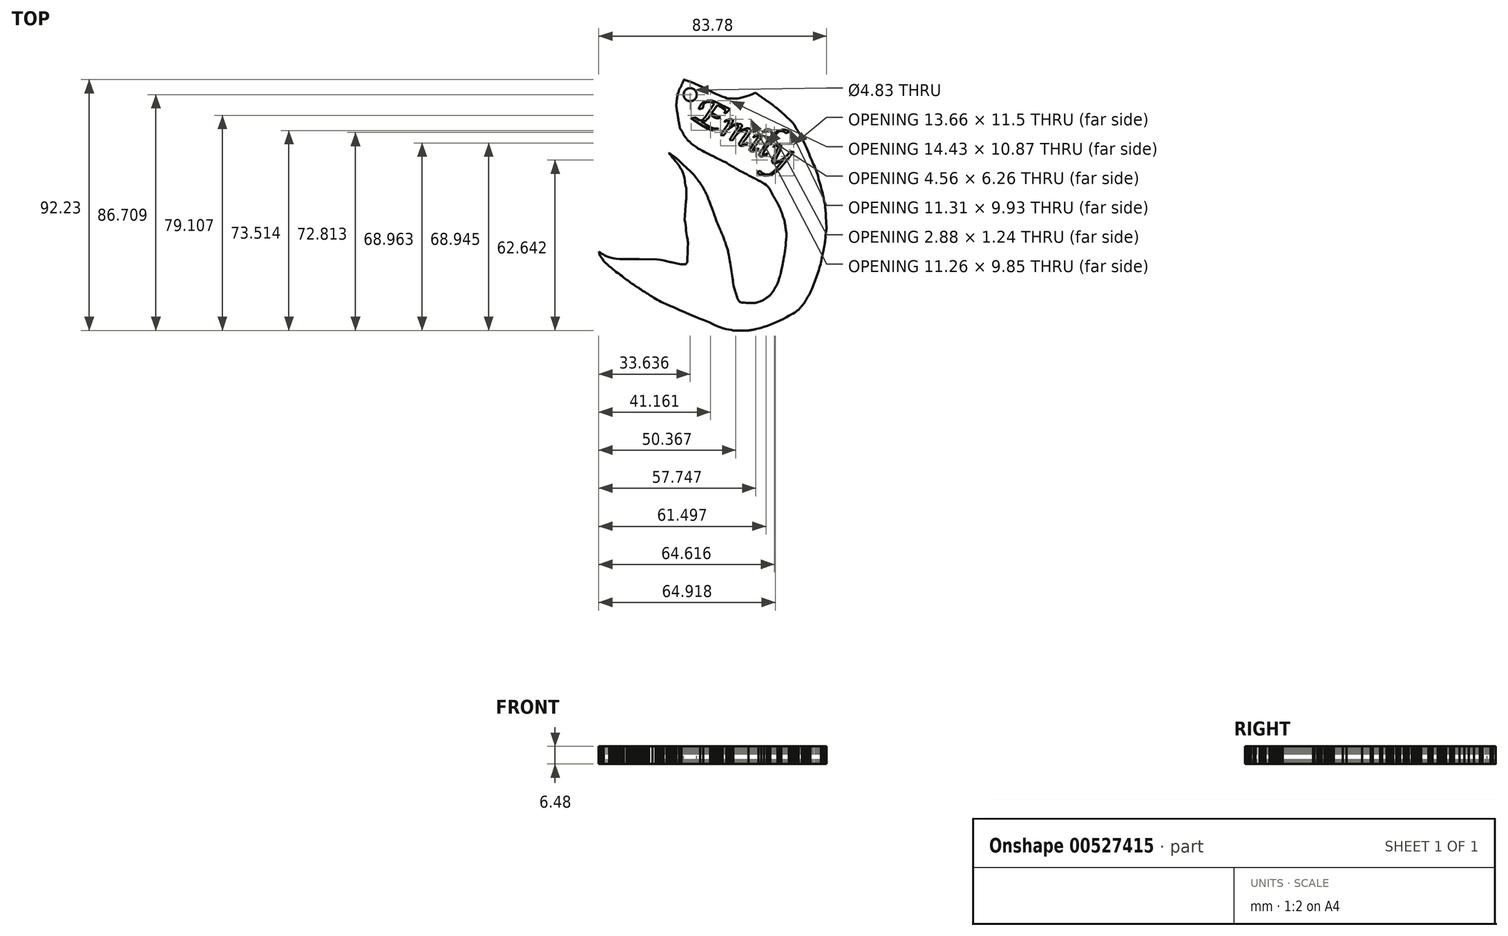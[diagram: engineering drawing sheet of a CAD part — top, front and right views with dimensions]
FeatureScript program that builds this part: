
annotation { "Feature Type Name" : "Feature", "Feature Type Description" : "" }
export const myFeature = defineFeature(function(context is Context, id is Id, definition is map)
    precondition{}
    {
        {
            var Q0;
            Q0=qCreatedBy(makeId("Top.planeOp"),FACE);
            var sketch = newSketch(context, id + "F0", { "sketchPlane" : qUnion([Q0])});
            skLineSegment(sketch, "E0", {"start": v(21.99, 68.15) * mm, "end": v(23.77, 67.5) * mm});
            skLineSegment(sketch, "E1", {"start": v(23.77, 67.5) * mm, "end": v(25.3, 66.86) * mm});
            skLineSegment(sketch, "E2", {"start": v(25.3, 66.86) * mm, "end": v(26.57, 66.23) * mm});
            skLineSegment(sketch, "E3", {"start": v(26.57, 66.23) * mm, "end": v(28.12, 65.46) * mm});
            skLineSegment(sketch, "E4", {"start": v(28.12, 65.46) * mm, "end": v(29.2, 64.92) * mm});
            skLineSegment(sketch, "E5", {"start": v(31.16, 64.07) * mm, "end": v(32, 63.75) * mm});
            skLineSegment(sketch, "E6", {"start": v(32, 63.75) * mm, "end": v(32.46, 63.57) * mm});
            skLineSegment(sketch, "E7", {"start": v(32.46, 63.57) * mm, "end": v(33.1, 63.57) * mm});
            skLineSegment(sketch, "E8", {"start": v(33.1, 63.57) * mm, "end": v(33.64, 63.57) * mm});
            skLineSegment(sketch, "E9", {"start": v(33.64, 63.57) * mm, "end": v(34.22, 63.57) * mm});
            skLineSegment(sketch, "E10", {"start": v(34.22, 63.57) * mm, "end": v(35, 63.57) * mm});
            skLineSegment(sketch, "E11", {"start": v(35, 63.57) * mm, "end": v(36.04, 63.75) * mm});
            skLineSegment(sketch, "E12", {"start": v(36.04, 63.75) * mm, "end": v(36.96, 64.03) * mm});
            skLineSegment(sketch, "E13", {"start": v(36.96, 64.03) * mm, "end": v(38.06, 64.36) * mm});
            skLineSegment(sketch, "E14", {"start": v(38.06, 64.36) * mm, "end": v(38.68, 64.6) * mm});
            skLineSegment(sketch, "E15", {"start": v(38.68, 64.6) * mm, "end": v(39.05, 64.77) * mm});
            skLineSegment(sketch, "E16", {"start": v(39.05, 64.77) * mm, "end": v(39.28, 64.95) * mm});
            skLineSegment(sketch, "E17", {"start": v(39.28, 64.95) * mm, "end": v(39.86, 64.6) * mm});
            skLineSegment(sketch, "E18", {"start": v(39.86, 64.6) * mm, "end": v(40.33, 64.28) * mm});
            skLineSegment(sketch, "E19", {"start": v(40.33, 64.28) * mm, "end": v(40.82, 63.93) * mm});
            skLineSegment(sketch, "E20", {"start": v(40.82, 63.93) * mm, "end": v(41.34, 63.57) * mm});
            skLineSegment(sketch, "E21", {"start": v(41.34, 63.57) * mm, "end": v(41.88, 63.2) * mm});
            skLineSegment(sketch, "E22", {"start": v(41.88, 63.2) * mm, "end": v(42.37, 62.85) * mm});
            skLineSegment(sketch, "E23", {"start": v(42.37, 62.85) * mm, "end": v(42.71, 62.67) * mm});
            skLineSegment(sketch, "E24", {"start": v(42.71, 62.67) * mm, "end": v(43.17, 62.35) * mm});
            skLineSegment(sketch, "E25", {"start": v(43.17, 62.35) * mm, "end": v(43.58, 62) * mm});
            skLineSegment(sketch, "E26", {"start": v(43.58, 62) * mm, "end": v(44.02, 61.6) * mm});
            skLineSegment(sketch, "E27", {"start": v(44.02, 61.6) * mm, "end": v(44.38, 61.36) * mm});
            skLineSegment(sketch, "E28", {"start": v(44.38, 61.36) * mm, "end": v(44.82, 61.04) * mm});
            skLineSegment(sketch, "E29", {"start": v(44.82, 61.04) * mm, "end": v(45.43, 60.46) * mm});
            skLineSegment(sketch, "E30", {"start": v(45.43, 60.46) * mm, "end": v(46.73, 59.3) * mm});
            skLineSegment(sketch, "E31", {"start": v(46.73, 59.3) * mm, "end": v(48.15, 57.92) * mm});
            skLineSegment(sketch, "E32", {"start": v(48.15, 57.92) * mm, "end": v(48.71, 57.46) * mm});
            skLineSegment(sketch, "E33", {"start": v(48.71, 57.46) * mm, "end": v(48.94, 56.98) * mm});
            skLineSegment(sketch, "E34", {"start": v(48.94, 56.98) * mm, "end": v(49.26, 56.45) * mm});
            skLineSegment(sketch, "E35", {"start": v(49.26, 56.45) * mm, "end": v(49.56, 55.94) * mm});
            skLineSegment(sketch, "E36", {"start": v(49.56, 55.94) * mm, "end": v(49.85, 55.48) * mm});
            skLineSegment(sketch, "E37", {"start": v(49.85, 55.48) * mm, "end": v(50.12, 54.97) * mm});
            skLineSegment(sketch, "E38", {"start": v(50.12, 54.97) * mm, "end": v(50.43, 54.48) * mm});
            skLineSegment(sketch, "E39", {"start": v(50.43, 54.48) * mm, "end": v(50.72, 53.9) * mm});
            skLineSegment(sketch, "E40", {"start": v(50.72, 53.9) * mm, "end": v(50.98, 53.42) * mm});
            skLineSegment(sketch, "E41", {"start": v(50.98, 53.42) * mm, "end": v(51.17, 53.06) * mm});
            skLineSegment(sketch, "E42", {"start": v(51.17, 53.06) * mm, "end": v(51.4, 52.65) * mm});
            skLineSegment(sketch, "E43", {"start": v(51.4, 52.65) * mm, "end": v(51.57, 52.15) * mm});
            skLineSegment(sketch, "E44", {"start": v(51.57, 52.15) * mm, "end": v(51.77, 51.67) * mm});
            skLineSegment(sketch, "E45", {"start": v(51.77, 51.67) * mm, "end": v(51.97, 51.22) * mm});
            skLineSegment(sketch, "E46", {"start": v(51.97, 51.22) * mm, "end": v(52.16, 50.81) * mm});
            skLineSegment(sketch, "E47", {"start": v(52.16, 50.81) * mm, "end": v(52.33, 50.44) * mm});
            skLineSegment(sketch, "E48", {"start": v(52.33, 50.44) * mm, "end": v(52.57, 49.9) * mm});
            skLineSegment(sketch, "E49", {"start": v(52.57, 49.9) * mm, "end": v(52.77, 49.35) * mm});
            skLineSegment(sketch, "E50", {"start": v(52.77, 49.35) * mm, "end": v(53, 48.84) * mm});
            skLineSegment(sketch, "E51", {"start": v(53, 48.84) * mm, "end": v(53.14, 48.48) * mm});
            skLineSegment(sketch, "E52", {"start": v(53.14, 48.48) * mm, "end": v(53.32, 48.01) * mm});
            skLineSegment(sketch, "E53", {"start": v(53.32, 48.01) * mm, "end": v(53.52, 47.56) * mm});
            skLineSegment(sketch, "E54", {"start": v(53.52, 47.56) * mm, "end": v(53.73, 47.17) * mm});
            skLineSegment(sketch, "E55", {"start": v(53.73, 47.17) * mm, "end": v(53.89, 46.86) * mm});
            skLineSegment(sketch, "E56", {"start": v(53.89, 46.86) * mm, "end": v(54.02, 46.5) * mm});
            skLineSegment(sketch, "E57", {"start": v(54.02, 46.5) * mm, "end": v(54.18, 46.11) * mm});
            skLineSegment(sketch, "E58", {"start": v(54.18, 46.11) * mm, "end": v(54.35, 45.67) * mm});
            skLineSegment(sketch, "E59", {"start": v(54.35, 45.67) * mm, "end": v(54.5, 45.23) * mm});
            skLineSegment(sketch, "E60", {"start": v(54.5, 45.23) * mm, "end": v(54.65, 44.72) * mm});
            skLineSegment(sketch, "E61", {"start": v(54.65, 44.72) * mm, "end": v(54.75, 44.3) * mm});
            skLineSegment(sketch, "E62", {"start": v(54.75, 44.3) * mm, "end": v(54.88, 43.75) * mm});
            skLineSegment(sketch, "E63", {"start": v(54.88, 43.75) * mm, "end": v(55.12, 43) * mm});
            skLineSegment(sketch, "E64", {"start": v(55.12, 43) * mm, "end": v(55.26, 42.44) * mm});
            skLineSegment(sketch, "E65", {"start": v(55.26, 42.44) * mm, "end": v(55.43, 41.9) * mm});
            skLineSegment(sketch, "E66", {"start": v(55.43, 41.9) * mm, "end": v(55.55, 41.4) * mm});
            skLineSegment(sketch, "E67", {"start": v(55.55, 41.4) * mm, "end": v(55.67, 41.03) * mm});
            skLineSegment(sketch, "E68", {"start": v(55.67, 41.03) * mm, "end": v(55.77, 40.72) * mm});
            skLineSegment(sketch, "E69", {"start": v(55.77, 40.72) * mm, "end": v(55.9, 40.32) * mm});
            skLineSegment(sketch, "E70", {"start": v(55.9, 40.32) * mm, "end": v(56, 39.8) * mm});
            skLineSegment(sketch, "E71", {"start": v(56, 39.8) * mm, "end": v(56.06, 39.41) * mm});
            skLineSegment(sketch, "E72", {"start": v(56.06, 39.41) * mm, "end": v(56.14, 38.95) * mm});
            skLineSegment(sketch, "E73", {"start": v(56.14, 38.95) * mm, "end": v(56.22, 38.5) * mm});
            skLineSegment(sketch, "E74", {"start": v(56.22, 38.5) * mm, "end": v(56.3, 38.06) * mm});
            skLineSegment(sketch, "E75", {"start": v(56.3, 38.06) * mm, "end": v(56.43, 37.51) * mm});
            skLineSegment(sketch, "E76", {"start": v(56.43, 37.51) * mm, "end": v(56.48, 36.9) * mm});
            skLineSegment(sketch, "E77", {"start": v(56.48, 36.9) * mm, "end": v(56.54, 36.23) * mm});
            skLineSegment(sketch, "E78", {"start": v(56.54, 36.23) * mm, "end": v(56.62, 35.38) * mm});
            skLineSegment(sketch, "E79", {"start": v(56.62, 35.38) * mm, "end": v(56.67, 34.42) * mm});
            skLineSegment(sketch, "E80", {"start": v(56.67, 34.42) * mm, "end": v(56.72, 33.51) * mm});
            skLineSegment(sketch, "E81", {"start": v(56.72, 33.51) * mm, "end": v(56.8, 31.59) * mm});
            skLineSegment(sketch, "E82", {"start": v(56.8, 31.59) * mm, "end": v(56.68, 30.65) * mm});
            skLineSegment(sketch, "E83", {"start": v(56.68, 30.65) * mm, "end": v(56.6, 29.89) * mm});
            skLineSegment(sketch, "E84", {"start": v(56.6, 29.89) * mm, "end": v(56.51, 29.2) * mm});
            skLineSegment(sketch, "E85", {"start": v(56.51, 29.2) * mm, "end": v(56.43, 28.47) * mm});
            skLineSegment(sketch, "E86", {"start": v(56.43, 28.47) * mm, "end": v(56.35, 28.06) * mm});
            skLineSegment(sketch, "E87", {"start": v(56.35, 28.06) * mm, "end": v(56.26, 27.48) * mm});
            skLineSegment(sketch, "E88", {"start": v(56.26, 27.48) * mm, "end": v(56.18, 27.12) * mm});
            skLineSegment(sketch, "E89", {"start": v(56.18, 27.12) * mm, "end": v(56.09, 26.65) * mm});
            skLineSegment(sketch, "E90", {"start": v(56.09, 26.65) * mm, "end": v(56.03, 26.18) * mm});
            skLineSegment(sketch, "E91", {"start": v(56.03, 26.18) * mm, "end": v(55.96, 25.86) * mm});
            skLineSegment(sketch, "E92", {"start": v(55.96, 25.86) * mm, "end": v(55.89, 25.52) * mm});
            skLineSegment(sketch, "E93", {"start": v(55.89, 25.52) * mm, "end": v(55.8, 25.11) * mm});
            skLineSegment(sketch, "E94", {"start": v(55.8, 25.11) * mm, "end": v(55.74, 24.73) * mm});
            skLineSegment(sketch, "E95", {"start": v(55.74, 24.73) * mm, "end": v(55.66, 24.4) * mm});
            skLineSegment(sketch, "E96", {"start": v(55.66, 24.4) * mm, "end": v(55.58, 24.05) * mm});
            skLineSegment(sketch, "E97", {"start": v(55.58, 24.05) * mm, "end": v(55.51, 23.72) * mm});
            skLineSegment(sketch, "E98", {"start": v(55.51, 23.72) * mm, "end": v(55.48, 23.38) * mm});
            skLineSegment(sketch, "E99", {"start": v(52.97, 16.32) * mm, "end": v(52.83, 15.96) * mm});
            skLineSegment(sketch, "E100", {"start": v(52.83, 15.96) * mm, "end": v(52.66, 15.64) * mm});
            skLineSegment(sketch, "E101", {"start": v(52.66, 15.64) * mm, "end": v(52.54, 15.43) * mm});
            skLineSegment(sketch, "E102", {"start": v(52.54, 15.43) * mm, "end": v(52.38, 15.17) * mm});
            skLineSegment(sketch, "E103", {"start": v(52.38, 15.17) * mm, "end": v(52.16, 14.84) * mm});
            skLineSegment(sketch, "E104", {"start": v(52.16, 14.84) * mm, "end": v(51.98, 14.49) * mm});
            skLineSegment(sketch, "E105", {"start": v(51.98, 14.49) * mm, "end": v(51.8, 14.17) * mm});
            skLineSegment(sketch, "E106", {"start": v(51.8, 14.17) * mm, "end": v(51.6, 13.88) * mm});
            skLineSegment(sketch, "E107", {"start": v(51.6, 13.88) * mm, "end": v(51.46, 13.62) * mm});
            skLineSegment(sketch, "E108", {"start": v(51.46, 13.62) * mm, "end": v(51.28, 13.34) * mm});
            skLineSegment(sketch, "E109", {"start": v(51.28, 13.34) * mm, "end": v(51.13, 13.14) * mm});
            skLineSegment(sketch, "E110", {"start": v(51.13, 13.14) * mm, "end": v(51.05, 13) * mm});
            skLineSegment(sketch, "E111", {"start": v(51.05, 13) * mm, "end": v(50.83, 12.71) * mm});
            skLineSegment(sketch, "E112", {"start": v(50.83, 12.71) * mm, "end": v(50.52, 12.38) * mm});
            skLineSegment(sketch, "E113", {"start": v(50.52, 12.38) * mm, "end": v(50.25, 12.08) * mm});
            skLineSegment(sketch, "E114", {"start": v(50.25, 12.08) * mm, "end": v(49.92, 11.72) * mm});
            skLineSegment(sketch, "E115", {"start": v(49.92, 11.72) * mm, "end": v(49.63, 11.52) * mm});
            skLineSegment(sketch, "E116", {"start": v(49.63, 11.52) * mm, "end": v(49.33, 11.3) * mm});
            skLineSegment(sketch, "E117", {"start": v(49.33, 11.3) * mm, "end": v(49, 11.08) * mm});
            skLineSegment(sketch, "E118", {"start": v(49, 11.08) * mm, "end": v(48.6, 10.83) * mm});
            skLineSegment(sketch, "E119", {"start": v(48.6, 10.83) * mm, "end": v(48.2, 10.62) * mm});
            skLineSegment(sketch, "E120", {"start": v(48.2, 10.62) * mm, "end": v(47.93, 10.45) * mm});
            skLineSegment(sketch, "E121", {"start": v(47.93, 10.45) * mm, "end": v(47.56, 10.27) * mm});
            skLineSegment(sketch, "E122", {"start": v(47.56, 10.27) * mm, "end": v(47.19, 10.06) * mm});
            skLineSegment(sketch, "E123", {"start": v(47.19, 10.06) * mm, "end": v(46.9, 9.9) * mm});
            skLineSegment(sketch, "E124", {"start": v(45.98, 9.4) * mm, "end": v(45.69, 9.23) * mm});
            skLineSegment(sketch, "E125", {"start": v(45.69, 9.23) * mm, "end": v(45.35, 9.1) * mm});
            skLineSegment(sketch, "E126", {"start": v(45.35, 9.1) * mm, "end": v(44.81, 8.83) * mm});
            skLineSegment(sketch, "E127", {"start": v(44.81, 8.83) * mm, "end": v(44.19, 8.58) * mm});
            skLineSegment(sketch, "E128", {"start": v(44.19, 8.58) * mm, "end": v(43.56, 8.34) * mm});
            skLineSegment(sketch, "E129", {"start": v(43.56, 8.34) * mm, "end": v(43.02, 8.12) * mm});
            skLineSegment(sketch, "E130", {"start": v(43.02, 8.12) * mm, "end": v(42.54, 7.89) * mm});
            skLineSegment(sketch, "E131", {"start": v(42.54, 7.89) * mm, "end": v(42.13, 7.77) * mm});
            skLineSegment(sketch, "E132", {"start": v(42.13, 7.77) * mm, "end": v(41.47, 7.54) * mm});
            skLineSegment(sketch, "E133", {"start": v(41.47, 7.54) * mm, "end": v(40.82, 7.36) * mm});
            skLineSegment(sketch, "E134", {"start": v(40.82, 7.36) * mm, "end": v(40.13, 7.19) * mm});
            skLineSegment(sketch, "E135", {"start": v(40.13, 7.19) * mm, "end": v(39.64, 7.05) * mm});
            skLineSegment(sketch, "E136", {"start": v(37.68, 6.67) * mm, "end": v(33.9, 6.67) * mm});
            skLineSegment(sketch, "E137", {"start": v(33.9, 6.67) * mm, "end": v(33.4, 6.81) * mm});
            skLineSegment(sketch, "E138", {"start": v(33.4, 6.81) * mm, "end": v(32.85, 6.91) * mm});
            skLineSegment(sketch, "E139", {"start": v(32.85, 6.91) * mm, "end": v(32.21, 7.01) * mm});
            skLineSegment(sketch, "E140", {"start": v(32.21, 7.01) * mm, "end": v(31.67, 7.17) * mm});
            skLineSegment(sketch, "E141", {"start": v(31.67, 7.17) * mm, "end": v(31.3, 7.28) * mm});
            skLineSegment(sketch, "E142", {"start": v(31.3, 7.28) * mm, "end": v(30.9, 7.43) * mm});
            skLineSegment(sketch, "E143", {"start": v(30.9, 7.43) * mm, "end": v(30.4, 7.57) * mm});
            skLineSegment(sketch, "E144", {"start": v(30.4, 7.57) * mm, "end": v(30, 7.76) * mm});
            skLineSegment(sketch, "E145", {"start": v(30, 7.76) * mm, "end": v(29.4, 8.04) * mm});
            skLineSegment(sketch, "E146", {"start": v(29.4, 8.04) * mm, "end": v(28.89, 8.28) * mm});
            skLineSegment(sketch, "E147", {"start": v(28.89, 8.28) * mm, "end": v(28.25, 8.57) * mm});
            skLineSegment(sketch, "E148", {"start": v(28.25, 8.57) * mm, "end": v(27.82, 8.75) * mm});
            skLineSegment(sketch, "E149", {"start": v(27.82, 8.75) * mm, "end": v(27.3, 8.97) * mm});
            skLineSegment(sketch, "E150", {"start": v(27.3, 8.97) * mm, "end": v(26.57, 9.27) * mm});
            skLineSegment(sketch, "E151", {"start": v(26.57, 9.27) * mm, "end": v(25.83, 9.55) * mm});
            skLineSegment(sketch, "E152", {"start": v(25.83, 9.55) * mm, "end": v(25.29, 9.77) * mm});
            skLineSegment(sketch, "E153", {"start": v(25.29, 9.77) * mm, "end": v(24.98, 9.9) * mm});
            skLineSegment(sketch, "E154", {"start": v(24.98, 9.9) * mm, "end": v(24.3, 10.19) * mm});
            skLineSegment(sketch, "E155", {"start": v(24.3, 10.19) * mm, "end": v(23.65, 10.46) * mm});
            skLineSegment(sketch, "E156", {"start": v(23.65, 10.46) * mm, "end": v(23.1, 10.69) * mm});
            skLineSegment(sketch, "E157", {"start": v(23.1, 10.69) * mm, "end": v(22.46, 10.96) * mm});
            skLineSegment(sketch, "E158", {"start": v(22.46, 10.96) * mm, "end": v(21.9, 11.19) * mm});
            skLineSegment(sketch, "E159", {"start": v(21.9, 11.19) * mm, "end": v(21.22, 11.47) * mm});
            skLineSegment(sketch, "E160", {"start": v(21.22, 11.47) * mm, "end": v(20.69, 11.75) * mm});
            skLineSegment(sketch, "E161", {"start": v(20.69, 11.75) * mm, "end": v(20, 12.03) * mm});
            skLineSegment(sketch, "E162", {"start": v(20, 12.03) * mm, "end": v(19.48, 12.3) * mm});
            skLineSegment(sketch, "E163", {"start": v(19.48, 12.3) * mm, "end": v(19, 12.5) * mm});
            skLineSegment(sketch, "E164", {"start": v(19, 12.5) * mm, "end": v(18.53, 12.68) * mm});
            skLineSegment(sketch, "E165", {"start": v(18.53, 12.68) * mm, "end": v(18.21, 12.83) * mm});
            skLineSegment(sketch, "E166", {"start": v(18.21, 12.83) * mm, "end": v(17.57, 13.08) * mm});
            skLineSegment(sketch, "E167", {"start": v(17.57, 13.08) * mm, "end": v(16.85, 13.4) * mm});
            skLineSegment(sketch, "E168", {"start": v(16.85, 13.4) * mm, "end": v(16.28, 13.7) * mm});
            skLineSegment(sketch, "E169", {"start": v(16.28, 13.7) * mm, "end": v(15.8, 13.96) * mm});
            skLineSegment(sketch, "E170", {"start": v(15.8, 13.96) * mm, "end": v(15.3, 14.17) * mm});
            skLineSegment(sketch, "E171", {"start": v(15.3, 14.17) * mm, "end": v(14.93, 14.43) * mm});
            skLineSegment(sketch, "E172", {"start": v(14.93, 14.43) * mm, "end": v(14.5, 14.68) * mm});
            skLineSegment(sketch, "E173", {"start": v(14.5, 14.68) * mm, "end": v(14.1, 14.9) * mm});
            skLineSegment(sketch, "E174", {"start": v(14.1, 14.9) * mm, "end": v(13.6, 15.23) * mm});
            skLineSegment(sketch, "E175", {"start": v(13.6, 15.23) * mm, "end": v(13.24, 15.46) * mm});
            skLineSegment(sketch, "E176", {"start": v(13.24, 15.46) * mm, "end": v(12.96, 15.69) * mm});
            skLineSegment(sketch, "E177", {"start": v(12.96, 15.69) * mm, "end": v(12.71, 15.8) * mm});
            skLineSegment(sketch, "E178", {"start": v(12.71, 15.8) * mm, "end": v(12.29, 16.09) * mm});
            skLineSegment(sketch, "E179", {"start": v(12.29, 16.09) * mm, "end": v(11.7, 16.42) * mm});
            skLineSegment(sketch, "E180", {"start": v(11.7, 16.42) * mm, "end": v(11.35, 16.68) * mm});
            skLineSegment(sketch, "E181", {"start": v(11.35, 16.68) * mm, "end": v(11.02, 16.9) * mm});
            skLineSegment(sketch, "E182", {"start": v(11.02, 16.9) * mm, "end": v(10.71, 17.11) * mm});
            skLineSegment(sketch, "E183", {"start": v(10.71, 17.11) * mm, "end": v(10.3, 17.35) * mm});
            skLineSegment(sketch, "E184", {"start": v(10.3, 17.35) * mm, "end": v(9.84, 17.66) * mm});
            skLineSegment(sketch, "E185", {"start": v(9.84, 17.66) * mm, "end": v(9.54, 17.88) * mm});
            skLineSegment(sketch, "E186", {"start": v(9.54, 17.88) * mm, "end": v(9.4, 17.96) * mm});
            skLineSegment(sketch, "E187", {"start": v(9.4, 17.96) * mm, "end": v(9.07, 18.18) * mm});
            skLineSegment(sketch, "E188", {"start": v(9.07, 18.18) * mm, "end": v(8.8, 18.36) * mm});
            skLineSegment(sketch, "E189", {"start": v(8.8, 18.36) * mm, "end": v(8.5, 18.56) * mm});
            skLineSegment(sketch, "E190", {"start": v(8.5, 18.56) * mm, "end": v(8.12, 18.89) * mm});
            skLineSegment(sketch, "E191", {"start": v(8.12, 18.89) * mm, "end": v(7.77, 19.12) * mm});
            skLineSegment(sketch, "E192", {"start": v(7.77, 19.12) * mm, "end": v(7.46, 19.35) * mm});
            skLineSegment(sketch, "E193", {"start": v(7.46, 19.35) * mm, "end": v(7.1, 19.6) * mm});
            skLineSegment(sketch, "E194", {"start": v(7.1, 19.6) * mm, "end": v(6.66, 20.02) * mm});
            skLineSegment(sketch, "E195", {"start": v(6.66, 20.02) * mm, "end": v(6.3, 20.27) * mm});
            skLineSegment(sketch, "E196", {"start": v(6.3, 20.27) * mm, "end": v(5.92, 20.58) * mm});
            skLineSegment(sketch, "E197", {"start": v(5.92, 20.58) * mm, "end": v(5.58, 20.77) * mm});
            skLineSegment(sketch, "E198", {"start": v(5.58, 20.77) * mm, "end": v(5.18, 21.07) * mm});
            skLineSegment(sketch, "E199", {"start": v(5.18, 21.07) * mm, "end": v(4.85, 21.4) * mm});
            skLineSegment(sketch, "E200", {"start": v(4.85, 21.4) * mm, "end": v(4.43, 21.71) * mm});
            skLineSegment(sketch, "E201", {"start": v(4.43, 21.71) * mm, "end": v(4.16, 21.96) * mm});
            skLineSegment(sketch, "E202", {"start": v(4.16, 21.96) * mm, "end": v(3.6, 22.4) * mm});
            skLineSegment(sketch, "E203", {"start": v(3.6, 22.4) * mm, "end": v(2.88, 23.06) * mm});
            skLineSegment(sketch, "E204", {"start": v(2.88, 23.06) * mm, "end": v(2.18, 23.7) * mm});
            skLineSegment(sketch, "E205", {"start": v(2.18, 23.7) * mm, "end": v(1.89, 24.22) * mm});
            skLineSegment(sketch, "E206", {"start": v(1.89, 24.22) * mm, "end": v(1.62, 24.52) * mm});
            skLineSegment(sketch, "E207", {"start": v(1.62, 24.52) * mm, "end": v(1.45, 24.8) * mm});
            skLineSegment(sketch, "E208", {"start": v(1.45, 24.8) * mm, "end": v(1.3, 25.02) * mm});
            skLineSegment(sketch, "E209", {"start": v(1.3, 25.02) * mm, "end": v(1.17, 25.29) * mm});
            skLineSegment(sketch, "E210", {"start": v(1.17, 25.29) * mm, "end": v(1.12, 25.5) * mm});
            skLineSegment(sketch, "E211", {"start": v(1.12, 25.5) * mm, "end": v(1.06, 25.71) * mm});
            skLineSegment(sketch, "E212", {"start": v(1.06, 25.71) * mm, "end": v(0.95, 25.8) * mm});
            skLineSegment(sketch, "E213", {"start": v(0.95, 25.8) * mm, "end": v(1.02, 25.93) * mm});
            skLineSegment(sketch, "E214", {"start": v(1.02, 25.93) * mm, "end": v(1.14, 25.89) * mm});
            skLineSegment(sketch, "E215", {"start": v(1.14, 25.89) * mm, "end": v(1.32, 25.75) * mm});
            skLineSegment(sketch, "E216", {"start": v(1.32, 25.75) * mm, "end": v(1.77, 25.48) * mm});
            skLineSegment(sketch, "E217", {"start": v(1.77, 25.48) * mm, "end": v(1.99, 25.36) * mm});
            skLineSegment(sketch, "E218", {"start": v(1.99, 25.36) * mm, "end": v(2.39, 25.14) * mm});
            skLineSegment(sketch, "E219", {"start": v(2.39, 25.14) * mm, "end": v(2.7, 24.96) * mm});
            skLineSegment(sketch, "E220", {"start": v(2.7, 24.96) * mm, "end": v(3.12, 24.79) * mm});
            skLineSegment(sketch, "E221", {"start": v(3.12, 24.79) * mm, "end": v(3.67, 24.6) * mm});
            skLineSegment(sketch, "E222", {"start": v(3.67, 24.6) * mm, "end": v(4.3, 24.42) * mm});
            skLineSegment(sketch, "E223", {"start": v(4.3, 24.42) * mm, "end": v(4.73, 24.33) * mm});
            skLineSegment(sketch, "E224", {"start": v(4.73, 24.33) * mm, "end": v(5.22, 24.26) * mm});
            skLineSegment(sketch, "E225", {"start": v(5.22, 24.26) * mm, "end": v(6.1, 24.2) * mm});
            skLineSegment(sketch, "E226", {"start": v(6.1, 24.2) * mm, "end": v(10.94, 24.15) * mm});
            skLineSegment(sketch, "E227", {"start": v(10.94, 24.15) * mm, "end": v(15.26, 24.08) * mm});
            skLineSegment(sketch, "E228", {"start": v(15.26, 24.08) * mm, "end": v(16.03, 24) * mm});
            skLineSegment(sketch, "E229", {"start": v(16.03, 24) * mm, "end": v(16.52, 23.88) * mm});
            skLineSegment(sketch, "E230", {"start": v(16.52, 23.88) * mm, "end": v(16.93, 23.8) * mm});
            skLineSegment(sketch, "E231", {"start": v(16.93, 23.8) * mm, "end": v(17.27, 23.74) * mm});
            skLineSegment(sketch, "E232", {"start": v(17.27, 23.74) * mm, "end": v(17.56, 23.68) * mm});
            skLineSegment(sketch, "E233", {"start": v(17.56, 23.68) * mm, "end": v(17.87, 23.6) * mm});
            skLineSegment(sketch, "E234", {"start": v(17.87, 23.6) * mm, "end": v(18.26, 23.53) * mm});
            skLineSegment(sketch, "E235", {"start": v(18.26, 23.53) * mm, "end": v(18.55, 23.44) * mm});
            skLineSegment(sketch, "E236", {"start": v(18.55, 23.44) * mm, "end": v(18.89, 23.37) * mm});
            skLineSegment(sketch, "E237", {"start": v(18.89, 23.37) * mm, "end": v(19.16, 23.3) * mm});
            skLineSegment(sketch, "E238", {"start": v(19.16, 23.3) * mm, "end": v(19.55, 23.23) * mm});
            skLineSegment(sketch, "E239", {"start": v(19.55, 23.23) * mm, "end": v(19.87, 23.13) * mm});
            skLineSegment(sketch, "E240", {"start": v(19.87, 23.13) * mm, "end": v(20.26, 23.06) * mm});
            skLineSegment(sketch, "E241", {"start": v(20.26, 23.06) * mm, "end": v(20.62, 22.98) * mm});
            skLineSegment(sketch, "E242", {"start": v(20.62, 22.98) * mm, "end": v(21.1, 22.91) * mm});
            skLineSegment(sketch, "E243", {"start": v(21.1, 22.91) * mm, "end": v(22.17, 22.88) * mm});
            skLineSegment(sketch, "E244", {"start": v(22.17, 22.88) * mm, "end": v(22.33, 23.01) * mm});
            skLineSegment(sketch, "E245", {"start": v(22.33, 23.01) * mm, "end": v(22.45, 23.1) * mm});
            skLineSegment(sketch, "E246", {"start": v(22.45, 23.1) * mm, "end": v(22.5, 23.2) * mm});
            skLineSegment(sketch, "E247", {"start": v(22.5, 23.2) * mm, "end": v(22.6, 23.3) * mm});
            skLineSegment(sketch, "E248", {"start": v(22.6, 23.3) * mm, "end": v(22.65, 23.45) * mm});
            skLineSegment(sketch, "E249", {"start": v(22.65, 23.45) * mm, "end": v(22.68, 23.57) * mm});
            skLineSegment(sketch, "E250", {"start": v(22.68, 23.57) * mm, "end": v(22.75, 26.62) * mm});
            skLineSegment(sketch, "E251", {"start": v(22.75, 26.62) * mm, "end": v(22.82, 28.3) * mm});
            skLineSegment(sketch, "E252", {"start": v(22.82, 28.3) * mm, "end": v(22.77, 28.55) * mm});
            skLineSegment(sketch, "E253", {"start": v(22.77, 28.55) * mm, "end": v(22.73, 28.94) * mm});
            skLineSegment(sketch, "E254", {"start": v(22.73, 28.94) * mm, "end": v(22.66, 29.3) * mm});
            skLineSegment(sketch, "E255", {"start": v(22.66, 29.3) * mm, "end": v(22.62, 29.55) * mm});
            skLineSegment(sketch, "E256", {"start": v(22.62, 29.55) * mm, "end": v(22.56, 30.07) * mm});
            skLineSegment(sketch, "E257", {"start": v(22.56, 30.07) * mm, "end": v(22.45, 30.57) * mm});
            skLineSegment(sketch, "E258", {"start": v(22.45, 30.57) * mm, "end": v(22.38, 31.2) * mm});
            skLineSegment(sketch, "E259", {"start": v(22.38, 31.2) * mm, "end": v(22.3, 31.8) * mm});
            skLineSegment(sketch, "E260", {"start": v(22.3, 31.8) * mm, "end": v(22.23, 32.66) * mm});
            skLineSegment(sketch, "E261", {"start": v(22.23, 32.66) * mm, "end": v(22.14, 33.14) * mm});
            skLineSegment(sketch, "E262", {"start": v(22.14, 33.14) * mm, "end": v(22.09, 33.47) * mm});
            skLineSegment(sketch, "E263", {"start": v(22.09, 33.47) * mm, "end": v(22, 33.76) * mm});
            skLineSegment(sketch, "E264", {"start": v(22, 33.76) * mm, "end": v(22.08, 34.95) * mm});
            skLineSegment(sketch, "E265", {"start": v(22.08, 34.95) * mm, "end": v(22.15, 36.07) * mm});
            skLineSegment(sketch, "E266", {"start": v(22.15, 36.07) * mm, "end": v(22.23, 37.58) * mm});
            skLineSegment(sketch, "E267", {"start": v(22.23, 37.58) * mm, "end": v(22.3, 38.16) * mm});
            skLineSegment(sketch, "E268", {"start": v(22.3, 38.16) * mm, "end": v(22.37, 38.6) * mm});
            skLineSegment(sketch, "E269", {"start": v(22.37, 38.6) * mm, "end": v(22.4, 38.81) * mm});
            skLineSegment(sketch, "E270", {"start": v(22.4, 38.81) * mm, "end": v(22.41, 38.96) * mm});
            skLineSegment(sketch, "E271", {"start": v(22.41, 38.96) * mm, "end": v(22.42, 39.06) * mm});
            skLineSegment(sketch, "E272", {"start": v(22.42, 39.06) * mm, "end": v(22.41, 39.12) * mm});
            skLineSegment(sketch, "E273", {"start": v(22.41, 39.12) * mm, "end": v(22.41, 39.22) * mm});
            skLineSegment(sketch, "E274", {"start": v(22.41, 39.22) * mm, "end": v(22.42, 39.36) * mm});
            skLineSegment(sketch, "E275", {"start": v(22.42, 39.36) * mm, "end": v(22.41, 39.5) * mm});
            skLineSegment(sketch, "E276", {"start": v(22.41, 39.5) * mm, "end": v(22.4, 39.6) * mm});
            skLineSegment(sketch, "E277", {"start": v(22.4, 39.6) * mm, "end": v(22.4, 39.7) * mm});
            skLineSegment(sketch, "E278", {"start": v(22.4, 39.7) * mm, "end": v(22.4, 39.8) * mm});
            skLineSegment(sketch, "E279", {"start": v(22.4, 39.8) * mm, "end": v(22.4, 39.89) * mm});
            skLineSegment(sketch, "E280", {"start": v(22.4, 39.89) * mm, "end": v(22.4, 40.02) * mm});
            skLineSegment(sketch, "E281", {"start": v(22.4, 40.02) * mm, "end": v(22.4, 40.12) * mm});
            skLineSegment(sketch, "E282", {"start": v(22.4, 40.12) * mm, "end": v(22.4, 40.3) * mm});
            skLineSegment(sketch, "E283", {"start": v(22.4, 40.3) * mm, "end": v(22.4, 40.4) * mm});
            skLineSegment(sketch, "E284", {"start": v(22.4, 40.4) * mm, "end": v(22.41, 40.53) * mm});
            skLineSegment(sketch, "E285", {"start": v(22.41, 40.53) * mm, "end": v(22.42, 40.62) * mm});
            skLineSegment(sketch, "E286", {"start": v(22.42, 40.62) * mm, "end": v(22.43, 40.76) * mm});
            skLineSegment(sketch, "E287", {"start": v(22.43, 40.76) * mm, "end": v(22.43, 40.85) * mm});
            skLineSegment(sketch, "E288", {"start": v(22.43, 40.85) * mm, "end": v(22.44, 40.95) * mm});
            skLineSegment(sketch, "E289", {"start": v(22.44, 40.95) * mm, "end": v(22.43, 41.08) * mm});
            skLineSegment(sketch, "E290", {"start": v(22.43, 41.08) * mm, "end": v(22.43, 41.18) * mm});
            skLineSegment(sketch, "E291", {"start": v(22.43, 41.18) * mm, "end": v(22.43, 41.27) * mm});
            skLineSegment(sketch, "E292", {"start": v(22.43, 41.27) * mm, "end": v(22.42, 41.39) * mm});
            skLineSegment(sketch, "E293", {"start": v(22.42, 41.39) * mm, "end": v(22.42, 41.5) * mm});
            skLineSegment(sketch, "E294", {"start": v(22.42, 41.5) * mm, "end": v(22.4, 41.64) * mm});
            skLineSegment(sketch, "E295", {"start": v(22.4, 41.64) * mm, "end": v(22.38, 41.75) * mm});
            skLineSegment(sketch, "E296", {"start": v(22.38, 41.75) * mm, "end": v(22.35, 41.88) * mm});
            skLineSegment(sketch, "E297", {"start": v(22.35, 41.88) * mm, "end": v(22.33, 41.98) * mm});
            skLineSegment(sketch, "E298", {"start": v(22.33, 41.98) * mm, "end": v(22.3, 42.07) * mm});
            skLineSegment(sketch, "E299", {"start": v(22.3, 42.07) * mm, "end": v(22.27, 42.12) * mm});
            skLineSegment(sketch, "E300", {"start": v(22.27, 42.12) * mm, "end": v(22.22, 42.24) * mm});
            skLineSegment(sketch, "E301", {"start": v(22.22, 42.24) * mm, "end": v(22.19, 42.4) * mm});
            skLineSegment(sketch, "E302", {"start": v(22.19, 42.4) * mm, "end": v(22.13, 42.87) * mm});
            skLineSegment(sketch, "E303", {"start": v(22.13, 42.87) * mm, "end": v(22.06, 43.42) * mm});
            skLineSegment(sketch, "E304", {"start": v(22.06, 43.42) * mm, "end": v(21.98, 43.9) * mm});
            skLineSegment(sketch, "E305", {"start": v(21.98, 43.9) * mm, "end": v(21.91, 44.29) * mm});
            skLineSegment(sketch, "E306", {"start": v(21.91, 44.29) * mm, "end": v(21.83, 44.59) * mm});
            skLineSegment(sketch, "E307", {"start": v(21.83, 44.59) * mm, "end": v(21.74, 44.9) * mm});
            skLineSegment(sketch, "E308", {"start": v(21.74, 44.9) * mm, "end": v(21.67, 45.16) * mm});
            skLineSegment(sketch, "E309", {"start": v(21.67, 45.16) * mm, "end": v(21.6, 45.36) * mm});
            skLineSegment(sketch, "E310", {"start": v(21.6, 45.36) * mm, "end": v(21.5, 45.6) * mm});
            skLineSegment(sketch, "E311", {"start": v(21.5, 45.6) * mm, "end": v(21.38, 45.81) * mm});
            skLineSegment(sketch, "E312", {"start": v(21.38, 45.81) * mm, "end": v(21.3, 46.02) * mm});
            skLineSegment(sketch, "E313", {"start": v(21.3, 46.02) * mm, "end": v(21.16, 46.27) * mm});
            skLineSegment(sketch, "E314", {"start": v(21.16, 46.27) * mm, "end": v(21, 46.46) * mm});
            skLineSegment(sketch, "E315", {"start": v(21, 46.46) * mm, "end": v(20.93, 46.63) * mm});
            skLineSegment(sketch, "E316", {"start": v(20.93, 46.63) * mm, "end": v(20.85, 46.8) * mm});
            skLineSegment(sketch, "E317", {"start": v(20.85, 46.8) * mm, "end": v(20.74, 46.95) * mm});
            skLineSegment(sketch, "E318", {"start": v(20.74, 46.95) * mm, "end": v(20.63, 47.1) * mm});
            skLineSegment(sketch, "E319", {"start": v(20.63, 47.1) * mm, "end": v(20.56, 47.2) * mm});
            skLineSegment(sketch, "E320", {"start": v(20.56, 47.2) * mm, "end": v(20.46, 47.3) * mm});
            skLineSegment(sketch, "E321", {"start": v(20.46, 47.3) * mm, "end": v(20.39, 47.46) * mm});
            skLineSegment(sketch, "E322", {"start": v(20.39, 47.46) * mm, "end": v(20.23, 47.63) * mm});
            skLineSegment(sketch, "E323", {"start": v(20.23, 47.63) * mm, "end": v(20.13, 47.76) * mm});
            skLineSegment(sketch, "E324", {"start": v(20.13, 47.76) * mm, "end": v(19.95, 47.97) * mm});
            skLineSegment(sketch, "E325", {"start": v(19.95, 47.97) * mm, "end": v(19.86, 48.1) * mm});
            skLineSegment(sketch, "E326", {"start": v(19.86, 48.1) * mm, "end": v(19.74, 48.23) * mm});
            skLineSegment(sketch, "E327", {"start": v(19.74, 48.23) * mm, "end": v(19.58, 48.44) * mm});
            skLineSegment(sketch, "E328", {"start": v(19.58, 48.44) * mm, "end": v(19.47, 48.57) * mm});
            skLineSegment(sketch, "E329", {"start": v(19.47, 48.57) * mm, "end": v(19.26, 48.78) * mm});
            skLineSegment(sketch, "E330", {"start": v(19.26, 48.78) * mm, "end": v(19.08, 49) * mm});
            skLineSegment(sketch, "E331", {"start": v(19.08, 49) * mm, "end": v(18.98, 49.13) * mm});
            skLineSegment(sketch, "E332", {"start": v(18.98, 49.13) * mm, "end": v(18.86, 49.31) * mm});
            skLineSegment(sketch, "E333", {"start": v(18.86, 49.31) * mm, "end": v(18.7, 49.46) * mm});
            skLineSegment(sketch, "E334", {"start": v(18.7, 49.46) * mm, "end": v(18.58, 49.61) * mm});
            skLineSegment(sketch, "E335", {"start": v(18.58, 49.61) * mm, "end": v(18.4, 49.8) * mm});
            skLineSegment(sketch, "E336", {"start": v(18.4, 49.8) * mm, "end": v(18.27, 49.96) * mm});
            skLineSegment(sketch, "E337", {"start": v(18.27, 49.96) * mm, "end": v(18.14, 50.16) * mm});
            skLineSegment(sketch, "E338", {"start": v(18.14, 50.16) * mm, "end": v(18.2, 50.21) * mm});
            skLineSegment(sketch, "E339", {"start": v(18.2, 50.21) * mm, "end": v(18.28, 50.2) * mm});
            skLineSegment(sketch, "E340", {"start": v(18.28, 50.2) * mm, "end": v(18.32, 50.14) * mm});
            skLineSegment(sketch, "E341", {"start": v(18.32, 50.14) * mm, "end": v(18.5, 49.99) * mm});
            skLineSegment(sketch, "E342", {"start": v(18.5, 49.99) * mm, "end": v(18.73, 49.8) * mm});
            skLineSegment(sketch, "E343", {"start": v(18.73, 49.8) * mm, "end": v(18.9, 49.7) * mm});
            skLineSegment(sketch, "E344", {"start": v(18.9, 49.7) * mm, "end": v(18.98, 49.6) * mm});
            skLineSegment(sketch, "E345", {"start": v(18.98, 49.6) * mm, "end": v(19.1, 49.55) * mm});
            skLineSegment(sketch, "E346", {"start": v(19.1, 49.55) * mm, "end": v(19.27, 49.42) * mm});
            skLineSegment(sketch, "E347", {"start": v(19.27, 49.42) * mm, "end": v(19.4, 49.34) * mm});
            skLineSegment(sketch, "E348", {"start": v(19.4, 49.34) * mm, "end": v(19.58, 49.2) * mm});
            skLineSegment(sketch, "E349", {"start": v(19.58, 49.2) * mm, "end": v(19.81, 49.03) * mm});
            skLineSegment(sketch, "E350", {"start": v(19.81, 49.03) * mm, "end": v(20.09, 48.83) * mm});
            skLineSegment(sketch, "E351", {"start": v(20.09, 48.83) * mm, "end": v(20.57, 48.35) * mm});
            skLineSegment(sketch, "E352", {"start": v(20.57, 48.35) * mm, "end": v(21.62, 47.37) * mm});
            skLineSegment(sketch, "E353", {"start": v(21.62, 47.37) * mm, "end": v(23.4, 45.65) * mm});
            skLineSegment(sketch, "E354", {"start": v(23.4, 45.65) * mm, "end": v(24.41, 44.7) * mm});
            skLineSegment(sketch, "E355", {"start": v(24.41, 44.7) * mm, "end": v(24.46, 44.6) * mm});
            skLineSegment(sketch, "E356", {"start": v(24.46, 44.6) * mm, "end": v(24.52, 44.46) * mm});
            skLineSegment(sketch, "E357", {"start": v(24.52, 44.46) * mm, "end": v(24.72, 44.2) * mm});
            skLineSegment(sketch, "E358", {"start": v(24.72, 44.2) * mm, "end": v(24.83, 44.11) * mm});
            skLineSegment(sketch, "E359", {"start": v(24.83, 44.11) * mm, "end": v(25.07, 43.77) * mm});
            skLineSegment(sketch, "E360", {"start": v(25.07, 43.77) * mm, "end": v(25.3, 43.45) * mm});
            skLineSegment(sketch, "E361", {"start": v(25.3, 43.45) * mm, "end": v(25.5, 43.23) * mm});
            skLineSegment(sketch, "E362", {"start": v(25.5, 43.23) * mm, "end": v(25.73, 42.93) * mm});
            skLineSegment(sketch, "E363", {"start": v(25.73, 42.93) * mm, "end": v(25.9, 42.74) * mm});
            skLineSegment(sketch, "E364", {"start": v(25.9, 42.74) * mm, "end": v(26.01, 42.57) * mm});
            skLineSegment(sketch, "E365", {"start": v(26.01, 42.57) * mm, "end": v(26.18, 42.3) * mm});
            skLineSegment(sketch, "E366", {"start": v(26.18, 42.3) * mm, "end": v(26.41, 41.95) * mm});
            skLineSegment(sketch, "E367", {"start": v(26.41, 41.95) * mm, "end": v(26.57, 41.6) * mm});
            skLineSegment(sketch, "E368", {"start": v(26.57, 41.6) * mm, "end": v(26.69, 41.4) * mm});
            skLineSegment(sketch, "E369", {"start": v(26.69, 41.4) * mm, "end": v(26.94, 40.97) * mm});
            skLineSegment(sketch, "E370", {"start": v(26.94, 40.97) * mm, "end": v(27.08, 40.68) * mm});
            skLineSegment(sketch, "E371", {"start": v(27.08, 40.68) * mm, "end": v(27.15, 40.5) * mm});
            skLineSegment(sketch, "E372", {"start": v(27.15, 40.5) * mm, "end": v(27.24, 40.29) * mm});
            skLineSegment(sketch, "E373", {"start": v(27.24, 40.29) * mm, "end": v(27.34, 40.07) * mm});
            skLineSegment(sketch, "E374", {"start": v(27.34, 40.07) * mm, "end": v(27.47, 39.8) * mm});
            skLineSegment(sketch, "E375", {"start": v(27.47, 39.8) * mm, "end": v(27.56, 39.59) * mm});
            skLineSegment(sketch, "E376", {"start": v(27.56, 39.59) * mm, "end": v(27.66, 39.37) * mm});
            skLineSegment(sketch, "E377", {"start": v(27.66, 39.37) * mm, "end": v(27.73, 39.2) * mm});
            skLineSegment(sketch, "E378", {"start": v(27.73, 39.2) * mm, "end": v(27.8, 39) * mm});
            skLineSegment(sketch, "E379", {"start": v(27.8, 39) * mm, "end": v(27.85, 38.85) * mm});
            skLineSegment(sketch, "E380", {"start": v(27.85, 38.85) * mm, "end": v(27.97, 38.62) * mm});
            skLineSegment(sketch, "E381", {"start": v(27.97, 38.62) * mm, "end": v(28.08, 38.31) * mm});
            skLineSegment(sketch, "E382", {"start": v(28.08, 38.31) * mm, "end": v(28.2, 38.06) * mm});
            skLineSegment(sketch, "E383", {"start": v(28.2, 38.06) * mm, "end": v(28.26, 37.84) * mm});
            skLineSegment(sketch, "E384", {"start": v(28.26, 37.84) * mm, "end": v(28.38, 37.52) * mm});
            skLineSegment(sketch, "E385", {"start": v(28.38, 37.52) * mm, "end": v(28.45, 37.28) * mm});
            skLineSegment(sketch, "E386", {"start": v(28.45, 37.28) * mm, "end": v(28.53, 37.13) * mm});
            skLineSegment(sketch, "E387", {"start": v(28.53, 37.13) * mm, "end": v(28.6, 36.92) * mm});
            skLineSegment(sketch, "E388", {"start": v(28.6, 36.92) * mm, "end": v(28.68, 36.68) * mm});
            skLineSegment(sketch, "E389", {"start": v(28.68, 36.68) * mm, "end": v(28.8, 36.46) * mm});
            skLineSegment(sketch, "E390", {"start": v(28.8, 36.46) * mm, "end": v(28.87, 36.27) * mm});
            skLineSegment(sketch, "E391", {"start": v(28.87, 36.27) * mm, "end": v(28.95, 36.02) * mm});
            skLineSegment(sketch, "E392", {"start": v(28.95, 36.02) * mm, "end": v(29.02, 35.81) * mm});
            skLineSegment(sketch, "E393", {"start": v(29.02, 35.81) * mm, "end": v(29.13, 35.54) * mm});
            skLineSegment(sketch, "E394", {"start": v(29.13, 35.54) * mm, "end": v(29.2, 35.37) * mm});
            skLineSegment(sketch, "E395", {"start": v(29.2, 35.37) * mm, "end": v(29.39, 34.78) * mm});
            skLineSegment(sketch, "E396", {"start": v(29.39, 34.78) * mm, "end": v(29.45, 34.59) * mm});
            skLineSegment(sketch, "E397", {"start": v(29.45, 34.59) * mm, "end": v(29.52, 34.39) * mm});
            skLineSegment(sketch, "E398", {"start": v(29.52, 34.39) * mm, "end": v(29.58, 34.16) * mm});
            skLineSegment(sketch, "E399", {"start": v(29.58, 34.16) * mm, "end": v(29.65, 33.97) * mm});
            skLineSegment(sketch, "E400", {"start": v(29.65, 33.97) * mm, "end": v(29.7, 33.8) * mm});
            skLineSegment(sketch, "E401", {"start": v(29.7, 33.8) * mm, "end": v(29.8, 33.55) * mm});
            skLineSegment(sketch, "E402", {"start": v(29.8, 33.55) * mm, "end": v(29.9, 33.35) * mm});
            skLineSegment(sketch, "E403", {"start": v(29.9, 33.35) * mm, "end": v(29.96, 33.14) * mm});
            skLineSegment(sketch, "E404", {"start": v(29.96, 33.14) * mm, "end": v(30.04, 33) * mm});
            skLineSegment(sketch, "E405", {"start": v(30.04, 33) * mm, "end": v(30.11, 32.78) * mm});
            skLineSegment(sketch, "E406", {"start": v(30.11, 32.78) * mm, "end": v(30.23, 32.57) * mm});
            skLineSegment(sketch, "E407", {"start": v(30.23, 32.57) * mm, "end": v(30.3, 32.38) * mm});
            skLineSegment(sketch, "E408", {"start": v(30.3, 32.38) * mm, "end": v(30.36, 32.18) * mm});
            skLineSegment(sketch, "E409", {"start": v(30.36, 32.18) * mm, "end": v(30.44, 31.97) * mm});
            skLineSegment(sketch, "E410", {"start": v(30.44, 31.97) * mm, "end": v(30.56, 31.75) * mm});
            skLineSegment(sketch, "E411", {"start": v(30.56, 31.75) * mm, "end": v(30.64, 31.6) * mm});
            skLineSegment(sketch, "E412", {"start": v(30.64, 31.6) * mm, "end": v(30.7, 31.4) * mm});
            skLineSegment(sketch, "E413", {"start": v(30.7, 31.4) * mm, "end": v(30.75, 31.26) * mm});
            skLineSegment(sketch, "E414", {"start": v(30.75, 31.26) * mm, "end": v(30.88, 31.02) * mm});
            skLineSegment(sketch, "E415", {"start": v(30.88, 31.02) * mm, "end": v(30.97, 30.76) * mm});
            skLineSegment(sketch, "E416", {"start": v(30.97, 30.76) * mm, "end": v(31.1, 30.51) * mm});
            skLineSegment(sketch, "E417", {"start": v(31.1, 30.51) * mm, "end": v(31.2, 30.31) * mm});
            skLineSegment(sketch, "E418", {"start": v(31.2, 30.31) * mm, "end": v(31.26, 30.12) * mm});
            skLineSegment(sketch, "E419", {"start": v(31.26, 30.12) * mm, "end": v(31.37, 29.91) * mm});
            skLineSegment(sketch, "E420", {"start": v(31.37, 29.91) * mm, "end": v(31.5, 29.62) * mm});
            skLineSegment(sketch, "E421", {"start": v(31.5, 29.62) * mm, "end": v(31.59, 29.42) * mm});
            skLineSegment(sketch, "E422", {"start": v(31.59, 29.42) * mm, "end": v(31.65, 29.18) * mm});
            skLineSegment(sketch, "E423", {"start": v(31.65, 29.18) * mm, "end": v(31.78, 28.76) * mm});
            skLineSegment(sketch, "E424", {"start": v(31.78, 28.76) * mm, "end": v(31.85, 28.55) * mm});
            skLineSegment(sketch, "E425", {"start": v(31.85, 28.55) * mm, "end": v(31.96, 28.31) * mm});
            skLineSegment(sketch, "E426", {"start": v(31.96, 28.31) * mm, "end": v(32.05, 28.03) * mm});
            skLineSegment(sketch, "E427", {"start": v(32.05, 28.03) * mm, "end": v(32.1, 27.82) * mm});
            skLineSegment(sketch, "E428", {"start": v(32.1, 27.82) * mm, "end": v(32.2, 27.6) * mm});
            skLineSegment(sketch, "E429", {"start": v(32.2, 27.6) * mm, "end": v(32.29, 27.38) * mm});
            skLineSegment(sketch, "E430", {"start": v(32.29, 27.38) * mm, "end": v(32.35, 27.16) * mm});
            skLineSegment(sketch, "E431", {"start": v(32.35, 27.16) * mm, "end": v(32.44, 26.93) * mm});
            skLineSegment(sketch, "E432", {"start": v(32.44, 26.93) * mm, "end": v(32.64, 26.17) * mm});
            skLineSegment(sketch, "E433", {"start": v(32.64, 26.17) * mm, "end": v(32.68, 25.88) * mm});
            skLineSegment(sketch, "E434", {"start": v(32.68, 25.88) * mm, "end": v(32.78, 25.54) * mm});
            skLineSegment(sketch, "E435", {"start": v(32.78, 25.54) * mm, "end": v(32.83, 25.26) * mm});
            skLineSegment(sketch, "E436", {"start": v(32.83, 25.26) * mm, "end": v(32.95, 24.56) * mm});
            skLineSegment(sketch, "E437", {"start": v(32.95, 24.56) * mm, "end": v(33.05, 24.16) * mm});
            skLineSegment(sketch, "E438", {"start": v(33.05, 24.16) * mm, "end": v(33.11, 23.68) * mm});
            skLineSegment(sketch, "E439", {"start": v(33.11, 23.68) * mm, "end": v(33.2, 23.23) * mm});
            skLineSegment(sketch, "E440", {"start": v(33.2, 23.23) * mm, "end": v(33.26, 22.7) * mm});
            skLineSegment(sketch, "E441", {"start": v(33.26, 22.7) * mm, "end": v(33.46, 21.62) * mm});
            skLineSegment(sketch, "E442", {"start": v(33.46, 21.62) * mm, "end": v(33.53, 21.07) * mm});
            skLineSegment(sketch, "E443", {"start": v(33.53, 21.07) * mm, "end": v(33.58, 20.52) * mm});
            skLineSegment(sketch, "E444", {"start": v(33.58, 20.52) * mm, "end": v(33.67, 19.98) * mm});
            skLineSegment(sketch, "E445", {"start": v(33.67, 19.98) * mm, "end": v(33.74, 19.45) * mm});
            skLineSegment(sketch, "E446", {"start": v(33.74, 19.45) * mm, "end": v(33.83, 19) * mm});
            skLineSegment(sketch, "E447", {"start": v(33.83, 19) * mm, "end": v(33.9, 18.58) * mm});
            skLineSegment(sketch, "E448", {"start": v(33.9, 18.58) * mm, "end": v(33.96, 18.08) * mm});
            skLineSegment(sketch, "E449", {"start": v(33.96, 18.08) * mm, "end": v(34.06, 17.59) * mm});
            skLineSegment(sketch, "E450", {"start": v(34.06, 17.59) * mm, "end": v(34.13, 17.3) * mm});
            skLineSegment(sketch, "E451", {"start": v(34.13, 17.3) * mm, "end": v(34.2, 17) * mm});
            skLineSegment(sketch, "E452", {"start": v(34.2, 17) * mm, "end": v(34.3, 16.7) * mm});
            skLineSegment(sketch, "E453", {"start": v(34.3, 16.7) * mm, "end": v(34.35, 16.47) * mm});
            skLineSegment(sketch, "E454", {"start": v(34.35, 16.47) * mm, "end": v(34.43, 16.14) * mm});
            skLineSegment(sketch, "E455", {"start": v(34.43, 16.14) * mm, "end": v(34.5, 15.92) * mm});
            skLineSegment(sketch, "E456", {"start": v(34.5, 15.92) * mm, "end": v(34.59, 15.71) * mm});
            skLineSegment(sketch, "E457", {"start": v(34.59, 15.71) * mm, "end": v(34.67, 15.37) * mm});
            skLineSegment(sketch, "E458", {"start": v(34.67, 15.37) * mm, "end": v(34.75, 15.16) * mm});
            skLineSegment(sketch, "E459", {"start": v(34.75, 15.16) * mm, "end": v(34.89, 14.8) * mm});
            skLineSegment(sketch, "E460", {"start": v(34.89, 14.8) * mm, "end": v(34.94, 14.63) * mm});
            skLineSegment(sketch, "E461", {"start": v(34.94, 14.63) * mm, "end": v(35, 14.48) * mm});
            skLineSegment(sketch, "E462", {"start": v(35, 14.48) * mm, "end": v(35.08, 14.3) * mm});
            skLineSegment(sketch, "E463", {"start": v(35.08, 14.3) * mm, "end": v(35.24, 14.07) * mm});
            skLineSegment(sketch, "E464", {"start": v(35.24, 14.07) * mm, "end": v(35.38, 13.84) * mm});
            skLineSegment(sketch, "E465", {"start": v(35.38, 13.84) * mm, "end": v(35.58, 13.67) * mm});
            skLineSegment(sketch, "E466", {"start": v(35.58, 13.67) * mm, "end": v(35.8, 13.57) * mm});
            skLineSegment(sketch, "E467", {"start": v(35.8, 13.57) * mm, "end": v(35.97, 13.52) * mm});
            skLineSegment(sketch, "E468", {"start": v(35.97, 13.52) * mm, "end": v(36.1, 13.5) * mm});
            skLineSegment(sketch, "E469", {"start": v(36.1, 13.5) * mm, "end": v(36.35, 13.49) * mm});
            skLineSegment(sketch, "E470", {"start": v(36.35, 13.49) * mm, "end": v(36.63, 13.47) * mm});
            skLineSegment(sketch, "E471", {"start": v(36.63, 13.47) * mm, "end": v(36.86, 13.46) * mm});
            skLineSegment(sketch, "E472", {"start": v(36.86, 13.46) * mm, "end": v(37.2, 13.42) * mm});
            skLineSegment(sketch, "E473", {"start": v(37.2, 13.42) * mm, "end": v(37.6, 13.4) * mm});
            skLineSegment(sketch, "E474", {"start": v(37.6, 13.4) * mm, "end": v(37.94, 13.41) * mm});
            skLineSegment(sketch, "E475", {"start": v(37.94, 13.41) * mm, "end": v(38.33, 13.4) * mm});
            skLineSegment(sketch, "E476", {"start": v(38.33, 13.4) * mm, "end": v(38.7, 13.4) * mm});
            skLineSegment(sketch, "E477", {"start": v(38.7, 13.4) * mm, "end": v(39.09, 13.4) * mm});
            skLineSegment(sketch, "E478", {"start": v(39.09, 13.4) * mm, "end": v(39.36, 13.44) * mm});
            skLineSegment(sketch, "E479", {"start": v(39.36, 13.44) * mm, "end": v(39.6, 13.5) * mm});
            skLineSegment(sketch, "E480", {"start": v(39.6, 13.5) * mm, "end": v(39.99, 13.6) * mm});
            skLineSegment(sketch, "E481", {"start": v(39.99, 13.6) * mm, "end": v(40.15, 13.65) * mm});
            skLineSegment(sketch, "E482", {"start": v(40.15, 13.65) * mm, "end": v(40.44, 13.71) * mm});
            skLineSegment(sketch, "E483", {"start": v(40.44, 13.71) * mm, "end": v(40.66, 13.83) * mm});
            skLineSegment(sketch, "E484", {"start": v(40.66, 13.83) * mm, "end": v(40.92, 13.9) * mm});
            skLineSegment(sketch, "E485", {"start": v(40.92, 13.9) * mm, "end": v(41.06, 14.02) * mm});
            skLineSegment(sketch, "E486", {"start": v(41.06, 14.02) * mm, "end": v(41.29, 14.13) * mm});
            skLineSegment(sketch, "E487", {"start": v(41.29, 14.13) * mm, "end": v(41.44, 14.23) * mm});
            skLineSegment(sketch, "E488", {"start": v(41.44, 14.23) * mm, "end": v(41.6, 14.31) * mm});
            skLineSegment(sketch, "E489", {"start": v(41.6, 14.31) * mm, "end": v(41.71, 14.39) * mm});
            skLineSegment(sketch, "E490", {"start": v(41.71, 14.39) * mm, "end": v(41.86, 14.5) * mm});
            skLineSegment(sketch, "E491", {"start": v(41.86, 14.5) * mm, "end": v(42.05, 14.66) * mm});
            skLineSegment(sketch, "E492", {"start": v(42.05, 14.66) * mm, "end": v(42.25, 14.77) * mm});
            skLineSegment(sketch, "E493", {"start": v(42.25, 14.77) * mm, "end": v(42.4, 14.85) * mm});
            skLineSegment(sketch, "E494", {"start": v(42.4, 14.85) * mm, "end": v(42.55, 14.98) * mm});
            skLineSegment(sketch, "E495", {"start": v(42.55, 14.98) * mm, "end": v(42.73, 15.12) * mm});
            skLineSegment(sketch, "E496", {"start": v(42.73, 15.12) * mm, "end": v(42.92, 15.24) * mm});
            skLineSegment(sketch, "E497", {"start": v(42.92, 15.24) * mm, "end": v(43.07, 15.34) * mm});
            skLineSegment(sketch, "E498", {"start": v(43.07, 15.34) * mm, "end": v(43.18, 15.5) * mm});
            skLineSegment(sketch, "E499", {"start": v(43.18, 15.5) * mm, "end": v(43.28, 15.7) * mm});
            skLineSegment(sketch, "E500", {"start": v(43.28, 15.7) * mm, "end": v(43.4, 15.87) * mm});
            skLineSegment(sketch, "E501", {"start": v(43.4, 15.87) * mm, "end": v(43.5, 16.02) * mm});
            skLineSegment(sketch, "E502", {"start": v(43.5, 16.02) * mm, "end": v(43.6, 16.16) * mm});
            skLineSegment(sketch, "E503", {"start": v(43.6, 16.16) * mm, "end": v(43.73, 16.33) * mm});
            skLineSegment(sketch, "E504", {"start": v(43.73, 16.33) * mm, "end": v(43.86, 16.52) * mm});
            skLineSegment(sketch, "E505", {"start": v(43.86, 16.52) * mm, "end": v(44, 16.7) * mm});
            skLineSegment(sketch, "E506", {"start": v(44, 16.7) * mm, "end": v(44.06, 16.84) * mm});
            skLineSegment(sketch, "E507", {"start": v(44.06, 16.84) * mm, "end": v(44.31, 17.28) * mm});
            skLineSegment(sketch, "E508", {"start": v(44.31, 17.28) * mm, "end": v(44.39, 17.4) * mm});
            skLineSegment(sketch, "E509", {"start": v(44.39, 17.4) * mm, "end": v(44.5, 17.53) * mm});
            skLineSegment(sketch, "E510", {"start": v(44.5, 17.53) * mm, "end": v(44.57, 17.69) * mm});
            skLineSegment(sketch, "E511", {"start": v(44.57, 17.69) * mm, "end": v(44.63, 17.82) * mm});
            skLineSegment(sketch, "E512", {"start": v(44.63, 17.82) * mm, "end": v(44.7, 18) * mm});
            skLineSegment(sketch, "E513", {"start": v(44.7, 18) * mm, "end": v(44.79, 18.19) * mm});
            skLineSegment(sketch, "E514", {"start": v(44.79, 18.19) * mm, "end": v(44.88, 18.4) * mm});
            skLineSegment(sketch, "E515", {"start": v(44.88, 18.4) * mm, "end": v(44.96, 18.6) * mm});
            skLineSegment(sketch, "E516", {"start": v(44.96, 18.6) * mm, "end": v(45.04, 18.82) * mm});
            skLineSegment(sketch, "E517", {"start": v(45.04, 18.82) * mm, "end": v(45.12, 19.02) * mm});
            skLineSegment(sketch, "E518", {"start": v(45.12, 19.02) * mm, "end": v(45.16, 19.27) * mm});
            skLineSegment(sketch, "E519", {"start": v(45.16, 19.27) * mm, "end": v(45.22, 19.52) * mm});
            skLineSegment(sketch, "E520", {"start": v(45.22, 19.52) * mm, "end": v(45.35, 19.85) * mm});
            skLineSegment(sketch, "E521", {"start": v(45.35, 19.85) * mm, "end": v(45.4, 20.07) * mm});
            skLineSegment(sketch, "E522", {"start": v(45.4, 20.07) * mm, "end": v(45.51, 20.34) * mm});
            skLineSegment(sketch, "E523", {"start": v(45.51, 20.34) * mm, "end": v(45.57, 20.6) * mm});
            skLineSegment(sketch, "E524", {"start": v(45.57, 20.6) * mm, "end": v(45.6, 20.8) * mm});
            skLineSegment(sketch, "E525", {"start": v(45.6, 20.8) * mm, "end": v(45.66, 21.03) * mm});
            skLineSegment(sketch, "E526", {"start": v(45.66, 21.03) * mm, "end": v(45.7, 21.26) * mm});
            skLineSegment(sketch, "E527", {"start": v(45.7, 21.26) * mm, "end": v(45.73, 21.47) * mm});
            skLineSegment(sketch, "E528", {"start": v(45.73, 21.47) * mm, "end": v(45.77, 21.73) * mm});
            skLineSegment(sketch, "E529", {"start": v(45.77, 21.73) * mm, "end": v(45.87, 22.14) * mm});
            skLineSegment(sketch, "E530", {"start": v(45.87, 22.14) * mm, "end": v(45.96, 22.45) * mm});
            skLineSegment(sketch, "E531", {"start": v(45.96, 22.45) * mm, "end": v(46.03, 22.91) * mm});
            skLineSegment(sketch, "E532", {"start": v(46.03, 22.91) * mm, "end": v(46.17, 23.37) * mm});
            skLineSegment(sketch, "E533", {"start": v(46.17, 23.37) * mm, "end": v(46.23, 23.85) * mm});
            skLineSegment(sketch, "E534", {"start": v(46.23, 23.85) * mm, "end": v(46.3, 24.4) * mm});
            skLineSegment(sketch, "E535", {"start": v(46.3, 24.4) * mm, "end": v(46.38, 24.83) * mm});
            skLineSegment(sketch, "E536", {"start": v(46.38, 24.83) * mm, "end": v(46.45, 25.22) * mm});
            skLineSegment(sketch, "E537", {"start": v(46.45, 25.22) * mm, "end": v(46.52, 25.73) * mm});
            skLineSegment(sketch, "E538", {"start": v(46.52, 25.73) * mm, "end": v(46.61, 26.26) * mm});
            skLineSegment(sketch, "E539", {"start": v(46.61, 26.26) * mm, "end": v(46.72, 26.93) * mm});
            skLineSegment(sketch, "E540", {"start": v(46.72, 26.93) * mm, "end": v(46.83, 27.54) * mm});
            skLineSegment(sketch, "E541", {"start": v(46.83, 27.54) * mm, "end": v(46.83, 28.15) * mm});
            skLineSegment(sketch, "E542", {"start": v(46.83, 28.15) * mm, "end": v(46.91, 29.1) * mm});
            skLineSegment(sketch, "E543", {"start": v(46.91, 29.1) * mm, "end": v(47, 29.56) * mm});
            skLineSegment(sketch, "E544", {"start": v(47, 29.56) * mm, "end": v(47, 29.88) * mm});
            skLineSegment(sketch, "E545", {"start": v(47, 29.88) * mm, "end": v(47, 30.09) * mm});
            skLineSegment(sketch, "E546", {"start": v(47, 30.09) * mm, "end": v(47, 30.26) * mm});
            skLineSegment(sketch, "E547", {"start": v(47, 30.26) * mm, "end": v(46.98, 30.35) * mm});
            skLineSegment(sketch, "E548", {"start": v(46.98, 30.35) * mm, "end": v(46.95, 30.54) * mm});
            skLineSegment(sketch, "E549", {"start": v(46.95, 30.54) * mm, "end": v(46.9, 30.87) * mm});
            skLineSegment(sketch, "E550", {"start": v(46.9, 30.87) * mm, "end": v(46.9, 31.03) * mm});
            skLineSegment(sketch, "E551", {"start": v(46.9, 31.03) * mm, "end": v(46.85, 31.27) * mm});
            skLineSegment(sketch, "E552", {"start": v(46.85, 31.27) * mm, "end": v(46.8, 31.47) * mm});
            skLineSegment(sketch, "E553", {"start": v(46.8, 31.47) * mm, "end": v(46.8, 31.62) * mm});
            skLineSegment(sketch, "E554", {"start": v(46.8, 31.62) * mm, "end": v(46.77, 31.8) * mm});
            skLineSegment(sketch, "E555", {"start": v(46.77, 31.8) * mm, "end": v(46.75, 32.05) * mm});
            skLineSegment(sketch, "E556", {"start": v(46.75, 32.05) * mm, "end": v(46.7, 32.32) * mm});
            skLineSegment(sketch, "E557", {"start": v(46.7, 32.32) * mm, "end": v(46.68, 32.52) * mm});
            skLineSegment(sketch, "E558", {"start": v(46.68, 32.52) * mm, "end": v(46.64, 32.71) * mm});
            skLineSegment(sketch, "E559", {"start": v(46.64, 32.71) * mm, "end": v(46.6, 33) * mm});
            skLineSegment(sketch, "E560", {"start": v(46.6, 33) * mm, "end": v(46.6, 33.16) * mm});
            skLineSegment(sketch, "E561", {"start": v(46.6, 33.16) * mm, "end": v(46.53, 33.4) * mm});
            skLineSegment(sketch, "E562", {"start": v(46.53, 33.4) * mm, "end": v(46.47, 33.6) * mm});
            skLineSegment(sketch, "E563", {"start": v(46.47, 33.6) * mm, "end": v(46.44, 33.73) * mm});
            skLineSegment(sketch, "E564", {"start": v(46.44, 33.73) * mm, "end": v(46.4, 33.94) * mm});
            skLineSegment(sketch, "E565", {"start": v(46.4, 33.94) * mm, "end": v(46.3, 34.19) * mm});
            skLineSegment(sketch, "E566", {"start": v(46.3, 34.19) * mm, "end": v(46.2, 34.35) * mm});
            skLineSegment(sketch, "E567", {"start": v(46.2, 34.35) * mm, "end": v(46.14, 34.53) * mm});
            skLineSegment(sketch, "E568", {"start": v(46.14, 34.53) * mm, "end": v(46.08, 34.72) * mm});
            skLineSegment(sketch, "E569", {"start": v(46.08, 34.72) * mm, "end": v(46.04, 34.9) * mm});
            skLineSegment(sketch, "E570", {"start": v(46.04, 34.9) * mm, "end": v(45.98, 35.07) * mm});
            skLineSegment(sketch, "E571", {"start": v(45.98, 35.07) * mm, "end": v(45.95, 35.16) * mm});
            skLineSegment(sketch, "E572", {"start": v(45.95, 35.16) * mm, "end": v(45.9, 35.31) * mm});
            skLineSegment(sketch, "E573", {"start": v(45.9, 35.31) * mm, "end": v(45.87, 35.43) * mm});
            skLineSegment(sketch, "E574", {"start": v(45.87, 35.43) * mm, "end": v(45.83, 35.57) * mm});
            skLineSegment(sketch, "E575", {"start": v(45.83, 35.57) * mm, "end": v(45.78, 35.7) * mm});
            skLineSegment(sketch, "E576", {"start": v(45.78, 35.7) * mm, "end": v(45.73, 35.83) * mm});
            skLineSegment(sketch, "E577", {"start": v(45.73, 35.83) * mm, "end": v(45.67, 36) * mm});
            skLineSegment(sketch, "E578", {"start": v(45.67, 36) * mm, "end": v(45.6, 36.17) * mm});
            skLineSegment(sketch, "E579", {"start": v(45.6, 36.17) * mm, "end": v(45.53, 36.3) * mm});
            skLineSegment(sketch, "E580", {"start": v(45.53, 36.3) * mm, "end": v(45.49, 36.43) * mm});
            skLineSegment(sketch, "E581", {"start": v(45.49, 36.43) * mm, "end": v(45.42, 36.56) * mm});
            skLineSegment(sketch, "E582", {"start": v(45.42, 36.56) * mm, "end": v(45.39, 36.66) * mm});
            skLineSegment(sketch, "E583", {"start": v(45.39, 36.66) * mm, "end": v(45.32, 36.76) * mm});
            skLineSegment(sketch, "E584", {"start": v(45.32, 36.76) * mm, "end": v(45.3, 36.84) * mm});
            skLineSegment(sketch, "E585", {"start": v(45.3, 36.84) * mm, "end": v(45.22, 37.03) * mm});
            skLineSegment(sketch, "E586", {"start": v(45.22, 37.03) * mm, "end": v(45.15, 37.2) * mm});
            skLineSegment(sketch, "E587", {"start": v(45.15, 37.2) * mm, "end": v(45.05, 37.43) * mm});
            skLineSegment(sketch, "E588", {"start": v(45.05, 37.43) * mm, "end": v(44.92, 37.59) * mm});
            skLineSegment(sketch, "E589", {"start": v(44.92, 37.59) * mm, "end": v(44.84, 37.72) * mm});
            skLineSegment(sketch, "E590", {"start": v(44.84, 37.72) * mm, "end": v(44.76, 37.89) * mm});
            skLineSegment(sketch, "E591", {"start": v(44.76, 37.89) * mm, "end": v(44.72, 37.98) * mm});
            skLineSegment(sketch, "E592", {"start": v(44.72, 37.98) * mm, "end": v(44.66, 38.1) * mm});
            skLineSegment(sketch, "E593", {"start": v(44.66, 38.1) * mm, "end": v(44.59, 38.22) * mm});
            skLineSegment(sketch, "E594", {"start": v(44.59, 38.22) * mm, "end": v(44.54, 38.33) * mm});
            skLineSegment(sketch, "E595", {"start": v(44.54, 38.33) * mm, "end": v(44.46, 38.45) * mm});
            skLineSegment(sketch, "E596", {"start": v(43.65, 39.8) * mm, "end": v(43.56, 39.93) * mm});
            skLineSegment(sketch, "E597", {"start": v(43.56, 39.93) * mm, "end": v(43.5, 40.1) * mm});
            skLineSegment(sketch, "E598", {"start": v(43.5, 40.1) * mm, "end": v(43.4, 40.27) * mm});
            skLineSegment(sketch, "E599", {"start": v(43.4, 40.27) * mm, "end": v(43.34, 40.38) * mm});
            skLineSegment(sketch, "E600", {"start": v(43.34, 40.38) * mm, "end": v(43.3, 40.48) * mm});
            skLineSegment(sketch, "E601", {"start": v(43.3, 40.48) * mm, "end": v(43.23, 40.56) * mm});
            skLineSegment(sketch, "E602", {"start": v(43.23, 40.56) * mm, "end": v(43.15, 40.73) * mm});
            skLineSegment(sketch, "E603", {"start": v(43.15, 40.73) * mm, "end": v(43.1, 40.84) * mm});
            skLineSegment(sketch, "E604", {"start": v(43.1, 40.84) * mm, "end": v(43.06, 40.93) * mm});
            skLineSegment(sketch, "E605", {"start": v(43.06, 40.93) * mm, "end": v(43, 41.08) * mm});
            skLineSegment(sketch, "E606", {"start": v(43, 41.08) * mm, "end": v(42.9, 41.26) * mm});
            skLineSegment(sketch, "E607", {"start": v(42.9, 41.26) * mm, "end": v(42.82, 41.43) * mm});
            skLineSegment(sketch, "E608", {"start": v(42.82, 41.43) * mm, "end": v(42.66, 41.63) * mm});
            skLineSegment(sketch, "E609", {"start": v(42.66, 41.63) * mm, "end": v(42.55, 41.76) * mm});
            skLineSegment(sketch, "E610", {"start": v(42.55, 41.76) * mm, "end": v(42.48, 41.9) * mm});
            skLineSegment(sketch, "E611", {"start": v(42.48, 41.9) * mm, "end": v(42.35, 42) * mm});
            skLineSegment(sketch, "E612", {"start": v(42.35, 42) * mm, "end": v(42.19, 42.15) * mm});
            skLineSegment(sketch, "E613", {"start": v(42.19, 42.15) * mm, "end": v(42.06, 42.25) * mm});
            skLineSegment(sketch, "E614", {"start": v(42.06, 42.25) * mm, "end": v(41.95, 42.34) * mm});
            skLineSegment(sketch, "E615", {"start": v(41.95, 42.34) * mm, "end": v(41.55, 42.64) * mm});
            skLineSegment(sketch, "E616", {"start": v(41.55, 42.64) * mm, "end": v(41.4, 42.72) * mm});
            skLineSegment(sketch, "E617", {"start": v(41.4, 42.72) * mm, "end": v(41.28, 42.8) * mm});
            skLineSegment(sketch, "E618", {"start": v(41.28, 42.8) * mm, "end": v(41.14, 42.9) * mm});
            skLineSegment(sketch, "E619", {"start": v(41.14, 42.9) * mm, "end": v(41.01, 42.98) * mm});
            skLineSegment(sketch, "E620", {"start": v(41.01, 42.98) * mm, "end": v(40.87, 43.06) * mm});
            skLineSegment(sketch, "E621", {"start": v(40.87, 43.06) * mm, "end": v(40.63, 43.18) * mm});
            skLineSegment(sketch, "E622", {"start": v(40.63, 43.18) * mm, "end": v(40.47, 43.28) * mm});
            skLineSegment(sketch, "E623", {"start": v(40.47, 43.28) * mm, "end": v(40.34, 43.34) * mm});
            skLineSegment(sketch, "E624", {"start": v(40.34, 43.34) * mm, "end": v(40.21, 43.41) * mm});
            skLineSegment(sketch, "E625", {"start": v(40.21, 43.41) * mm, "end": v(40.03, 43.5) * mm});
            skLineSegment(sketch, "E626", {"start": v(40.03, 43.5) * mm, "end": v(39.84, 43.6) * mm});
            skLineSegment(sketch, "E627", {"start": v(39.84, 43.6) * mm, "end": v(39.59, 43.71) * mm});
            skLineSegment(sketch, "E628", {"start": v(39.59, 43.71) * mm, "end": v(39.33, 43.86) * mm});
            skLineSegment(sketch, "E629", {"start": v(39.33, 43.86) * mm, "end": v(39.1, 43.97) * mm});
            skLineSegment(sketch, "E630", {"start": v(39.1, 43.97) * mm, "end": v(38.9, 44.05) * mm});
            skLineSegment(sketch, "E631", {"start": v(38.9, 44.05) * mm, "end": v(38.78, 44.14) * mm});
            skLineSegment(sketch, "E632", {"start": v(38.78, 44.14) * mm, "end": v(38.57, 44.23) * mm});
            skLineSegment(sketch, "E633", {"start": v(38.57, 44.23) * mm, "end": v(38.44, 44.32) * mm});
            skLineSegment(sketch, "E634", {"start": v(38.44, 44.32) * mm, "end": v(38.23, 44.42) * mm});
            skLineSegment(sketch, "E635", {"start": v(38.23, 44.42) * mm, "end": v(38.06, 44.51) * mm});
            skLineSegment(sketch, "E636", {"start": v(38.06, 44.51) * mm, "end": v(37.84, 44.6) * mm});
            skLineSegment(sketch, "E637", {"start": v(37.84, 44.6) * mm, "end": v(37.71, 44.68) * mm});
            skLineSegment(sketch, "E638", {"start": v(37.71, 44.68) * mm, "end": v(37.49, 44.8) * mm});
            skLineSegment(sketch, "E639", {"start": v(37.49, 44.8) * mm, "end": v(37.22, 44.96) * mm});
            skLineSegment(sketch, "E640", {"start": v(37.22, 44.96) * mm, "end": v(37.05, 45.05) * mm});
            skLineSegment(sketch, "E641", {"start": v(37.05, 45.05) * mm, "end": v(36.85, 45.14) * mm});
            skLineSegment(sketch, "E642", {"start": v(36.85, 45.14) * mm, "end": v(36.65, 45.23) * mm});
            skLineSegment(sketch, "E643", {"start": v(36.65, 45.23) * mm, "end": v(36.48, 45.31) * mm});
            skLineSegment(sketch, "E644", {"start": v(36.48, 45.31) * mm, "end": v(36.36, 45.4) * mm});
            skLineSegment(sketch, "E645", {"start": v(36.36, 45.4) * mm, "end": v(36.2, 45.47) * mm});
            skLineSegment(sketch, "E646", {"start": v(36.2, 45.47) * mm, "end": v(36, 45.55) * mm});
            skLineSegment(sketch, "E647", {"start": v(36, 45.55) * mm, "end": v(35.9, 45.6) * mm});
            skLineSegment(sketch, "E648", {"start": v(35.9, 45.6) * mm, "end": v(35.77, 45.7) * mm});
            skLineSegment(sketch, "E649", {"start": v(35.77, 45.7) * mm, "end": v(35.56, 45.8) * mm});
            skLineSegment(sketch, "E650", {"start": v(35.56, 45.8) * mm, "end": v(35.35, 45.9) * mm});
            skLineSegment(sketch, "E651", {"start": v(35.35, 45.9) * mm, "end": v(35.21, 46) * mm});
            skLineSegment(sketch, "E652", {"start": v(35.21, 46) * mm, "end": v(34.95, 46.13) * mm});
            skLineSegment(sketch, "E653", {"start": v(34.95, 46.13) * mm, "end": v(34.86, 46.23) * mm});
            skLineSegment(sketch, "E654", {"start": v(34.86, 46.23) * mm, "end": v(34.65, 46.35) * mm});
            skLineSegment(sketch, "E655", {"start": v(34.65, 46.35) * mm, "end": v(34.48, 46.44) * mm});
            skLineSegment(sketch, "E656", {"start": v(34.48, 46.44) * mm, "end": v(34.17, 46.6) * mm});
            skLineSegment(sketch, "E657", {"start": v(34.17, 46.6) * mm, "end": v(34.01, 46.73) * mm});
            skLineSegment(sketch, "E658", {"start": v(34.01, 46.73) * mm, "end": v(33.8, 46.83) * mm});
            skLineSegment(sketch, "E659", {"start": v(33.8, 46.83) * mm, "end": v(33.63, 46.94) * mm});
            skLineSegment(sketch, "E660", {"start": v(33.63, 46.94) * mm, "end": v(33.46, 47.07) * mm});
            skLineSegment(sketch, "E661", {"start": v(33.46, 47.07) * mm, "end": v(33.21, 47.22) * mm});
            skLineSegment(sketch, "E662", {"start": v(33.21, 47.22) * mm, "end": v(32.85, 47.39) * mm});
            skLineSegment(sketch, "E663", {"start": v(32.85, 47.39) * mm, "end": v(32.54, 47.58) * mm});
            skLineSegment(sketch, "E664", {"start": v(32.54, 47.58) * mm, "end": v(32.3, 47.78) * mm});
            skLineSegment(sketch, "E665", {"start": v(32.3, 47.78) * mm, "end": v(32.12, 47.87) * mm});
            skLineSegment(sketch, "E666", {"start": v(32.12, 47.87) * mm, "end": v(32, 47.92) * mm});
            skLineSegment(sketch, "E667", {"start": v(32, 47.92) * mm, "end": v(31.7, 48.03) * mm});
            skLineSegment(sketch, "E668", {"start": v(31.7, 48.03) * mm, "end": v(31.52, 48.16) * mm});
            skLineSegment(sketch, "E669", {"start": v(31.52, 48.16) * mm, "end": v(31.34, 48.23) * mm});
            skLineSegment(sketch, "E670", {"start": v(31.34, 48.23) * mm, "end": v(31.17, 48.33) * mm});
            skLineSegment(sketch, "E671", {"start": v(31.17, 48.33) * mm, "end": v(30.92, 48.44) * mm});
            skLineSegment(sketch, "E672", {"start": v(30.92, 48.44) * mm, "end": v(30.62, 48.58) * mm});
            skLineSegment(sketch, "E673", {"start": v(30.62, 48.58) * mm, "end": v(30.42, 48.68) * mm});
            skLineSegment(sketch, "E674", {"start": v(30.42, 48.68) * mm, "end": v(30.25, 48.75) * mm});
            skLineSegment(sketch, "E675", {"start": v(30.25, 48.75) * mm, "end": v(29.92, 48.91) * mm});
            skLineSegment(sketch, "E676", {"start": v(29.92, 48.91) * mm, "end": v(29.46, 49.15) * mm});
            skLineSegment(sketch, "E677", {"start": v(29.46, 49.15) * mm, "end": v(29.34, 49.22) * mm});
            skLineSegment(sketch, "E678", {"start": v(29.34, 49.22) * mm, "end": v(29.19, 49.29) * mm});
            skLineSegment(sketch, "E679", {"start": v(29.19, 49.29) * mm, "end": v(29, 49.37) * mm});
            skLineSegment(sketch, "E680", {"start": v(29, 49.37) * mm, "end": v(28.85, 49.45) * mm});
            skLineSegment(sketch, "E681", {"start": v(28.85, 49.45) * mm, "end": v(28.61, 49.6) * mm});
            skLineSegment(sketch, "E682", {"start": v(28.61, 49.6) * mm, "end": v(28.45, 49.66) * mm});
            skLineSegment(sketch, "E683", {"start": v(28.45, 49.66) * mm, "end": v(28.3, 49.74) * mm});
            skLineSegment(sketch, "E684", {"start": v(28.3, 49.74) * mm, "end": v(28.12, 49.82) * mm});
            skLineSegment(sketch, "E685", {"start": v(28.12, 49.82) * mm, "end": v(27.85, 49.95) * mm});
            skLineSegment(sketch, "E686", {"start": v(27.85, 49.95) * mm, "end": v(27.61, 50.08) * mm});
            skLineSegment(sketch, "E687", {"start": v(27.61, 50.08) * mm, "end": v(27.4, 50.19) * mm});
            skLineSegment(sketch, "E688", {"start": v(27.4, 50.19) * mm, "end": v(27.16, 50.3) * mm});
            skLineSegment(sketch, "E689", {"start": v(27.16, 50.3) * mm, "end": v(26.9, 50.45) * mm});
            skLineSegment(sketch, "E690", {"start": v(26.9, 50.45) * mm, "end": v(26.51, 50.64) * mm});
            skLineSegment(sketch, "E691", {"start": v(26.51, 50.64) * mm, "end": v(26.31, 50.79) * mm});
            skLineSegment(sketch, "E692", {"start": v(26.31, 50.79) * mm, "end": v(26.15, 50.86) * mm});
            skLineSegment(sketch, "E693", {"start": v(26.15, 50.86) * mm, "end": v(25.86, 51.02) * mm});
            skLineSegment(sketch, "E694", {"start": v(25.86, 51.02) * mm, "end": v(25.55, 51.2) * mm});
            skLineSegment(sketch, "E695", {"start": v(25.55, 51.2) * mm, "end": v(25.34, 51.3) * mm});
            skLineSegment(sketch, "E696", {"start": v(25.34, 51.3) * mm, "end": v(25.06, 51.48) * mm});
            skLineSegment(sketch, "E697", {"start": v(25.06, 51.48) * mm, "end": v(24.88, 51.62) * mm});
            skLineSegment(sketch, "E698", {"start": v(24.88, 51.62) * mm, "end": v(24.7, 51.78) * mm});
            skLineSegment(sketch, "E699", {"start": v(24.7, 51.78) * mm, "end": v(24.44, 51.93) * mm});
            skLineSegment(sketch, "E700", {"start": v(24.44, 51.93) * mm, "end": v(24.23, 52.09) * mm});
            skLineSegment(sketch, "E701", {"start": v(24.23, 52.09) * mm, "end": v(24.02, 52.23) * mm});
            skLineSegment(sketch, "E702", {"start": v(24.02, 52.23) * mm, "end": v(23.8, 52.4) * mm});
            skLineSegment(sketch, "E703", {"start": v(23.8, 52.4) * mm, "end": v(23.61, 52.55) * mm});
            skLineSegment(sketch, "E704", {"start": v(23.61, 52.55) * mm, "end": v(23.45, 52.72) * mm});
            skLineSegment(sketch, "E705", {"start": v(23.45, 52.72) * mm, "end": v(23.34, 52.85) * mm});
            skLineSegment(sketch, "E706", {"start": v(23.34, 52.85) * mm, "end": v(23.16, 53) * mm});
            skLineSegment(sketch, "E707", {"start": v(23.16, 53) * mm, "end": v(22.95, 53.14) * mm});
            skLineSegment(sketch, "E708", {"start": v(22.95, 53.14) * mm, "end": v(22.8, 53.28) * mm});
            skLineSegment(sketch, "E709", {"start": v(22.8, 53.28) * mm, "end": v(22.72, 53.4) * mm});
            skLineSegment(sketch, "E710", {"start": v(22.72, 53.4) * mm, "end": v(22.59, 53.6) * mm});
            skLineSegment(sketch, "E711", {"start": v(22.59, 53.6) * mm, "end": v(22.46, 53.72) * mm});
            skLineSegment(sketch, "E712", {"start": v(22.46, 53.72) * mm, "end": v(22.37, 53.87) * mm});
            skLineSegment(sketch, "E713", {"start": v(22.37, 53.87) * mm, "end": v(22.25, 54) * mm});
            skLineSegment(sketch, "E714", {"start": v(22.25, 54) * mm, "end": v(22.1, 54.2) * mm});
            skLineSegment(sketch, "E715", {"start": v(22.1, 54.2) * mm, "end": v(21.93, 54.44) * mm});
            skLineSegment(sketch, "E716", {"start": v(21.93, 54.44) * mm, "end": v(21.87, 54.55) * mm});
            skLineSegment(sketch, "E717", {"start": v(21.87, 54.55) * mm, "end": v(21.8, 54.68) * mm});
            skLineSegment(sketch, "E718", {"start": v(21.8, 54.68) * mm, "end": v(21.69, 54.84) * mm});
            skLineSegment(sketch, "E719", {"start": v(21.69, 54.84) * mm, "end": v(21.66, 54.93) * mm});
            skLineSegment(sketch, "E720", {"start": v(21.66, 54.93) * mm, "end": v(21.6, 55.06) * mm});
            skLineSegment(sketch, "E721", {"start": v(21.6, 55.06) * mm, "end": v(21.54, 55.2) * mm});
            skLineSegment(sketch, "E722", {"start": v(21.54, 55.2) * mm, "end": v(21.44, 55.4) * mm});
            skLineSegment(sketch, "E723", {"start": v(21.44, 55.4) * mm, "end": v(21.34, 55.54) * mm});
            skLineSegment(sketch, "E724", {"start": v(21.34, 55.54) * mm, "end": v(21.21, 55.7) * mm});
            skLineSegment(sketch, "E725", {"start": v(21.21, 55.7) * mm, "end": v(21.1, 55.89) * mm});
            skLineSegment(sketch, "E726", {"start": v(21.1, 55.89) * mm, "end": v(21, 56.02) * mm});
            skLineSegment(sketch, "E727", {"start": v(21, 56.02) * mm, "end": v(20.94, 56.17) * mm});
            skLineSegment(sketch, "E728", {"start": v(20.94, 56.17) * mm, "end": v(20.9, 56.26) * mm});
            skLineSegment(sketch, "E729", {"start": v(20.9, 56.26) * mm, "end": v(20.86, 56.34) * mm});
            skLineSegment(sketch, "E730", {"start": v(20.86, 56.34) * mm, "end": v(20.83, 56.51) * mm});
            skLineSegment(sketch, "E731", {"start": v(20.83, 56.51) * mm, "end": v(20.8, 56.62) * mm});
            skLineSegment(sketch, "E732", {"start": v(20.8, 56.62) * mm, "end": v(20.8, 56.73) * mm});
            skLineSegment(sketch, "E733", {"start": v(20.8, 56.73) * mm, "end": v(20.76, 56.85) * mm});
            skLineSegment(sketch, "E734", {"start": v(20.76, 56.85) * mm, "end": v(20.72, 56.97) * mm});
            skLineSegment(sketch, "E735", {"start": v(20.72, 56.97) * mm, "end": v(20.74, 57.03) * mm});
            skLineSegment(sketch, "E736", {"start": v(20.74, 57.03) * mm, "end": v(20.68, 57.32) * mm});
            skLineSegment(sketch, "E737", {"start": v(20.68, 57.32) * mm, "end": v(20.61, 57.66) * mm});
            skLineSegment(sketch, "E738", {"start": v(20.61, 57.66) * mm, "end": v(20.55, 57.9) * mm});
            skLineSegment(sketch, "E739", {"start": v(20.55, 57.9) * mm, "end": v(20.52, 58.18) * mm});
            skLineSegment(sketch, "E740", {"start": v(20.52, 58.18) * mm, "end": v(20.46, 58.48) * mm});
            skLineSegment(sketch, "E741", {"start": v(20.46, 58.48) * mm, "end": v(20.4, 58.86) * mm});
            skLineSegment(sketch, "E742", {"start": v(20.4, 58.86) * mm, "end": v(20.38, 59.13) * mm});
            skLineSegment(sketch, "E743", {"start": v(20.38, 59.13) * mm, "end": v(20.33, 59.32) * mm});
            skLineSegment(sketch, "E744", {"start": v(20.33, 59.32) * mm, "end": v(20.3, 59.77) * mm});
            skLineSegment(sketch, "E745", {"start": v(20.3, 59.77) * mm, "end": v(20.27, 59.95) * mm});
            skLineSegment(sketch, "E746", {"start": v(20.27, 59.95) * mm, "end": v(20.23, 60.1) * mm});
            skLineSegment(sketch, "E747", {"start": v(20.23, 60.1) * mm, "end": v(20.17, 60.32) * mm});
            skLineSegment(sketch, "E748", {"start": v(20.17, 60.32) * mm, "end": v(20.12, 60.61) * mm});
            skLineSegment(sketch, "E749", {"start": v(20.12, 60.61) * mm, "end": v(20.08, 60.93) * mm});
            skLineSegment(sketch, "E750", {"start": v(20.08, 60.93) * mm, "end": v(20.04, 61.23) * mm});
            skLineSegment(sketch, "E751", {"start": v(20.04, 61.23) * mm, "end": v(20, 61.6) * mm});
            skLineSegment(sketch, "E752", {"start": v(20, 61.6) * mm, "end": v(19.99, 61.8) * mm});
            skLineSegment(sketch, "E753", {"start": v(19.99, 61.8) * mm, "end": v(19.99, 62.01) * mm});
            skLineSegment(sketch, "E754", {"start": v(19.99, 62.01) * mm, "end": v(19.99, 62.25) * mm});
            skLineSegment(sketch, "E755", {"start": v(19.99, 62.25) * mm, "end": v(20.02, 62.45) * mm});
            skLineSegment(sketch, "E756", {"start": v(20.02, 62.45) * mm, "end": v(20.02, 62.79) * mm});
            skLineSegment(sketch, "E757", {"start": v(20.02, 62.79) * mm, "end": v(20.07, 63.08) * mm});
            skLineSegment(sketch, "E758", {"start": v(20.07, 63.08) * mm, "end": v(20.1, 63.3) * mm});
            skLineSegment(sketch, "E759", {"start": v(20.1, 63.3) * mm, "end": v(20.14, 63.52) * mm});
            skLineSegment(sketch, "E760", {"start": v(20.14, 63.52) * mm, "end": v(20.17, 63.74) * mm});
            skLineSegment(sketch, "E761", {"start": v(20.17, 63.74) * mm, "end": v(20.22, 63.95) * mm});
            skLineSegment(sketch, "E762", {"start": v(20.22, 63.95) * mm, "end": v(20.24, 64.1) * mm});
            skLineSegment(sketch, "E763", {"start": v(20.24, 64.1) * mm, "end": v(20.28, 64.34) * mm});
            skLineSegment(sketch, "E764", {"start": v(20.28, 64.34) * mm, "end": v(20.35, 64.62) * mm});
            skLineSegment(sketch, "E765", {"start": v(20.35, 64.62) * mm, "end": v(20.54, 65.26) * mm});
            skLineSegment(sketch, "E766", {"start": v(20.54, 65.26) * mm, "end": v(20.6, 65.43) * mm});
            skLineSegment(sketch, "E767", {"start": v(20.6, 65.43) * mm, "end": v(20.63, 65.54) * mm});
            skLineSegment(sketch, "E768", {"start": v(20.63, 65.54) * mm, "end": v(20.7, 65.68) * mm});
            skLineSegment(sketch, "E769", {"start": v(20.7, 65.68) * mm, "end": v(20.77, 65.86) * mm});
            skLineSegment(sketch, "E770", {"start": v(20.77, 65.86) * mm, "end": v(20.81, 65.94) * mm});
            skLineSegment(sketch, "E771", {"start": v(20.81, 65.94) * mm, "end": v(20.86, 66.01) * mm});
            skLineSegment(sketch, "E772", {"start": v(20.86, 66.01) * mm, "end": v(20.92, 66.12) * mm});
            skLineSegment(sketch, "E773", {"start": v(20.92, 66.12) * mm, "end": v(20.99, 66.23) * mm});
            skLineSegment(sketch, "E774", {"start": v(20.99, 66.23) * mm, "end": v(21.06, 66.35) * mm});
            skLineSegment(sketch, "E775", {"start": v(21.06, 66.35) * mm, "end": v(21.12, 66.48) * mm});
            skLineSegment(sketch, "E776", {"start": v(21.12, 66.48) * mm, "end": v(21.18, 66.6) * mm});
            skLineSegment(sketch, "E777", {"start": v(21.18, 66.6) * mm, "end": v(21.22, 66.7) * mm});
            skLineSegment(sketch, "E778", {"start": v(21.22, 66.7) * mm, "end": v(21.28, 66.86) * mm});
            skLineSegment(sketch, "E779", {"start": v(21.28, 66.86) * mm, "end": v(21.35, 67) * mm});
            skLineSegment(sketch, "E780", {"start": v(21.35, 67) * mm, "end": v(21.39, 67.1) * mm});
            skLineSegment(sketch, "E781", {"start": v(21.39, 67.1) * mm, "end": v(21.43, 67.22) * mm});
            skLineSegment(sketch, "E782", {"start": v(21.43, 67.22) * mm, "end": v(21.52, 67.37) * mm});
            skLineSegment(sketch, "E783", {"start": v(21.52, 67.37) * mm, "end": v(21.6, 67.58) * mm});
            skLineSegment(sketch, "E784", {"start": v(21.6, 67.58) * mm, "end": v(21.64, 67.66) * mm});
            skLineSegment(sketch, "E785", {"start": v(21.64, 67.66) * mm, "end": v(21.67, 67.74) * mm});
            skLineSegment(sketch, "E786", {"start": v(21.67, 67.74) * mm, "end": v(21.69, 67.79) * mm});
            skLineSegment(sketch, "E787", {"start": v(21.69, 67.79) * mm, "end": v(21.72, 67.88) * mm});
            skLineSegment(sketch, "E788", {"start": v(21.72, 67.88) * mm, "end": v(21.75, 67.95) * mm});
            skLineSegment(sketch, "E789", {"start": v(21.75, 67.95) * mm, "end": v(21.77, 68.03) * mm});
            skArc(sketch, "E790.filletArc", {"start": v(21.99, 68.15) * mm, "mid": v(21.85, 68.14) * mm, "end": v(21.77, 68.03) * mm});
            skFitSpline(sketch, "E791", {"points": [v(29.2, 64.92) * mm, v(29.78, 64.62) * mm, v(31.16, 64.07) * mm], "startDerivative": vector(1.28, -0.73) * mm, "endDerivative": vector(2.55, -0.97) * mm});
            skFitSpline(sketch, "E792", {"points": [v(43.56, 39.93) * mm, v(43.95, 39.33) * mm, v(44.46, 38.45) * mm], "startDerivative": vector(0.82, -1.25) * mm, "endDerivative": vector(0.97, -1.7) * mm});
            skArc(sketch, "E793", {"start": v(52.83, 15.96) * mm, "mid": v(54.28, 19.62) * mm, "end": v(55.48, 23.38) * mm});
            skLineSegment(sketch, "E794", {"start": v(46.9, 9.9) * mm, "end": v(45.98, 9.4) * mm});
            skArc(sketch, "E795", {"start": v(37.68, 6.67) * mm, "mid": v(38.66, 6.82) * mm, "end": v(39.64, 7.05) * mm});
            skSolve(sketch);
        }
        {
            var Q0;
            Q0 = qSketchRegion(id + "F0", true);
            extrude(context, id + "F1", {"entities" : qUnion([Q0]), "depth" : 4.32 * mm, "offsetDistance" : 25.4 * mm});
        }
        {
            var Q0;
            Q0=makeQuery(id+"F1.opExtrude","SWEPT_EDGE",EDGE,{"disambiguationData":[OSD([sQuery(id+"F0.wireOp",EDGE,"E32"),sQuery(id+"F0.wireOp",EDGE,"E33")])]});
            chamfer(context, id + "F2", {"entities" : qUnion([Q0]), "width" : 1.3 * mm, "tangentPropagation" : true});
        }
        {
            var Q0;
            Q0=makeQuery(id+"F1.opExtrude","SWEPT_EDGE",EDGE,{"disambiguationData":[OSD([sQuery(id+"F0.wireOp",EDGE,"E23"),sQuery(id+"F0.wireOp",EDGE,"E24")])]});
            fillet(context, id + "F3", {"entities" : qUnion([Q0]), "radius" : 57.2 * mm, "tangentPropagation" : true, "allowEdgeOverflow" : false});
        }
        {
            var Q0;
            Q0=makeQuery(id+"F3.opFillet","BLEND_EDGE",EDGE,{"blendedFrom":[makeQuery(id+"F1.opExtrude","SWEPT_EDGE",EDGE,{"disambiguationData":[OSD([sQuery(id+"F0.wireOp",EDGE,"E23"),sQuery(id+"F0.wireOp",EDGE,"E24")])]}),makeQuery(id+"F1.opExtrude","SWEPT_FACE",FACE,{"disambiguationData":[OSD([sQuery(id+"F0.wireOp",EDGE,"E25")])]})],"blendedInto":[makeQuery(id+"F1.opExtrude","SWEPT_FACE",FACE,{"disambiguationData":[OSD([sQuery(id+"F0.wireOp",EDGE,"E25")])]})]});
            fillet(context, id + "F4", {"entities" : qUnion([Q0]), "radius" : 17.43 * mm, "tangentPropagation" : true, "allowEdgeOverflow" : false});
        }
        {
            var Q0;
            Q0=makeQuery(id+"F4.opFillet","BLEND_EDGE",EDGE,{"blendedFrom":[makeQuery(id+"F3.opFillet","BLEND_EDGE",EDGE,{"blendedFrom":[makeQuery(id+"F1.opExtrude","SWEPT_EDGE",EDGE,{"disambiguationData":[OSD([sQuery(id+"F0.wireOp",EDGE,"E23"),sQuery(id+"F0.wireOp",EDGE,"E24")])]}),makeQuery(id+"F1.opExtrude","SWEPT_FACE",FACE,{"disambiguationData":[OSD([sQuery(id+"F0.wireOp",EDGE,"E25")])]})],"blendedInto":[makeQuery(id+"F1.opExtrude","SWEPT_FACE",FACE,{"disambiguationData":[OSD([sQuery(id+"F0.wireOp",EDGE,"E25")])]})]}),makeQuery(id+"F1.opExtrude","SWEPT_FACE",FACE,{"disambiguationData":[OSD([sQuery(id+"F0.wireOp",EDGE,"E26")])]})],"blendedInto":[makeQuery(id+"F1.opExtrude","SWEPT_FACE",FACE,{"disambiguationData":[OSD([sQuery(id+"F0.wireOp",EDGE,"E26")])]})]});
            fillet(context, id + "F5", {"entities" : qUnion([Q0]), "radius" : 10.05 * mm, "tangentPropagation" : true, "allowEdgeOverflow" : false});
        }
        {
            var Q0;
            Q0=makeQuery(id+"F1.opExtrude","SWEPT_EDGE",EDGE,{"disambiguationData":[OSD([sQuery(id+"F0.wireOp",EDGE,"E28"),sQuery(id+"F0.wireOp",EDGE,"E29")])]});
            fillet(context, id + "F6", {"entities" : qUnion([Q0]), "radius" : 8.32 * mm, "tangentPropagation" : true, "allowEdgeOverflow" : false});
        }
        {
            var Q0;
            Q0=qCreatedBy(makeId("Top.planeOp"),FACE);
            var sketch = newSketch(context, id + "F7", { "sketchPlane" : qUnion([Q0])});
            skLineSegment(sketch, "E796", {"start": v(28.38, 59.52) * mm, "end": v(28.14, 59.18) * mm});
            skLineSegment(sketch, "E797", {"start": v(28.3, 56.52) * mm, "end": v(28.31, 56.51) * mm});
            skLineSegment(sketch, "E798", {"start": v(27.25, 58.18) * mm, "end": v(27.24, 58.17) * mm});
            skLineSegment(sketch, "E799", {"start": v(29.24, 56.21) * mm, "end": v(29.25, 56.2) * mm});
            skLineSegment(sketch, "E800", {"start": v(26.68, 57.95) * mm, "end": v(26.67, 57.94) * mm});
            skLineSegment(sketch, "E801", {"start": v(29.75, 56.21) * mm, "end": v(30.2, 56.29) * mm});
            skLineSegment(sketch, "E802", {"start": v(29.54, 58.83) * mm, "end": v(29.49, 58.86) * mm});
            skLineSegment(sketch, "E803", {"start": v(26.96, 57.32) * mm, "end": v(27, 57.3) * mm});
            skLineSegment(sketch, "E804", {"start": v(39.9, 53.84) * mm, "end": v(40.04, 54.07) * mm});
            skLineSegment(sketch, "E805", {"start": v(29.05, 55.8) * mm, "end": v(28.84, 55.79) * mm});
            skLineSegment(sketch, "E806", {"start": v(30.24, 56.17) * mm, "end": v(30.23, 56.14) * mm});
            skLineSegment(sketch, "E807", {"start": v(37.94, 50.87) * mm, "end": v(37.93, 50.9) * mm});
            skLineSegment(sketch, "E808", {"start": v(26.1, 62.15) * mm, "end": v(26.29, 62.37) * mm});
            skLineSegment(sketch, "E809", {"start": v(38.27, 55.83) * mm, "end": v(38.26, 55.87) * mm});
            skLineSegment(sketch, "E810", {"start": v(26.61, 61.84) * mm, "end": v(26.6, 61.82) * mm});
            skLineSegment(sketch, "E811", {"start": v(28.45, 62.67) * mm, "end": v(28.44, 62.67) * mm});
            skLineSegment(sketch, "E812", {"start": v(26.07, 58.18) * mm, "end": v(26.17, 58.2) * mm});
            skLineSegment(sketch, "E813", {"start": v(27.76, 56.07) * mm, "end": v(27.73, 56.08) * mm});
            skLineSegment(sketch, "E814", {"start": v(38.72, 52.23) * mm, "end": v(38.73, 52.25) * mm});
            skLineSegment(sketch, "E815", {"start": v(29.97, 55.95) * mm, "end": v(29.88, 55.92) * mm});
            skLineSegment(sketch, "E816", {"start": v(25.45, 60.9) * mm, "end": v(25.46, 60.93) * mm});
            skLineSegment(sketch, "E817", {"start": v(27.37, 62.64) * mm, "end": v(27.36, 62.64) * mm});
            skLineSegment(sketch, "E818", {"start": v(27.34, 59.4) * mm, "end": v(27.35, 59.42) * mm});
            skLineSegment(sketch, "E819", {"start": v(33.87, 58.22) * mm, "end": v(33.84, 58.26) * mm});
            skLineSegment(sketch, "E820", {"start": v(33.2, 56.86) * mm, "end": v(33.37, 57.12) * mm});
            skLineSegment(sketch, "E821", {"start": v(35.16, 57.37) * mm, "end": v(35.14, 57.37) * mm});
            skLineSegment(sketch, "E822", {"start": v(35.09, 55.24) * mm, "end": v(35.42, 55.73) * mm});
            skLineSegment(sketch, "E823", {"start": v(33.87, 57.96) * mm, "end": v(33.89, 58.05) * mm});
            skLineSegment(sketch, "E824", {"start": v(34.11, 57.18) * mm, "end": v(33.82, 57.04) * mm});
            skLineSegment(sketch, "E825", {"start": v(36.07, 56.93) * mm, "end": v(36.06, 56.98) * mm});
            skLineSegment(sketch, "E826", {"start": v(32.38, 58.06) * mm, "end": v(32.5, 58.1) * mm});
            skLineSegment(sketch, "E827", {"start": v(31.83, 57.84) * mm, "end": v(31.83, 57.81) * mm});
            skLineSegment(sketch, "E828", {"start": v(32.7, 57.37) * mm, "end": v(32.68, 57.34) * mm});
            skLineSegment(sketch, "E829", {"start": v(33.18, 58.5) * mm, "end": v(32.94, 58.46) * mm});
            skLineSegment(sketch, "E830", {"start": v(33.02, 57.98) * mm, "end": v(33.02, 57.96) * mm});
            skLineSegment(sketch, "E831", {"start": v(33.45, 54.07) * mm, "end": v(33.44, 54.06) * mm});
            skLineSegment(sketch, "E832", {"start": v(37.41, 52.72) * mm, "end": v(37.12, 52.52) * mm});
            skLineSegment(sketch, "E833", {"start": v(36.45, 52.28) * mm, "end": v(36.4, 52.28) * mm});
            skLineSegment(sketch, "E834", {"start": v(36.33, 51.98) * mm, "end": v(36.34, 51.98) * mm});
            skLineSegment(sketch, "E835", {"start": v(36.2, 52.46) * mm, "end": v(36.2, 52.48) * mm});
            skLineSegment(sketch, "E836", {"start": v(37.26, 52.34) * mm, "end": v(37.27, 52.35) * mm});
            skLineSegment(sketch, "E837", {"start": v(38.14, 55.31) * mm, "end": v(38.16, 55.35) * mm});
            skLineSegment(sketch, "E838", {"start": v(26.95, 58.04) * mm, "end": v(26.94, 58.03) * mm});
            skLineSegment(sketch, "E839", {"start": v(26.54, 62.58) * mm, "end": v(26.79, 62.72) * mm});
            skLineSegment(sketch, "E840", {"start": v(30.82, 58.9) * mm, "end": v(30.52, 58.79) * mm});
            skLineSegment(sketch, "E841", {"start": v(28.39, 55.84) * mm, "end": v(28.37, 55.85) * mm});
            skLineSegment(sketch, "E842", {"start": v(28.8, 62.54) * mm, "end": v(28.79, 62.55) * mm});
            skLineSegment(sketch, "E843", {"start": v(25.7, 61.6) * mm, "end": v(25.72, 61.65) * mm});
            skLineSegment(sketch, "E844", {"start": v(29.86, 58.75) * mm, "end": v(29.55, 58.83) * mm});
            skLineSegment(sketch, "E845", {"start": v(24.15, 58.33) * mm, "end": v(24.11, 58.35) * mm});
            skLineSegment(sketch, "E846", {"start": v(27.69, 62.73) * mm, "end": v(27.67, 62.73) * mm});
            skLineSegment(sketch, "E847", {"start": v(28.75, 59.3) * mm, "end": v(28.48, 59.47) * mm});
            skLineSegment(sketch, "E848", {"start": v(39.72, 53.6) * mm, "end": v(39.88, 53.82) * mm});
            skLineSegment(sketch, "E849", {"start": v(25.66, 58.17) * mm, "end": v(25.86, 58.16) * mm});
            skLineSegment(sketch, "E850", {"start": v(26.87, 62.29) * mm, "end": v(26.7, 62.05) * mm});
            skLineSegment(sketch, "E851", {"start": v(27.73, 58.63) * mm, "end": v(27.71, 58.61) * mm});
            skLineSegment(sketch, "E852", {"start": v(26.5, 58.37) * mm, "end": v(26.94, 58.84) * mm});
            skLineSegment(sketch, "E853", {"start": v(26.5, 61.22) * mm, "end": v(26.5, 61.2) * mm});
            skLineSegment(sketch, "E854", {"start": v(36.2, 52.4) * mm, "end": v(36.2, 52.42) * mm});
            skLineSegment(sketch, "E855", {"start": v(30.08, 62.49) * mm, "end": v(30.11, 62.47) * mm});
            skLineSegment(sketch, "E856", {"start": v(30.52, 58.79) * mm, "end": v(30.37, 58.75) * mm});
            skLineSegment(sketch, "E857", {"start": v(28.37, 55.85) * mm, "end": v(28.18, 55.9) * mm});
            skLineSegment(sketch, "E858", {"start": v(26.7, 62.05) * mm, "end": v(26.7, 62.03) * mm});
            skLineSegment(sketch, "E859", {"start": v(35.37, 52.26) * mm, "end": v(35.38, 52.22) * mm});
            skLineSegment(sketch, "E860", {"start": v(38, 50.77) * mm, "end": v(37.97, 50.8) * mm});
            skLineSegment(sketch, "E861", {"start": v(36.74, 53.33) * mm, "end": v(36.78, 53.39) * mm});
            skLineSegment(sketch, "E862", {"start": v(33.2, 60.9) * mm, "end": v(32.42, 60.23) * mm});
            skLineSegment(sketch, "E863", {"start": v(24.11, 58.35) * mm, "end": v(23.6, 58.66) * mm});
            skLineSegment(sketch, "E864", {"start": v(26.5, 61.2) * mm, "end": v(25.5, 60.91) * mm});
            skLineSegment(sketch, "E865", {"start": v(35.95, 51.93) * mm, "end": v(36.08, 51.93) * mm});
            skLineSegment(sketch, "E866", {"start": v(38.02, 51.22) * mm, "end": v(38.03, 51.23) * mm});
            skLineSegment(sketch, "E867", {"start": v(38.29, 55.73) * mm, "end": v(38.28, 55.78) * mm});
            skLineSegment(sketch, "E868", {"start": v(32.02, 59.96) * mm, "end": v(31.99, 59.95) * mm});
            skLineSegment(sketch, "E869", {"start": v(25.86, 58.16) * mm, "end": v(25.96, 58.16) * mm});
            skLineSegment(sketch, "E870", {"start": v(25.72, 61.65) * mm, "end": v(26.08, 62.14) * mm});
            skLineSegment(sketch, "E871", {"start": v(37.06, 52.2) * mm, "end": v(37.07, 52.21) * mm});
            skLineSegment(sketch, "E872", {"start": v(38.03, 56.13) * mm, "end": v(38.02, 56.13) * mm});
            skLineSegment(sketch, "E873", {"start": v(31.24, 55.23) * mm, "end": v(31.06, 54.95) * mm});
            skLineSegment(sketch, "E874", {"start": v(26.94, 58.84) * mm, "end": v(26.96, 58.87) * mm});
            skLineSegment(sketch, "E875", {"start": v(26.79, 62.72) * mm, "end": v(26.8, 62.73) * mm});
            skLineSegment(sketch, "E876", {"start": v(37.46, 52.63) * mm, "end": v(37.45, 52.65) * mm});
            skLineSegment(sketch, "E877", {"start": v(37.24, 56.22) * mm, "end": v(37.22, 56.21) * mm});
            skLineSegment(sketch, "E878", {"start": v(31.98, 60.73) * mm, "end": v(31.89, 60.84) * mm});
            skLineSegment(sketch, "E879", {"start": v(31.58, 54.5) * mm, "end": v(32.22, 55.44) * mm});
            skLineSegment(sketch, "E880", {"start": v(37.29, 55.31) * mm, "end": v(37.28, 55.3) * mm});
            skLineSegment(sketch, "E881", {"start": v(39.08, 50.65) * mm, "end": v(38.93, 50.6) * mm});
            skLineSegment(sketch, "E882", {"start": v(36.57, 52.3) * mm, "end": v(36.52, 52.28) * mm});
            skLineSegment(sketch, "E883", {"start": v(28.72, 60.04) * mm, "end": v(28.67, 59.96) * mm});
            skLineSegment(sketch, "E884", {"start": v(33.6, 56.63) * mm, "end": v(33.65, 56.66) * mm});
            skLineSegment(sketch, "E885", {"start": v(27.67, 62.73) * mm, "end": v(27.65, 62.72) * mm});
            skLineSegment(sketch, "E886", {"start": v(38.6, 50.56) * mm, "end": v(38.45, 50.58) * mm});
            skLineSegment(sketch, "E887", {"start": v(36.08, 53.6) * mm, "end": v(36.07, 53.58) * mm});
            skLineSegment(sketch, "E888", {"start": v(37.1, 55.03) * mm, "end": v(36.95, 54.8) * mm});
            skLineSegment(sketch, "E889", {"start": v(35.11, 56.58) * mm, "end": v(35.04, 56.44) * mm});
            skLineSegment(sketch, "E890", {"start": v(35.47, 52.68) * mm, "end": v(35.47, 52.67) * mm});
            skLineSegment(sketch, "E891", {"start": v(35.1, 56.86) * mm, "end": v(35.12, 56.82) * mm});
            skLineSegment(sketch, "E892", {"start": v(35.43, 52.14) * mm, "end": v(35.57, 52) * mm});
            skLineSegment(sketch, "E893", {"start": v(39.36, 50.76) * mm, "end": v(39.08, 50.65) * mm});
            skLineSegment(sketch, "E894", {"start": v(32.04, 60.6) * mm, "end": v(32.03, 60.64) * mm});
            skLineSegment(sketch, "E895", {"start": v(27.1, 62.51) * mm, "end": v(26.99, 62.41) * mm});
            skLineSegment(sketch, "E896", {"start": v(30.43, 61.7) * mm, "end": v(30.02, 61.92) * mm});
            skLineSegment(sketch, "E897", {"start": v(30.23, 56.29) * mm, "end": v(30.24, 56.24) * mm});
            skLineSegment(sketch, "E898", {"start": v(26.55, 61.62) * mm, "end": v(26.5, 61.23) * mm});
            skLineSegment(sketch, "E899", {"start": v(30.83, 58.9) * mm, "end": v(30.84, 58.9) * mm});
            skLineSegment(sketch, "E900", {"start": v(30.22, 56.1) * mm, "end": v(30.2, 56.09) * mm});
            skLineSegment(sketch, "E901", {"start": v(33.66, 58.44) * mm, "end": v(33.43, 58.49) * mm});
            skLineSegment(sketch, "E902", {"start": v(30.04, 58.72) * mm, "end": v(30.03, 58.72) * mm});
            skLineSegment(sketch, "E903", {"start": v(29.86, 55.92) * mm, "end": v(29.5, 55.85) * mm});
            skLineSegment(sketch, "E904", {"start": v(32.66, 58.38) * mm, "end": v(32.44, 58.32) * mm});
            skLineSegment(sketch, "E905", {"start": v(28.6, 55.8) * mm, "end": v(28.59, 55.8) * mm});
            skLineSegment(sketch, "E906", {"start": v(35.37, 52.4) * mm, "end": v(35.36, 52.35) * mm});
            skLineSegment(sketch, "E907", {"start": v(31.85, 57.95) * mm, "end": v(31.84, 57.94) * mm});
            skLineSegment(sketch, "E908", {"start": v(25.7, 57.3) * mm, "end": v(25.68, 57.33) * mm});
            skLineSegment(sketch, "E909", {"start": v(35.87, 55.72) * mm, "end": v(35.12, 55.25) * mm});
            skLineSegment(sketch, "E910", {"start": v(28.99, 62.94) * mm, "end": v(29.52, 62.75) * mm});
            skLineSegment(sketch, "E911", {"start": v(32.1, 57.92) * mm, "end": v(32.12, 57.93) * mm});
            skLineSegment(sketch, "E912", {"start": v(24.75, 58.8) * mm, "end": v(25.63, 58.18) * mm});
            skLineSegment(sketch, "E913", {"start": v(35.93, 56.51) * mm, "end": v(36.03, 56.72) * mm});
            skLineSegment(sketch, "E914", {"start": v(31.65, 61.66) * mm, "end": v(33.18, 60.91) * mm});
            skLineSegment(sketch, "E915", {"start": v(26.28, 58.24) * mm, "end": v(26.45, 58.33) * mm});
            skLineSegment(sketch, "E916", {"start": v(32.14, 60.01) * mm, "end": v(32.1, 59.98) * mm});
            skLineSegment(sketch, "E917", {"start": v(29.31, 62.3) * mm, "end": v(29.17, 62.37) * mm});
            skLineSegment(sketch, "E918", {"start": v(31.78, 60.03) * mm, "end": v(32, 60.32) * mm});
            skLineSegment(sketch, "E919", {"start": v(28.25, 62.7) * mm, "end": v(28.07, 62.72) * mm});
            skLineSegment(sketch, "E920", {"start": v(30.85, 54.65) * mm, "end": v(30.78, 54.54) * mm});
            skLineSegment(sketch, "E921", {"start": v(32.52, 55.8) * mm, "end": v(32.54, 55.81) * mm});
            skLineSegment(sketch, "E922", {"start": v(33.99, 56.85) * mm, "end": v(34.14, 56.91) * mm});
            skLineSegment(sketch, "E923", {"start": v(36.73, 56.09) * mm, "end": v(35.92, 55.75) * mm});
            skLineSegment(sketch, "E924", {"start": v(32.93, 58.1) * mm, "end": v(32.95, 58.1) * mm});
            skLineSegment(sketch, "E925", {"start": v(33.01, 57.91) * mm, "end": v(33, 57.9) * mm});
            skLineSegment(sketch, "E926", {"start": v(32.67, 57.33) * mm, "end": v(32.53, 57.12) * mm});
            skLineSegment(sketch, "E927", {"start": v(32.01, 58.1) * mm, "end": v(31.85, 57.95) * mm});
            skLineSegment(sketch, "E928", {"start": v(36.7, 55.83) * mm, "end": v(36.7, 55.83) * mm});
            skLineSegment(sketch, "E929", {"start": v(35.92, 55.75) * mm, "end": v(35.87, 55.72) * mm});
            skLineSegment(sketch, "E930", {"start": v(37.24, 55.8) * mm, "end": v(37.33, 55.7) * mm});
            skLineSegment(sketch, "E931", {"start": v(30.11, 62.47) * mm, "end": v(31.48, 61.74) * mm});
            skLineSegment(sketch, "E932", {"start": v(35.93, 56.5) * mm, "end": v(35.93, 56.51) * mm});
            skLineSegment(sketch, "E933", {"start": v(37.37, 55.57) * mm, "end": v(37.37, 55.54) * mm});
            skLineSegment(sketch, "E934", {"start": v(32.42, 60.23) * mm, "end": v(32.39, 60.2) * mm});
            skLineSegment(sketch, "E935", {"start": v(35.84, 57.28) * mm, "end": v(35.83, 57.3) * mm});
            skLineSegment(sketch, "E936", {"start": v(33, 57.9) * mm, "end": v(32.99, 57.84) * mm});
            skLineSegment(sketch, "E937", {"start": v(34.48, 57) * mm, "end": v(34.64, 57.01) * mm});
            skLineSegment(sketch, "E938", {"start": v(36.95, 54.8) * mm, "end": v(36.94, 54.78) * mm});
            skLineSegment(sketch, "E939", {"start": v(31.99, 59.95) * mm, "end": v(31.94, 59.95) * mm});
            skLineSegment(sketch, "E940", {"start": v(34.48, 57.3) * mm, "end": v(34.45, 57.3) * mm});
            skLineSegment(sketch, "E941", {"start": v(32.53, 57.12) * mm, "end": v(32.48, 57.05) * mm});
            skLineSegment(sketch, "E942", {"start": v(35.12, 56.82) * mm, "end": v(35.14, 56.79) * mm});
            skLineSegment(sketch, "E943", {"start": v(35.47, 52.67) * mm, "end": v(35.39, 52.49) * mm});
            skLineSegment(sketch, "E944", {"start": v(32.04, 60.47) * mm, "end": v(32.04, 60.53) * mm});
            skLineSegment(sketch, "E945", {"start": v(32.99, 56.56) * mm, "end": v(33, 56.57) * mm});
            skLineSegment(sketch, "E946", {"start": v(35.04, 56.44) * mm, "end": v(35.04, 56.43) * mm});
            skLineSegment(sketch, "E947", {"start": v(35.57, 52) * mm, "end": v(35.58, 52) * mm});
            skLineSegment(sketch, "E948", {"start": v(33.78, 57.75) * mm, "end": v(33.79, 57.77) * mm});
            skLineSegment(sketch, "E949", {"start": v(33.44, 54.06) * mm, "end": v(33.26, 53.79) * mm});
            skLineSegment(sketch, "E950", {"start": v(36.34, 51.98) * mm, "end": v(36.58, 52.05) * mm});
            skLineSegment(sketch, "E951", {"start": v(33.89, 58.16) * mm, "end": v(33.88, 58.18) * mm});
            skLineSegment(sketch, "E952", {"start": v(33.79, 53.33) * mm, "end": v(34.42, 54.27) * mm});
            skLineSegment(sketch, "E953", {"start": v(37.27, 52.35) * mm, "end": v(37.44, 52.5) * mm});
            skLineSegment(sketch, "E954", {"start": v(33.67, 58.44) * mm, "end": v(33.66, 58.44) * mm});
            skLineSegment(sketch, "E955", {"start": v(35.08, 54.97) * mm, "end": v(35.8, 55.45) * mm});
            skLineSegment(sketch, "E956", {"start": v(37.12, 52.52) * mm, "end": v(37.1, 52.5) * mm});
            skLineSegment(sketch, "E957", {"start": v(32.68, 58.39) * mm, "end": v(32.66, 58.38) * mm});
            skLineSegment(sketch, "E958", {"start": v(36.2, 55.67) * mm, "end": v(36.36, 55.74) * mm});
            skLineSegment(sketch, "E959", {"start": v(36.4, 52.28) * mm, "end": v(36.27, 52.3) * mm});
            skLineSegment(sketch, "E960", {"start": v(28.48, 59.47) * mm, "end": v(28.38, 59.52) * mm});
            skLineSegment(sketch, "E961", {"start": v(35.14, 56.69) * mm, "end": v(35.14, 56.65) * mm});
            skLineSegment(sketch, "E962", {"start": v(29.02, 56.25) * mm, "end": v(29.24, 56.21) * mm});
            skLineSegment(sketch, "E963", {"start": v(35.38, 52.22) * mm, "end": v(35.4, 52.18) * mm});
            skLineSegment(sketch, "E964", {"start": v(28.4, 63.02) * mm, "end": v(28.67, 63) * mm});
            skLineSegment(sketch, "E965", {"start": v(31.2, 61.29) * mm, "end": v(31.14, 61.32) * mm});
            skLineSegment(sketch, "E966", {"start": v(27.71, 58.61) * mm, "end": v(27.25, 58.18) * mm});
            skLineSegment(sketch, "E967", {"start": v(34.7, 55.9) * mm, "end": v(34.65, 55.82) * mm});
            skLineSegment(sketch, "E968", {"start": v(29.72, 56.21) * mm, "end": v(29.75, 56.21) * mm});
            skLineSegment(sketch, "E969", {"start": v(36.08, 51.93) * mm, "end": v(36.32, 51.97) * mm});
            skLineSegment(sketch, "E970", {"start": v(29.48, 59.53) * mm, "end": v(29.51, 59.52) * mm});
            skLineSegment(sketch, "E971", {"start": v(26.94, 58.03) * mm, "end": v(26.68, 57.95) * mm});
            skLineSegment(sketch, "E972", {"start": v(33.01, 53.37) * mm, "end": v(33.76, 53.3) * mm});
            skLineSegment(sketch, "E973", {"start": v(30.24, 56.2) * mm, "end": v(30.24, 56.17) * mm});
            skLineSegment(sketch, "E974", {"start": v(37.07, 52.21) * mm, "end": v(37.17, 52.27) * mm});
            skLineSegment(sketch, "E975", {"start": v(30.35, 58.74) * mm, "end": v(30.2, 58.72) * mm});
            skLineSegment(sketch, "E976", {"start": v(26.09, 57.87) * mm, "end": v(26.96, 57.32) * mm});
            skLineSegment(sketch, "E977", {"start": v(34.74, 54.64) * mm, "end": v(35.06, 54.95) * mm});
            skLineSegment(sketch, "E978", {"start": v(30.05, 56) * mm, "end": v(29.97, 55.95) * mm});
            skLineSegment(sketch, "E979", {"start": v(37.45, 52.65) * mm, "end": v(37.44, 52.67) * mm});
            skLineSegment(sketch, "E980", {"start": v(27.42, 57.02) * mm, "end": v(28.3, 56.52) * mm});
            skLineSegment(sketch, "E981", {"start": v(35.88, 55.5) * mm, "end": v(36.18, 55.66) * mm});
            skLineSegment(sketch, "E982", {"start": v(29.47, 55.84) * mm, "end": v(29.05, 55.8) * mm});
            skLineSegment(sketch, "E983", {"start": v(36.52, 52.28) * mm, "end": v(36.45, 52.28) * mm});
            skLineSegment(sketch, "E984", {"start": v(27.08, 62.84) * mm, "end": v(27.12, 62.86) * mm});
            skLineSegment(sketch, "E985", {"start": v(36.52, 55.8) * mm, "end": v(36.53, 55.8) * mm});
            skLineSegment(sketch, "E986", {"start": v(28.15, 55.91) * mm, "end": v(27.76, 56.07) * mm});
            skLineSegment(sketch, "E987", {"start": v(36.2, 52.42) * mm, "end": v(36.2, 52.45) * mm});
            skLineSegment(sketch, "E988", {"start": v(38.91, 50.6) * mm, "end": v(38.77, 50.57) * mm});
            skLineSegment(sketch, "E989", {"start": v(31.89, 60.84) * mm, "end": v(31.2, 61.29) * mm});
            skLineSegment(sketch, "E990", {"start": v(36.88, 55.83) * mm, "end": v(37.21, 55.8) * mm});
            skLineSegment(sketch, "E991", {"start": v(23.58, 58.67) * mm, "end": v(24.64, 58.84) * mm});
            skLineSegment(sketch, "E992", {"start": v(36.78, 53.39) * mm, "end": v(37.82, 54.8) * mm});
            skLineSegment(sketch, "E993", {"start": v(38.43, 50.58) * mm, "end": v(38.13, 50.64) * mm});
            skLineSegment(sketch, "E994", {"start": v(28.67, 59.96) * mm, "end": v(29.48, 59.53) * mm});
            skLineSegment(sketch, "E995", {"start": v(37.36, 55.63) * mm, "end": v(37.37, 55.6) * mm});
            skLineSegment(sketch, "E996", {"start": v(25.97, 58.16) * mm, "end": v(26.07, 58.18) * mm});
            skLineSegment(sketch, "E997", {"start": v(38.28, 55.78) * mm, "end": v(38.28, 55.8) * mm});
            skLineSegment(sketch, "E998", {"start": v(37.95, 50.83) * mm, "end": v(37.94, 50.87) * mm});
            skLineSegment(sketch, "E999", {"start": v(30.37, 58.75) * mm, "end": v(30.35, 58.74) * mm});
            skLineSegment(sketch, "E1000", {"start": v(37.28, 55.3) * mm, "end": v(37.12, 55.05) * mm});
            skLineSegment(sketch, "E1001", {"start": v(38.02, 56.13) * mm, "end": v(37.72, 56.2) * mm});
            skLineSegment(sketch, "E1002", {"start": v(38.07, 51.3) * mm, "end": v(38.72, 52.23) * mm});
            skLineSegment(sketch, "E1003", {"start": v(31.94, 59.95) * mm, "end": v(31.83, 59.97) * mm});
            skLineSegment(sketch, "E1004", {"start": v(29.55, 58.83) * mm, "end": v(29.54, 58.83) * mm});
            skLineSegment(sketch, "E1005", {"start": v(34.98, 56.98) * mm, "end": v(35, 56.98) * mm});
            skLineSegment(sketch, "E1006", {"start": v(36.07, 53.58) * mm, "end": v(35.5, 52.74) * mm});
            skLineSegment(sketch, "E1007", {"start": v(37.22, 56.21) * mm, "end": v(37.07, 56.18) * mm});
            skLineSegment(sketch, "E1008", {"start": v(36.06, 56.82) * mm, "end": v(36.07, 56.88) * mm});
            skLineSegment(sketch, "E1009", {"start": v(31.83, 57.89) * mm, "end": v(31.83, 57.86) * mm});
            skLineSegment(sketch, "E1010", {"start": v(34.65, 57.01) * mm, "end": v(34.98, 56.98) * mm});
            skLineSegment(sketch, "E1011", {"start": v(32.24, 58) * mm, "end": v(32.36, 58.05) * mm});
            skLineSegment(sketch, "E1012", {"start": v(35.15, 56.72) * mm, "end": v(35.14, 56.69) * mm});
            skLineSegment(sketch, "E1013", {"start": v(33.41, 58.49) * mm, "end": v(33.3, 58.5) * mm});
            skLineSegment(sketch, "E1014", {"start": v(33, 58.02) * mm, "end": v(33, 58) * mm});
            skLineSegment(sketch, "E1015", {"start": v(34.84, 56.1) * mm, "end": v(34.7, 55.9) * mm});
            skLineSegment(sketch, "E1016", {"start": v(32.43, 58.32) * mm, "end": v(32.22, 58.24) * mm});
            skLineSegment(sketch, "E1017", {"start": v(32.94, 57.75) * mm, "end": v(32.7, 57.37) * mm});
            skLineSegment(sketch, "E1018", {"start": v(32.98, 53.37) * mm, "end": v(33.01, 53.37) * mm});
            skLineSegment(sketch, "E1019", {"start": v(28.07, 62.72) * mm, "end": v(28.05, 62.72) * mm});
            skLineSegment(sketch, "E1020", {"start": v(39.38, 50.77) * mm, "end": v(39.36, 50.76) * mm});
            skLineSegment(sketch, "E1021", {"start": v(28.36, 63.03) * mm, "end": v(28.4, 63.02) * mm});
            skLineSegment(sketch, "E1022", {"start": v(40.1, 54.2) * mm, "end": v(40.1, 54.22) * mm});
            skLineSegment(sketch, "E1023", {"start": v(28.1, 59.13) * mm, "end": v(27.73, 58.63) * mm});
            skLineSegment(sketch, "E1024", {"start": v(24.2, 58.29) * mm, "end": v(24.15, 58.33) * mm});
            skLineSegment(sketch, "E1025", {"start": v(26.99, 62.41) * mm, "end": v(26.88, 62.3) * mm});
            skLineSegment(sketch, "E1026", {"start": v(35.82, 51.95) * mm, "end": v(35.84, 51.94) * mm});
            skLineSegment(sketch, "E1027", {"start": v(38.6, 50.56) * mm, "end": v(38.6, 50.56) * mm});
            skLineSegment(sketch, "E1028", {"start": v(29.56, 62.73) * mm, "end": v(30.08, 62.49) * mm});
            skLineSegment(sketch, "E1029", {"start": v(26.96, 58.04) * mm, "end": v(26.95, 58.04) * mm});
            skLineSegment(sketch, "E1030", {"start": v(25.65, 58.17) * mm, "end": v(25.66, 58.17) * mm});
            skLineSegment(sketch, "E1031", {"start": v(36.83, 52.11) * mm, "end": v(36.84, 52.12) * mm});
            skLineSegment(sketch, "E1032", {"start": v(26.5, 61.23) * mm, "end": v(26.5, 61.22) * mm});
            skLineSegment(sketch, "E1033", {"start": v(38.11, 50.65) * mm, "end": v(38, 50.77) * mm});
            skLineSegment(sketch, "E1034", {"start": v(26.1, 57.87) * mm, "end": v(26.09, 57.87) * mm});
            skLineSegment(sketch, "E1035", {"start": v(34.72, 54.62) * mm, "end": v(34.74, 54.64) * mm});
            skLineSegment(sketch, "E1036", {"start": v(26.46, 58.34) * mm, "end": v(26.5, 58.37) * mm});
            skLineSegment(sketch, "E1037", {"start": v(37.46, 52.57) * mm, "end": v(37.46, 52.6) * mm});
            skLineSegment(sketch, "E1038", {"start": v(25.55, 61.28) * mm, "end": v(25.7, 61.6) * mm});
            skLineSegment(sketch, "E1039", {"start": v(37.95, 51.06) * mm, "end": v(38.02, 51.22) * mm});
            skLineSegment(sketch, "E1040", {"start": v(27.36, 57.06) * mm, "end": v(27.42, 57.02) * mm});
            skLineSegment(sketch, "E1041", {"start": v(28.82, 62.54) * mm, "end": v(28.8, 62.54) * mm});
            skLineSegment(sketch, "E1042", {"start": v(36.76, 52.36) * mm, "end": v(36.64, 52.31) * mm});
            skLineSegment(sketch, "E1043", {"start": v(26.52, 62.57) * mm, "end": v(26.54, 62.58) * mm});
            skLineSegment(sketch, "E1044", {"start": v(28.77, 56.33) * mm, "end": v(28.99, 56.26) * mm});
            skLineSegment(sketch, "E1045", {"start": v(28.05, 62.72) * mm, "end": v(27.69, 62.73) * mm});
            skLineSegment(sketch, "E1046", {"start": v(36.22, 52.37) * mm, "end": v(36.2, 52.4) * mm});
            skLineSegment(sketch, "E1047", {"start": v(39.4, 50.78) * mm, "end": v(39.38, 50.77) * mm});
            skLineSegment(sketch, "E1048", {"start": v(38.76, 50.57) * mm, "end": v(38.6, 50.56) * mm});
            skLineSegment(sketch, "E1049", {"start": v(36.26, 52.6) * mm, "end": v(36.7, 53.28) * mm});
            skLineSegment(sketch, "E1050", {"start": v(25.63, 58.18) * mm, "end": v(25.65, 58.17) * mm});
            skLineSegment(sketch, "E1051", {"start": v(38.25, 55.57) * mm, "end": v(38.28, 55.67) * mm});
            skLineSegment(sketch, "E1052", {"start": v(38.12, 50.65) * mm, "end": v(38.11, 50.65) * mm});
            skLineSegment(sketch, "E1053", {"start": v(26.45, 58.33) * mm, "end": v(26.46, 58.34) * mm});
            skLineSegment(sketch, "E1054", {"start": v(38.2, 55.96) * mm, "end": v(38.04, 56.12) * mm});
            skLineSegment(sketch, "E1055", {"start": v(37.93, 50.98) * mm, "end": v(37.95, 51.06) * mm});
            skLineSegment(sketch, "E1056", {"start": v(29.88, 58.74) * mm, "end": v(29.86, 58.75) * mm});
            skLineSegment(sketch, "E1057", {"start": v(29.17, 62.37) * mm, "end": v(28.82, 62.54) * mm});
            skLineSegment(sketch, "E1058", {"start": v(37.4, 56.23) * mm, "end": v(37.39, 56.23) * mm});
            skLineSegment(sketch, "E1059", {"start": v(39.52, 53.33) * mm, "end": v(39.71, 53.6) * mm});
            skLineSegment(sketch, "E1060", {"start": v(28.77, 59.3) * mm, "end": v(28.75, 59.3) * mm});
            skLineSegment(sketch, "E1061", {"start": v(36.78, 54.55) * mm, "end": v(36.75, 54.51) * mm});
            skLineSegment(sketch, "E1062", {"start": v(37.37, 55.5) * mm, "end": v(37.35, 55.44) * mm});
            skLineSegment(sketch, "E1063", {"start": v(30, 61.93) * mm, "end": v(28.72, 60.04) * mm});
            skLineSegment(sketch, "E1064", {"start": v(32.02, 60.67) * mm, "end": v(31.98, 60.73) * mm});
            skLineSegment(sketch, "E1065", {"start": v(37.39, 56.23) * mm, "end": v(37.24, 56.22) * mm});
            skLineSegment(sketch, "E1066", {"start": v(27.74, 63.03) * mm, "end": v(28.34, 63.03) * mm});
            skLineSegment(sketch, "E1067", {"start": v(34.42, 54.27) * mm, "end": v(34.44, 54.29) * mm});
            skLineSegment(sketch, "E1068", {"start": v(36.79, 54.57) * mm, "end": v(36.78, 54.55) * mm});
            skLineSegment(sketch, "E1069", {"start": v(35.8, 55.45) * mm, "end": v(35.86, 55.49) * mm});
            skLineSegment(sketch, "E1070", {"start": v(32.95, 58.1) * mm, "end": v(32.98, 58.06) * mm});
            skLineSegment(sketch, "E1071", {"start": v(36.36, 55.74) * mm, "end": v(36.51, 55.8) * mm});
            skLineSegment(sketch, "E1072", {"start": v(32.99, 57.84) * mm, "end": v(32.94, 57.76) * mm});
            skLineSegment(sketch, "E1073", {"start": v(36.7, 55.83) * mm, "end": v(36.87, 55.83) * mm});
            skLineSegment(sketch, "E1074", {"start": v(37.33, 55.7) * mm, "end": v(37.35, 55.66) * mm});
            skLineSegment(sketch, "E1075", {"start": v(37.55, 56.23) * mm, "end": v(37.54, 56.23) * mm});
            skLineSegment(sketch, "E1076", {"start": v(33.25, 53.77) * mm, "end": v(33.06, 53.48) * mm});
            skLineSegment(sketch, "E1077", {"start": v(37.37, 55.54) * mm, "end": v(37.37, 55.5) * mm});
            skLineSegment(sketch, "E1078", {"start": v(35.91, 56.48) * mm, "end": v(35.93, 56.5) * mm});
            skLineSegment(sketch, "E1079", {"start": v(33.6, 57.46) * mm, "end": v(33.78, 57.75) * mm});
            skLineSegment(sketch, "E1080", {"start": v(32.02, 58.1) * mm, "end": v(32.01, 58.1) * mm});
            skLineSegment(sketch, "E1081", {"start": v(36, 57.12) * mm, "end": v(35.84, 57.28) * mm});
            skLineSegment(sketch, "E1082", {"start": v(33.9, 58.14) * mm, "end": v(33.89, 58.16) * mm});
            skLineSegment(sketch, "E1083", {"start": v(31.86, 57.74) * mm, "end": v(31.88, 57.75) * mm});
            skLineSegment(sketch, "E1084", {"start": v(34.78, 57.36) * mm, "end": v(34.48, 57.3) * mm});
            skLineSegment(sketch, "E1085", {"start": v(33.68, 58.43) * mm, "end": v(33.67, 58.44) * mm});
            skLineSegment(sketch, "E1086", {"start": v(33.2, 56.68) * mm, "end": v(32.99, 56.56) * mm});
            skLineSegment(sketch, "E1087", {"start": v(32.92, 58.45) * mm, "end": v(32.68, 58.39) * mm});
            skLineSegment(sketch, "E1088", {"start": v(30.24, 56.21) * mm, "end": v(30.24, 56.2) * mm});
            skLineSegment(sketch, "E1089", {"start": v(23.6, 58.66) * mm, "end": v(23.58, 58.67) * mm});
            skLineSegment(sketch, "E1090", {"start": v(37.7, 56.2) * mm, "end": v(37.55, 56.23) * mm});
            skLineSegment(sketch, "E1091", {"start": v(31.88, 57.75) * mm, "end": v(32.1, 57.92) * mm});
            skLineSegment(sketch, "E1092", {"start": v(30.78, 54.54) * mm, "end": v(30.8, 54.54) * mm});
            skLineSegment(sketch, "E1093", {"start": v(30.06, 56) * mm, "end": v(30.05, 56) * mm});
            skLineSegment(sketch, "E1094", {"start": v(39.88, 53.83) * mm, "end": v(39.9, 53.84) * mm});
            skLineSegment(sketch, "E1095", {"start": v(36.2, 52.48) * mm, "end": v(36.22, 52.52) * mm});
            skLineSegment(sketch, "E1096", {"start": v(27.7, 63.02) * mm, "end": v(27.74, 63.03) * mm});
            skLineSegment(sketch, "E1097", {"start": v(32.54, 55.81) * mm, "end": v(32.85, 56.12) * mm});
            skLineSegment(sketch, "E1098", {"start": v(28.99, 56.26) * mm, "end": v(29.02, 56.25) * mm});
            skLineSegment(sketch, "E1099", {"start": v(29.5, 55.84) * mm, "end": v(29.47, 55.84) * mm});
            skLineSegment(sketch, "E1100", {"start": v(38.16, 55.35) * mm, "end": v(38.17, 55.36) * mm});
            skLineSegment(sketch, "E1101", {"start": v(29.5, 56.2) * mm, "end": v(29.72, 56.21) * mm});
            skLineSegment(sketch, "E1102", {"start": v(28.18, 55.9) * mm, "end": v(28.15, 55.91) * mm});
            skLineSegment(sketch, "E1103", {"start": v(38.26, 55.87) * mm, "end": v(38.23, 55.92) * mm});
            skLineSegment(sketch, "E1104", {"start": v(32.22, 55.44) * mm, "end": v(32.23, 55.46) * mm});
            skLineSegment(sketch, "E1105", {"start": v(28.67, 63) * mm, "end": v(28.95, 62.94) * mm});
            skLineSegment(sketch, "E1106", {"start": v(33.65, 56.66) * mm, "end": v(33.67, 56.67) * mm});
            skLineSegment(sketch, "E1107", {"start": v(38.28, 55.8) * mm, "end": v(38.27, 55.83) * mm});
            skLineSegment(sketch, "E1108", {"start": v(31.48, 61.74) * mm, "end": v(31.54, 61.71) * mm});
            skLineSegment(sketch, "E1109", {"start": v(32.68, 57.34) * mm, "end": v(32.67, 57.33) * mm});
            skLineSegment(sketch, "E1110", {"start": v(34.3, 56.97) * mm, "end": v(34.31, 56.97) * mm});
            skLineSegment(sketch, "E1111", {"start": v(37.72, 56.2) * mm, "end": v(37.7, 56.2) * mm});
            skLineSegment(sketch, "E1112", {"start": v(32.39, 60.2) * mm, "end": v(32.24, 60.08) * mm});
            skLineSegment(sketch, "E1113", {"start": v(31.06, 54.95) * mm, "end": v(31.05, 54.94) * mm});
            skLineSegment(sketch, "E1114", {"start": v(37.07, 56.18) * mm, "end": v(36.77, 56.1) * mm});
            skLineSegment(sketch, "E1115", {"start": v(35.07, 55.22) * mm, "end": v(35.09, 55.24) * mm});
            skLineSegment(sketch, "E1116", {"start": v(25.68, 57.33) * mm, "end": v(24.2, 58.29) * mm});
            skLineSegment(sketch, "E1117", {"start": v(29.5, 55.85) * mm, "end": v(29.5, 55.84) * mm});
            skLineSegment(sketch, "E1118", {"start": v(26.88, 62.3) * mm, "end": v(26.87, 62.29) * mm});
            skLineSegment(sketch, "E1119", {"start": v(40.1, 54.23) * mm, "end": v(40.1, 54.25) * mm});
            skLineSegment(sketch, "E1120", {"start": v(28.59, 55.8) * mm, "end": v(28.39, 55.84) * mm});
            skLineSegment(sketch, "E1121", {"start": v(30.2, 56.09) * mm, "end": v(30.06, 56) * mm});
            skLineSegment(sketch, "E1122", {"start": v(39.71, 53.6) * mm, "end": v(39.72, 53.6) * mm});
            skLineSegment(sketch, "E1123", {"start": v(35.36, 52.35) * mm, "end": v(35.36, 52.3) * mm});
            skLineSegment(sketch, "E1124", {"start": v(36.87, 55.83) * mm, "end": v(36.88, 55.83) * mm});
            skLineSegment(sketch, "E1125", {"start": v(37.35, 55.66) * mm, "end": v(37.36, 55.63) * mm});
            skLineSegment(sketch, "E1126", {"start": v(36.51, 55.8) * mm, "end": v(36.52, 55.8) * mm});
            skLineSegment(sketch, "E1127", {"start": v(36.2, 52.4) * mm, "end": v(36.2, 52.4) * mm});
            skLineSegment(sketch, "E1128", {"start": v(32.04, 59.96) * mm, "end": v(32.02, 59.96) * mm});
            skLineSegment(sketch, "E1129", {"start": v(36.7, 53.28) * mm, "end": v(36.74, 53.33) * mm});
            skLineSegment(sketch, "E1130", {"start": v(32, 60.34) * mm, "end": v(32.04, 60.47) * mm});
            skLineSegment(sketch, "E1131", {"start": v(32.87, 56.14) * mm, "end": v(33.6, 56.63) * mm});
            skLineSegment(sketch, "E1132", {"start": v(38.28, 55.67) * mm, "end": v(38.29, 55.73) * mm});
            skLineSegment(sketch, "E1133", {"start": v(36.64, 52.31) * mm, "end": v(36.57, 52.3) * mm});
            skLineSegment(sketch, "E1134", {"start": v(38.04, 56.12) * mm, "end": v(38.03, 56.13) * mm});
            skLineSegment(sketch, "E1135", {"start": v(40.1, 54.18) * mm, "end": v(40.1, 54.2) * mm});
            skLineSegment(sketch, "E1136", {"start": v(31.54, 61.71) * mm, "end": v(31.65, 61.66) * mm});
            skLineSegment(sketch, "E1137", {"start": v(40.08, 54.14) * mm, "end": v(40.1, 54.18) * mm});
            skLineSegment(sketch, "E1138", {"start": v(35.14, 56.79) * mm, "end": v(35.14, 56.75) * mm});
            skLineSegment(sketch, "E1139", {"start": v(26.3, 62.39) * mm, "end": v(26.52, 62.57) * mm});
            skLineSegment(sketch, "E1140", {"start": v(35.04, 56.43) * mm, "end": v(34.85, 56.12) * mm});
            skLineSegment(sketch, "E1141", {"start": v(37.93, 50.94) * mm, "end": v(37.93, 50.98) * mm});
            skLineSegment(sketch, "E1142", {"start": v(28.95, 62.94) * mm, "end": v(28.99, 62.94) * mm});
            skLineSegment(sketch, "E1143", {"start": v(39.5, 53.3) * mm, "end": v(39.52, 53.33) * mm});
            skLineSegment(sketch, "E1144", {"start": v(37.82, 54.8) * mm, "end": v(38.14, 55.31) * mm});
            skLineSegment(sketch, "E1145", {"start": v(33.02, 57.96) * mm, "end": v(33.02, 57.93) * mm});
            skLineSegment(sketch, "E1146", {"start": v(37.44, 52.67) * mm, "end": v(37.41, 52.72) * mm});
            skLineSegment(sketch, "E1147", {"start": v(31.83, 57.81) * mm, "end": v(31.84, 57.8) * mm});
            skLineSegment(sketch, "E1148", {"start": v(40.1, 54.22) * mm, "end": v(40.1, 54.23) * mm});
            skLineSegment(sketch, "E1149", {"start": v(36.2, 52.45) * mm, "end": v(36.2, 52.46) * mm});
            skLineSegment(sketch, "E1150", {"start": v(32.5, 58.1) * mm, "end": v(32.65, 58.11) * mm});
            skLineSegment(sketch, "E1151", {"start": v(33.02, 57.93) * mm, "end": v(33.01, 57.91) * mm});
            skLineSegment(sketch, "E1152", {"start": v(36.77, 56.1) * mm, "end": v(36.75, 56.1) * mm});
            skLineSegment(sketch, "E1153", {"start": v(33.96, 56.84) * mm, "end": v(33.99, 56.85) * mm});
            skLineSegment(sketch, "E1154", {"start": v(33.25, 56.71) * mm, "end": v(33.2, 56.69) * mm});
            skLineSegment(sketch, "E1155", {"start": v(35.43, 55.74) * mm, "end": v(35.67, 56.1) * mm});
            skLineSegment(sketch, "E1156", {"start": v(34.47, 57) * mm, "end": v(34.48, 57) * mm});
            skLineSegment(sketch, "E1157", {"start": v(31.05, 54.94) * mm, "end": v(30.85, 54.65) * mm});
            skLineSegment(sketch, "E1158", {"start": v(36.04, 57.03) * mm, "end": v(36.02, 57.07) * mm});
            skLineSegment(sketch, "E1159", {"start": v(32.23, 55.46) * mm, "end": v(32.52, 55.8) * mm});
            skLineSegment(sketch, "E1160", {"start": v(35.12, 57.37) * mm, "end": v(34.8, 57.37) * mm});
            skLineSegment(sketch, "E1161", {"start": v(36.26, 52.6) * mm, "end": v(36.26, 52.6) * mm});
            skLineSegment(sketch, "E1162", {"start": v(30.03, 58.72) * mm, "end": v(29.88, 58.74) * mm});
            skLineSegment(sketch, "E1163", {"start": v(28.34, 56.5) * mm, "end": v(28.77, 56.33) * mm});
            skLineSegment(sketch, "E1164", {"start": v(38.17, 55.36) * mm, "end": v(38.25, 55.57) * mm});
            skLineSegment(sketch, "E1165", {"start": v(28.78, 59.3) * mm, "end": v(28.77, 59.3) * mm});
            skLineSegment(sketch, "E1166", {"start": v(29.48, 56.2) * mm, "end": v(29.5, 56.2) * mm});
            skLineSegment(sketch, "E1167", {"start": v(36.6, 52.05) * mm, "end": v(36.83, 52.11) * mm});
            skLineSegment(sketch, "E1168", {"start": v(28.13, 59.17) * mm, "end": v(28.1, 59.13) * mm});
            skLineSegment(sketch, "E1169", {"start": v(30.24, 56.24) * mm, "end": v(30.24, 56.21) * mm});
            skLineSegment(sketch, "E1170", {"start": v(37.45, 52.52) * mm, "end": v(37.46, 52.57) * mm});
            skLineSegment(sketch, "E1171", {"start": v(27.22, 58.16) * mm, "end": v(26.96, 58.04) * mm});
            skLineSegment(sketch, "E1172", {"start": v(36.78, 52.37) * mm, "end": v(36.76, 52.36) * mm});
            skLineSegment(sketch, "E1173", {"start": v(30.02, 61.92) * mm, "end": v(30, 61.93) * mm});
            skLineSegment(sketch, "E1174", {"start": v(26.65, 57.94) * mm, "end": v(26.1, 57.87) * mm});
            skLineSegment(sketch, "E1175", {"start": v(36.26, 52.3) * mm, "end": v(36.22, 52.37) * mm});
            skLineSegment(sketch, "E1176", {"start": v(30.84, 58.9) * mm, "end": v(30.82, 58.9) * mm});
            skLineSegment(sketch, "E1177", {"start": v(27.35, 57.07) * mm, "end": v(27.36, 57.06) * mm});
            skLineSegment(sketch, "E1178", {"start": v(35.86, 55.49) * mm, "end": v(35.88, 55.5) * mm});
            skLineSegment(sketch, "E1179", {"start": v(35.59, 52) * mm, "end": v(35.82, 51.95) * mm});
            skLineSegment(sketch, "E1180", {"start": v(32.36, 58.05) * mm, "end": v(32.38, 58.06) * mm});
            skLineSegment(sketch, "E1181", {"start": v(33.8, 57.78) * mm, "end": v(33.87, 57.96) * mm});
            skLineSegment(sketch, "E1182", {"start": v(31.56, 54.46) * mm, "end": v(31.58, 54.5) * mm});
            skLineSegment(sketch, "E1183", {"start": v(31.83, 57.86) * mm, "end": v(31.83, 57.84) * mm});
            skLineSegment(sketch, "E1184", {"start": v(33.18, 56.85) * mm, "end": v(33.2, 56.86) * mm});
            skLineSegment(sketch, "E1185", {"start": v(31.25, 55.24) * mm, "end": v(31.24, 55.23) * mm});
            skLineSegment(sketch, "E1186", {"start": v(32.22, 58.24) * mm, "end": v(32.2, 58.23) * mm});
            skLineSegment(sketch, "E1187", {"start": v(34.16, 57.2) * mm, "end": v(34.11, 57.18) * mm});
            skLineSegment(sketch, "E1188", {"start": v(33.3, 58.5) * mm, "end": v(33.18, 58.5) * mm});
            skLineSegment(sketch, "E1189", {"start": v(33, 58) * mm, "end": v(33.02, 57.98) * mm});
            skLineSegment(sketch, "E1190", {"start": v(35.8, 57.3) * mm, "end": v(35.16, 57.37) * mm});
            skLineSegment(sketch, "E1191", {"start": v(37.35, 55.44) * mm, "end": v(37.29, 55.31) * mm});
            skLineSegment(sketch, "E1192", {"start": v(36.84, 52.12) * mm, "end": v(37.06, 52.2) * mm});
            skLineSegment(sketch, "E1193", {"start": v(36.75, 54.51) * mm, "end": v(36.08, 53.6) * mm});
            skLineSegment(sketch, "E1194", {"start": v(37.46, 52.6) * mm, "end": v(37.46, 52.63) * mm});
            skLineSegment(sketch, "E1195", {"start": v(35.36, 52.3) * mm, "end": v(35.37, 52.26) * mm});
            skLineSegment(sketch, "E1196", {"start": v(36.07, 56.88) * mm, "end": v(36.07, 56.93) * mm});
            skLineSegment(sketch, "E1197", {"start": v(35.84, 51.94) * mm, "end": v(35.95, 51.93) * mm});
            skLineSegment(sketch, "E1198", {"start": v(32.04, 60.53) * mm, "end": v(32.05, 60.57) * mm});
            skLineSegment(sketch, "E1199", {"start": v(29.25, 56.2) * mm, "end": v(29.48, 56.2) * mm});
            skLineSegment(sketch, "E1200", {"start": v(27.6, 56.16) * mm, "end": v(25.7, 57.3) * mm});
            skLineSegment(sketch, "E1201", {"start": v(27.36, 62.64) * mm, "end": v(27.23, 62.58) * mm});
            skLineSegment(sketch, "E1202", {"start": v(35.58, 52) * mm, "end": v(35.59, 52) * mm});
            skLineSegment(sketch, "E1203", {"start": v(31.14, 61.32) * mm, "end": v(30.45, 61.7) * mm});
            skLineSegment(sketch, "E1204", {"start": v(30.2, 56.29) * mm, "end": v(30.23, 56.29) * mm});
            skLineSegment(sketch, "E1205", {"start": v(33.26, 53.79) * mm, "end": v(33.25, 53.77) * mm});
            skLineSegment(sketch, "E1206", {"start": v(24.69, 58.85) * mm, "end": v(24.75, 58.8) * mm});
            skLineSegment(sketch, "E1207", {"start": v(26.6, 61.82) * mm, "end": v(26.55, 61.64) * mm});
            skLineSegment(sketch, "E1208", {"start": v(36.58, 52.05) * mm, "end": v(36.6, 52.05) * mm});
            skLineSegment(sketch, "E1209", {"start": v(29.51, 59.52) * mm, "end": v(29.6, 59.47) * mm});
            skLineSegment(sketch, "E1210", {"start": v(30.23, 56.14) * mm, "end": v(30.22, 56.1) * mm});
            skLineSegment(sketch, "E1211", {"start": v(26.26, 58.24) * mm, "end": v(26.28, 58.24) * mm});
            skLineSegment(sketch, "E1212", {"start": v(25.46, 60.93) * mm, "end": v(25.55, 61.26) * mm});
            skLineSegment(sketch, "E1213", {"start": v(37.44, 52.5) * mm, "end": v(37.45, 52.52) * mm});
            skLineSegment(sketch, "E1214", {"start": v(32.23, 60.07) * mm, "end": v(32.14, 60.01) * mm});
            skLineSegment(sketch, "E1215", {"start": v(30.2, 58.72) * mm, "end": v(30.2, 58.72) * mm});
            skLineSegment(sketch, "E1216", {"start": v(29.88, 55.92) * mm, "end": v(29.87, 55.92) * mm});
            skLineSegment(sketch, "E1217", {"start": v(29.24, 62.18) * mm, "end": v(29.31, 62.3) * mm});
            skLineSegment(sketch, "E1218", {"start": v(26.29, 62.37) * mm, "end": v(26.3, 62.39) * mm});
            skLineSegment(sketch, "E1219", {"start": v(37.1, 52.5) * mm, "end": v(36.78, 52.37) * mm});
            skLineSegment(sketch, "E1220", {"start": v(31.76, 60) * mm, "end": v(31.78, 60.03) * mm});
            skLineSegment(sketch, "E1221", {"start": v(29.49, 58.86) * mm, "end": v(28.78, 59.3) * mm});
            skLineSegment(sketch, "E1222", {"start": v(28.84, 55.79) * mm, "end": v(28.8, 55.79) * mm});
            skLineSegment(sketch, "E1223", {"start": v(28.26, 62.7) * mm, "end": v(28.25, 62.7) * mm});
            skLineSegment(sketch, "E1224", {"start": v(27.12, 62.86) * mm, "end": v(27.7, 63.02) * mm});
            skLineSegment(sketch, "E1225", {"start": v(36.27, 52.3) * mm, "end": v(36.26, 52.3) * mm});
            skLineSegment(sketch, "E1226", {"start": v(32.05, 60.57) * mm, "end": v(32.04, 60.6) * mm});
            skLineSegment(sketch, "E1227", {"start": v(28.14, 59.18) * mm, "end": v(28.13, 59.17) * mm});
            skLineSegment(sketch, "E1228", {"start": v(27.73, 56.08) * mm, "end": v(27.6, 56.16) * mm});
            skLineSegment(sketch, "E1229", {"start": v(27.23, 62.58) * mm, "end": v(27.1, 62.51) * mm});
            skLineSegment(sketch, "E1230", {"start": v(38.77, 50.57) * mm, "end": v(38.76, 50.57) * mm});
            skLineSegment(sketch, "E1231", {"start": v(36.22, 52.52) * mm, "end": v(36.26, 52.6) * mm});
            skLineSegment(sketch, "E1232", {"start": v(30.45, 61.7) * mm, "end": v(30.43, 61.7) * mm});
            skLineSegment(sketch, "E1233", {"start": v(27.24, 58.17) * mm, "end": v(27.22, 58.16) * mm});
            skLineSegment(sketch, "E1234", {"start": v(24.64, 58.84) * mm, "end": v(24.69, 58.85) * mm});
            skLineSegment(sketch, "E1235", {"start": v(26.55, 61.64) * mm, "end": v(26.55, 61.62) * mm});
            skLineSegment(sketch, "E1236", {"start": v(38.13, 50.64) * mm, "end": v(38.12, 50.65) * mm});
            skLineSegment(sketch, "E1237", {"start": v(29.6, 59.47) * mm, "end": v(30.83, 58.9) * mm});
            skLineSegment(sketch, "E1238", {"start": v(26.67, 57.94) * mm, "end": v(26.65, 57.94) * mm});
            skLineSegment(sketch, "E1239", {"start": v(34.14, 56.91) * mm, "end": v(34.29, 56.97) * mm});
            skLineSegment(sketch, "E1240", {"start": v(26.17, 58.2) * mm, "end": v(26.26, 58.24) * mm});
            skLineSegment(sketch, "E1241", {"start": v(25.55, 61.26) * mm, "end": v(25.55, 61.28) * mm});
            skLineSegment(sketch, "E1242", {"start": v(37.93, 50.9) * mm, "end": v(37.93, 50.94) * mm});
            skLineSegment(sketch, "E1243", {"start": v(32.24, 60.08) * mm, "end": v(32.23, 60.07) * mm});
            skLineSegment(sketch, "E1244", {"start": v(30.2, 58.72) * mm, "end": v(30.04, 58.72) * mm});
            skLineSegment(sketch, "E1245", {"start": v(27, 57.3) * mm, "end": v(27.35, 57.07) * mm});
            skLineSegment(sketch, "E1246", {"start": v(29.87, 55.92) * mm, "end": v(29.86, 55.92) * mm});
            skLineSegment(sketch, "E1247", {"start": v(27.35, 59.42) * mm, "end": v(29.24, 62.18) * mm});
            skLineSegment(sketch, "E1248", {"start": v(36.94, 54.78) * mm, "end": v(36.79, 54.57) * mm});
            skLineSegment(sketch, "E1249", {"start": v(38.73, 52.25) * mm, "end": v(39.5, 53.3) * mm});
            skLineSegment(sketch, "E1250", {"start": v(31.83, 59.97) * mm, "end": v(31.76, 60) * mm});
            skLineSegment(sketch, "E1251", {"start": v(28.31, 56.51) * mm, "end": v(28.34, 56.5) * mm});
            skLineSegment(sketch, "E1252", {"start": v(28.8, 55.79) * mm, "end": v(28.6, 55.8) * mm});
            skLineSegment(sketch, "E1253", {"start": v(28.44, 62.67) * mm, "end": v(28.26, 62.7) * mm});
            skLineSegment(sketch, "E1254", {"start": v(35.39, 52.49) * mm, "end": v(35.37, 52.4) * mm});
            skLineSegment(sketch, "E1255", {"start": v(40.04, 54.07) * mm, "end": v(40.08, 54.14) * mm});
            skLineSegment(sketch, "E1256", {"start": v(36.53, 55.8) * mm, "end": v(36.7, 55.83) * mm});
            skLineSegment(sketch, "E1257", {"start": v(38.93, 50.6) * mm, "end": v(38.91, 50.6) * mm});
            skLineSegment(sketch, "E1258", {"start": v(37.21, 55.8) * mm, "end": v(37.24, 55.8) * mm});
            skLineSegment(sketch, "E1259", {"start": v(35.42, 55.73) * mm, "end": v(35.43, 55.74) * mm});
            skLineSegment(sketch, "E1260", {"start": v(38.45, 50.58) * mm, "end": v(38.43, 50.58) * mm});
            skLineSegment(sketch, "E1261", {"start": v(33.67, 56.67) * mm, "end": v(33.96, 56.84) * mm});
            skLineSegment(sketch, "E1262", {"start": v(37.37, 55.6) * mm, "end": v(37.37, 55.57) * mm});
            skLineSegment(sketch, "E1263", {"start": v(25.96, 58.16) * mm, "end": v(25.97, 58.16) * mm});
            skLineSegment(sketch, "E1264", {"start": v(36.06, 56.98) * mm, "end": v(36.04, 57.03) * mm});
            skLineSegment(sketch, "E1265", {"start": v(37.97, 50.8) * mm, "end": v(37.95, 50.83) * mm});
            skLineSegment(sketch, "E1266", {"start": v(34.31, 56.97) * mm, "end": v(34.47, 57) * mm});
            skLineSegment(sketch, "E1267", {"start": v(26.96, 58.87) * mm, "end": v(27.34, 59.4) * mm});
            skLineSegment(sketch, "E1268", {"start": v(37.12, 55.05) * mm, "end": v(37.1, 55.03) * mm});
            skLineSegment(sketch, "E1269", {"start": v(35.14, 57.37) * mm, "end": v(35.12, 57.37) * mm});
            skLineSegment(sketch, "E1270", {"start": v(38.03, 51.23) * mm, "end": v(38.07, 51.3) * mm});
            skLineSegment(sketch, "E1271", {"start": v(35, 56.98) * mm, "end": v(35.1, 56.86) * mm});
            skLineSegment(sketch, "E1272", {"start": v(28.79, 62.55) * mm, "end": v(28.45, 62.67) * mm});
            skLineSegment(sketch, "E1273", {"start": v(35.5, 52.74) * mm, "end": v(35.47, 52.68) * mm});
            skLineSegment(sketch, "E1274", {"start": v(33.82, 57.04) * mm, "end": v(33.25, 56.71) * mm});
            skLineSegment(sketch, "E1275", {"start": v(39.88, 53.82) * mm, "end": v(39.88, 53.83) * mm});
            skLineSegment(sketch, "E1276", {"start": v(35.14, 56.65) * mm, "end": v(35.11, 56.58) * mm});
            skLineSegment(sketch, "E1277", {"start": v(27.65, 62.72) * mm, "end": v(27.37, 62.64) * mm});
            skLineSegment(sketch, "E1278", {"start": v(35.4, 52.18) * mm, "end": v(35.43, 52.14) * mm});
            skLineSegment(sketch, "E1279", {"start": v(33.37, 57.12) * mm, "end": v(33.38, 57.14) * mm});
            skLineSegment(sketch, "E1280", {"start": v(34.65, 55.82) * mm, "end": v(33.45, 54.07) * mm});
            skLineSegment(sketch, "E1281", {"start": v(26.7, 62.03) * mm, "end": v(26.61, 61.84) * mm});
            skLineSegment(sketch, "E1282", {"start": v(36.32, 51.97) * mm, "end": v(36.33, 51.98) * mm});
            skLineSegment(sketch, "E1283", {"start": v(33.89, 58.05) * mm, "end": v(33.9, 58.1) * mm});
            skLineSegment(sketch, "E1284", {"start": v(33.76, 53.3) * mm, "end": v(33.79, 53.33) * mm});
            skLineSegment(sketch, "E1285", {"start": v(25.5, 60.91) * mm, "end": v(25.45, 60.9) * mm});
            skLineSegment(sketch, "E1286", {"start": v(37.17, 52.27) * mm, "end": v(37.26, 52.34) * mm});
            skLineSegment(sketch, "E1287", {"start": v(33.84, 58.26) * mm, "end": v(33.82, 58.3) * mm});
            skLineSegment(sketch, "E1288", {"start": v(35.06, 54.95) * mm, "end": v(35.08, 54.97) * mm});
            skLineSegment(sketch, "E1289", {"start": v(26.08, 62.14) * mm, "end": v(26.1, 62.15) * mm});
            skLineSegment(sketch, "E1290", {"start": v(32.94, 58.46) * mm, "end": v(32.93, 58.46) * mm});
            skLineSegment(sketch, "E1291", {"start": v(36.18, 55.66) * mm, "end": v(36.2, 55.67) * mm});
            skLineSegment(sketch, "E1292", {"start": v(26.8, 62.73) * mm, "end": v(27.08, 62.84) * mm});
            skLineSegment(sketch, "E1293", {"start": v(32.2, 58.23) * mm, "end": v(32.11, 58.18) * mm});
            skLineSegment(sketch, "E1294", {"start": v(33.38, 57.14) * mm, "end": v(33.6, 57.46) * mm});
            skLineSegment(sketch, "E1295", {"start": v(33.9, 58.1) * mm, "end": v(33.9, 58.14) * mm});
            skLineSegment(sketch, "E1296", {"start": v(33.82, 58.3) * mm, "end": v(33.68, 58.43) * mm});
            skLineSegment(sketch, "E1297", {"start": v(32.93, 58.46) * mm, "end": v(32.92, 58.45) * mm});
            skLineSegment(sketch, "E1298", {"start": v(32.11, 58.18) * mm, "end": v(32.02, 58.1) * mm});
            skLineSegment(sketch, "E1299", {"start": v(36.75, 56.1) * mm, "end": v(36.73, 56.09) * mm});
            skLineSegment(sketch, "E1300", {"start": v(31.84, 57.8) * mm, "end": v(31.86, 57.74) * mm});
            skLineSegment(sketch, "E1301", {"start": v(35.67, 56.1) * mm, "end": v(35.91, 56.48) * mm});
            skLineSegment(sketch, "E1302", {"start": v(32.65, 58.11) * mm, "end": v(32.93, 58.1) * mm});
            skLineSegment(sketch, "E1303", {"start": v(36.02, 57.07) * mm, "end": v(36, 57.12) * mm});
            skLineSegment(sketch, "E1304", {"start": v(34.8, 57.37) * mm, "end": v(34.78, 57.36) * mm});
            skLineSegment(sketch, "E1305", {"start": v(33.2, 56.69) * mm, "end": v(33.2, 56.68) * mm});
            skLineSegment(sketch, "E1306", {"start": v(33.18, 60.91) * mm, "end": v(33.2, 60.9) * mm});
            skLineSegment(sketch, "E1307", {"start": v(33.79, 57.77) * mm, "end": v(33.8, 57.78) * mm});
            skLineSegment(sketch, "E1308", {"start": v(32.1, 59.98) * mm, "end": v(32.04, 59.96) * mm});
            skLineSegment(sketch, "E1309", {"start": v(38.23, 55.92) * mm, "end": v(38.2, 55.96) * mm});
            skLineSegment(sketch, "E1310", {"start": v(32, 60.32) * mm, "end": v(32, 60.34) * mm});
            skLineSegment(sketch, "E1311", {"start": v(37.54, 56.23) * mm, "end": v(37.4, 56.23) * mm});
            skLineSegment(sketch, "E1312", {"start": v(32.03, 60.64) * mm, "end": v(32.02, 60.67) * mm});
            skLineSegment(sketch, "E1313", {"start": v(28.34, 63.03) * mm, "end": v(28.36, 63.03) * mm});
            skLineSegment(sketch, "E1314", {"start": v(29.52, 62.75) * mm, "end": v(29.56, 62.73) * mm});
            skLineSegment(sketch, "E1315", {"start": v(33.88, 58.18) * mm, "end": v(33.87, 58.22) * mm});
            skLineSegment(sketch, "E1316", {"start": v(33.43, 58.49) * mm, "end": v(33.41, 58.49) * mm});
            skLineSegment(sketch, "E1317", {"start": v(34.45, 57.3) * mm, "end": v(34.16, 57.2) * mm});
            skLineSegment(sketch, "E1318", {"start": v(33, 56.57) * mm, "end": v(33.18, 56.85) * mm});
            skLineSegment(sketch, "E1319", {"start": v(35.12, 55.25) * mm, "end": v(35.07, 55.22) * mm});
            skLineSegment(sketch, "E1320", {"start": v(31.84, 57.94) * mm, "end": v(31.83, 57.89) * mm});
            skLineSegment(sketch, "E1321", {"start": v(36.03, 56.72) * mm, "end": v(36.06, 56.82) * mm});
            skLineSegment(sketch, "E1322", {"start": v(32.44, 58.32) * mm, "end": v(32.43, 58.32) * mm});
            skLineSegment(sketch, "E1323", {"start": v(35.83, 57.3) * mm, "end": v(35.8, 57.3) * mm});
            skLineSegment(sketch, "E1324", {"start": v(34.44, 54.29) * mm, "end": v(34.72, 54.62) * mm});
            skLineSegment(sketch, "E1325", {"start": v(33.06, 53.48) * mm, "end": v(32.98, 53.37) * mm});
            skLineSegment(sketch, "E1326", {"start": v(34.85, 56.12) * mm, "end": v(34.84, 56.1) * mm});
            skLineSegment(sketch, "E1327", {"start": v(35.14, 56.75) * mm, "end": v(35.15, 56.72) * mm});
            skLineSegment(sketch, "E1328", {"start": v(32.48, 57.05) * mm, "end": v(31.25, 55.24) * mm});
            skLineSegment(sketch, "E1329", {"start": v(34.64, 57.01) * mm, "end": v(34.65, 57.01) * mm});
            skLineSegment(sketch, "E1330", {"start": v(32.12, 57.93) * mm, "end": v(32.24, 58) * mm});
            skLineSegment(sketch, "E1331", {"start": v(30.8, 54.54) * mm, "end": v(31.56, 54.46) * mm});
            skLineSegment(sketch, "E1332", {"start": v(32.98, 58.06) * mm, "end": v(33, 58.02) * mm});
            skLineSegment(sketch, "E1333", {"start": v(32.85, 56.12) * mm, "end": v(32.87, 56.14) * mm});
            skLineSegment(sketch, "E1334", {"start": v(32.94, 57.76) * mm, "end": v(32.94, 57.75) * mm});
            skLineSegment(sketch, "E1335", {"start": v(34.29, 56.97) * mm, "end": v(34.3, 56.97) * mm});
            skLineSegment(sketch, "E1336", {"start": v(46.8, 55.86) * mm, "end": v(46.54, 55.92) * mm});
            skLineSegment(sketch, "E1337", {"start": v(40.39, 50.1) * mm, "end": v(40.38, 50.1) * mm});
            skLineSegment(sketch, "E1338", {"start": v(40.26, 49.72) * mm, "end": v(40.27, 49.68) * mm});
            skLineSegment(sketch, "E1339", {"start": v(40.27, 49.68) * mm, "end": v(40.28, 49.64) * mm});
            skLineSegment(sketch, "E1340", {"start": v(40.41, 50.15) * mm, "end": v(40.39, 50.1) * mm});
            skLineSegment(sketch, "E1341", {"start": v(44.16, 55.19) * mm, "end": v(43.9, 55) * mm});
            skLineSegment(sketch, "E1342", {"start": v(42.94, 53.91) * mm, "end": v(42.87, 53.8) * mm});
            skLineSegment(sketch, "E1343", {"start": v(44.44, 55.36) * mm, "end": v(44.16, 55.19) * mm});
            skLineSegment(sketch, "E1344", {"start": v(47.62, 55.53) * mm, "end": v(47.6, 55.54) * mm});
            skLineSegment(sketch, "E1345", {"start": v(47.8, 55.4) * mm, "end": v(47.62, 55.53) * mm});
            skLineSegment(sketch, "E1346", {"start": v(46.64, 55.28) * mm, "end": v(46.65, 55.27) * mm});
            skLineSegment(sketch, "E1347", {"start": v(46.42, 55.41) * mm, "end": v(46.64, 55.28) * mm});
            skLineSegment(sketch, "E1348", {"start": v(45.96, 55.58) * mm, "end": v(45.97, 55.58) * mm});
            skLineSegment(sketch, "E1349", {"start": v(45.82, 55.6) * mm, "end": v(45.96, 55.58) * mm});
            skLineSegment(sketch, "E1350", {"start": v(45.5, 55.56) * mm, "end": v(45.52, 55.57) * mm});
            skLineSegment(sketch, "E1351", {"start": v(45.22, 55.48) * mm, "end": v(45.5, 55.56) * mm});
            skLineSegment(sketch, "E1352", {"start": v(44.51, 54.9) * mm, "end": v(44.82, 55.18) * mm});
            skLineSegment(sketch, "E1353", {"start": v(44.5, 54.88) * mm, "end": v(44.51, 54.9) * mm});
            skLineSegment(sketch, "E1354", {"start": v(41.63, 50.76) * mm, "end": v(41.72, 50.9) * mm});
            skLineSegment(sketch, "E1355", {"start": v(41.6, 50.72) * mm, "end": v(41.63, 50.76) * mm});
            skLineSegment(sketch, "E1356", {"start": v(41.97, 49.62) * mm, "end": v(41.98, 49.63) * mm});
            skLineSegment(sketch, "E1357", {"start": v(42.36, 49.97) * mm, "end": v(42.37, 50.02) * mm});
            skLineSegment(sketch, "E1358", {"start": v(41.15, 49.96) * mm, "end": v(41.17, 50.02) * mm});
            skLineSegment(sketch, "E1359", {"start": v(41.19, 49.73) * mm, "end": v(41.17, 49.79) * mm});
            skLineSegment(sketch, "E1360", {"start": v(41.45, 44.64) * mm, "end": v(41.42, 44.64) * mm});
            skLineSegment(sketch, "E1361", {"start": v(39.96, 45.21) * mm, "end": v(39.94, 45.23) * mm});
            skLineSegment(sketch, "E1362", {"start": v(42.35, 50.13) * mm, "end": v(42.32, 50.19) * mm});
            skLineSegment(sketch, "E1363", {"start": v(39.69, 45.47) * mm, "end": v(39.68, 45.48) * mm});
            skLineSegment(sketch, "E1364", {"start": v(41.2, 49.73) * mm, "end": v(41.19, 49.73) * mm});
            skLineSegment(sketch, "E1365", {"start": v(42.89, 55.95) * mm, "end": v(42.9, 55.98) * mm});
            skLineSegment(sketch, "E1366", {"start": v(41.58, 49.74) * mm, "end": v(41.51, 49.72) * mm});
            skLineSegment(sketch, "E1367", {"start": v(41.14, 49.93) * mm, "end": v(41.15, 49.96) * mm});
            skLineSegment(sketch, "E1368", {"start": v(41.7, 49.78) * mm, "end": v(41.58, 49.74) * mm});
            skLineSegment(sketch, "E1369", {"start": v(42.32, 50.19) * mm, "end": v(42.3, 50.17) * mm});
            skLineSegment(sketch, "E1370", {"start": v(42.37, 50.02) * mm, "end": v(42.38, 50.05) * mm});
            skLineSegment(sketch, "E1371", {"start": v(40.52, 45.78) * mm, "end": v(40.54, 45.76) * mm});
            skLineSegment(sketch, "E1372", {"start": v(40.72, 49.34) * mm, "end": v(40.73, 49.34) * mm});
            skLineSegment(sketch, "E1373", {"start": v(41.24, 49.38) * mm, "end": v(41.49, 49.44) * mm});
            skLineSegment(sketch, "E1374", {"start": v(41.42, 44.64) * mm, "end": v(41.07, 44.73) * mm});
            skLineSegment(sketch, "E1375", {"start": v(41.98, 49.63) * mm, "end": v(42.08, 49.7) * mm});
            skLineSegment(sketch, "E1376", {"start": v(40.48, 49.4) * mm, "end": v(40.72, 49.34) * mm});
            skLineSegment(sketch, "E1377", {"start": v(41.23, 49.37) * mm, "end": v(41.24, 49.38) * mm});
            skLineSegment(sketch, "E1378", {"start": v(40.54, 45.76) * mm, "end": v(40.85, 45.43) * mm});
            skLineSegment(sketch, "E1379", {"start": v(40.25, 45.01) * mm, "end": v(39.96, 45.21) * mm});
            skLineSegment(sketch, "E1380", {"start": v(42.6, 44.69) * mm, "end": v(42.24, 44.63) * mm});
            skLineSegment(sketch, "E1381", {"start": v(43.33, 44.89) * mm, "end": v(42.6, 44.69) * mm});
            skLineSegment(sketch, "E1382", {"start": v(44.7, 45.73) * mm, "end": v(44.66, 45.7) * mm});
            skLineSegment(sketch, "E1383", {"start": v(45.85, 46.95) * mm, "end": v(45.76, 46.85) * mm});
            skLineSegment(sketch, "E1384", {"start": v(47.85, 50.54) * mm, "end": v(47.88, 50.57) * mm});
            skLineSegment(sketch, "E1385", {"start": v(44.66, 45.7) * mm, "end": v(44.08, 45.3) * mm});
            skLineSegment(sketch, "E1386", {"start": v(47.88, 49.44) * mm, "end": v(45.85, 46.95) * mm});
            skLineSegment(sketch, "E1387", {"start": v(43.8, 51.72) * mm, "end": v(43.8, 51.75) * mm});
            skLineSegment(sketch, "E1388", {"start": v(44.79, 48.2) * mm, "end": v(44.8, 48.2) * mm});
            skLineSegment(sketch, "E1389", {"start": v(44.38, 48.54) * mm, "end": v(44.38, 48.48) * mm});
            skLineSegment(sketch, "E1390", {"start": v(47.88, 50.57) * mm, "end": v(48.75, 50.43) * mm});
            skLineSegment(sketch, "E1391", {"start": v(45.28, 48.3) * mm, "end": v(45.42, 48.37) * mm});
            skLineSegment(sketch, "E1392", {"start": v(45.13, 48.25) * mm, "end": v(45.28, 48.3) * mm});
            skLineSegment(sketch, "E1393", {"start": v(45.8, 48.59) * mm, "end": v(46.54, 49.09) * mm});
            skLineSegment(sketch, "E1394", {"start": v(44.8, 48.2) * mm, "end": v(44.95, 48.2) * mm});
            skLineSegment(sketch, "E1395", {"start": v(46.54, 49.09) * mm, "end": v(46.57, 49.1) * mm});
            skLineSegment(sketch, "E1396", {"start": v(44.55, 52.2) * mm, "end": v(44.77, 52.24) * mm});
            skLineSegment(sketch, "E1397", {"start": v(44.38, 48.6) * mm, "end": v(44.38, 48.54) * mm});
            skLineSegment(sketch, "E1398", {"start": v(43.84, 51.58) * mm, "end": v(43.81, 51.63) * mm});
            skLineSegment(sketch, "E1399", {"start": v(43.8, 51.75) * mm, "end": v(43.81, 51.8) * mm});
            skLineSegment(sketch, "E1400", {"start": v(44.5, 48.98) * mm, "end": v(44.45, 48.87) * mm});
            skLineSegment(sketch, "E1401", {"start": v(44.62, 49.2) * mm, "end": v(44.5, 48.98) * mm});
            skLineSegment(sketch, "E1402", {"start": v(45.55, 51.23) * mm, "end": v(45.36, 50.8) * mm});
            skLineSegment(sketch, "E1403", {"start": v(45.56, 51.26) * mm, "end": v(45.55, 51.23) * mm});
            skLineSegment(sketch, "E1404", {"start": v(45.65, 51.98) * mm, "end": v(45.66, 51.96) * mm});
            skLineSegment(sketch, "E1405", {"start": v(45.63, 52.02) * mm, "end": v(45.65, 51.98) * mm});
            skLineSegment(sketch, "E1406", {"start": v(45.42, 52.2) * mm, "end": v(45.44, 52.2) * mm});
            skLineSegment(sketch, "E1407", {"start": v(45.22, 52.25) * mm, "end": v(45.42, 52.2) * mm});
            skLineSegment(sketch, "E1408", {"start": v(44.77, 52.24) * mm, "end": v(44.79, 52.24) * mm});
            skLineSegment(sketch, "E1409", {"start": v(44.14, 52.06) * mm, "end": v(44.15, 52.07) * mm});
            skLineSegment(sketch, "E1410", {"start": v(43.81, 51.63) * mm, "end": v(43.8, 51.67) * mm});
            skLineSegment(sketch, "E1411", {"start": v(44.06, 52.02) * mm, "end": v(44.14, 52.06) * mm});
            skLineSegment(sketch, "E1412", {"start": v(43.8, 51.67) * mm, "end": v(43.8, 51.7) * mm});
            skLineSegment(sketch, "E1413", {"start": v(44.99, 52.27) * mm, "end": v(45.1, 52.27) * mm});
            skLineSegment(sketch, "E1414", {"start": v(44.15, 52.07) * mm, "end": v(44.33, 52.14) * mm});
            skLineSegment(sketch, "E1415", {"start": v(43.85, 51.6) * mm, "end": v(43.84, 51.58) * mm});
            skLineSegment(sketch, "E1416", {"start": v(44.37, 51.88) * mm, "end": v(44.3, 51.86) * mm});
            skLineSegment(sketch, "E1417", {"start": v(44.44, 51.9) * mm, "end": v(44.37, 51.88) * mm});
            skLineSegment(sketch, "E1418", {"start": v(44.9, 51.66) * mm, "end": v(44.9, 51.67) * mm});
            skLineSegment(sketch, "E1419", {"start": v(44.91, 51.6) * mm, "end": v(44.9, 51.66) * mm});
            skLineSegment(sketch, "E1420", {"start": v(44.83, 51.25) * mm, "end": v(44.87, 51.35) * mm});
            skLineSegment(sketch, "E1421", {"start": v(44.73, 51.06) * mm, "end": v(44.83, 51.25) * mm});
            skLineSegment(sketch, "E1422", {"start": v(43.95, 49.44) * mm, "end": v(44.52, 50.64) * mm});
            skLineSegment(sketch, "E1423", {"start": v(43.94, 49.41) * mm, "end": v(43.95, 49.44) * mm});
            skLineSegment(sketch, "E1424", {"start": v(44.55, 50.69) * mm, "end": v(44.71, 51.03) * mm});
            skLineSegment(sketch, "E1425", {"start": v(43.52, 48.52) * mm, "end": v(43.66, 48.8) * mm});
            skLineSegment(sketch, "E1426", {"start": v(44.9, 51.45) * mm, "end": v(44.9, 51.5) * mm});
            skLineSegment(sketch, "E1427", {"start": v(44.52, 50.64) * mm, "end": v(44.55, 50.69) * mm});
            skLineSegment(sketch, "E1428", {"start": v(44.83, 51.86) * mm, "end": v(44.81, 51.87) * mm});
            skLineSegment(sketch, "E1429", {"start": v(44.87, 51.35) * mm, "end": v(44.9, 51.45) * mm});
            skLineSegment(sketch, "E1430", {"start": v(44.19, 51.8) * mm, "end": v(44.08, 51.75) * mm});
            skLineSegment(sketch, "E1431", {"start": v(44.9, 51.67) * mm, "end": v(44.83, 51.86) * mm});
            skLineSegment(sketch, "E1432", {"start": v(44.3, 51.86) * mm, "end": v(44.19, 51.8) * mm});
            skLineSegment(sketch, "E1433", {"start": v(43.82, 51.82) * mm, "end": v(43.97, 51.95) * mm});
            skLineSegment(sketch, "E1434", {"start": v(41.5, 49.45) * mm, "end": v(41.74, 49.52) * mm});
            skLineSegment(sketch, "E1435", {"start": v(44.33, 52.14) * mm, "end": v(44.35, 52.14) * mm});
            skLineSegment(sketch, "E1436", {"start": v(43.81, 51.8) * mm, "end": v(43.82, 51.82) * mm});
            skLineSegment(sketch, "E1437", {"start": v(45.54, 52.12) * mm, "end": v(45.59, 52.07) * mm});
            skLineSegment(sketch, "E1438", {"start": v(44.79, 52.24) * mm, "end": v(44.99, 52.27) * mm});
            skLineSegment(sketch, "E1439", {"start": v(45.67, 51.9) * mm, "end": v(45.68, 51.76) * mm});
            skLineSegment(sketch, "E1440", {"start": v(45.44, 52.2) * mm, "end": v(45.54, 52.12) * mm});
            skLineSegment(sketch, "E1441", {"start": v(45.36, 50.78) * mm, "end": v(44.66, 49.29) * mm});
            skLineSegment(sketch, "E1442", {"start": v(45.66, 51.96) * mm, "end": v(45.67, 51.9) * mm});
            skLineSegment(sketch, "E1443", {"start": v(44.44, 48.85) * mm, "end": v(44.4, 48.73) * mm});
            skLineSegment(sketch, "E1444", {"start": v(45.36, 50.8) * mm, "end": v(45.36, 50.78) * mm});
            skLineSegment(sketch, "E1445", {"start": v(44.39, 48.46) * mm, "end": v(44.45, 48.22) * mm});
            skLineSegment(sketch, "E1446", {"start": v(44.45, 48.87) * mm, "end": v(44.44, 48.85) * mm});
            skLineSegment(sketch, "E1447", {"start": v(44.96, 48.2) * mm, "end": v(45.11, 48.24) * mm});
            skLineSegment(sketch, "E1448", {"start": v(44.38, 48.48) * mm, "end": v(44.39, 48.46) * mm});
            skLineSegment(sketch, "E1449", {"start": v(45.44, 48.38) * mm, "end": v(45.72, 48.54) * mm});
            skLineSegment(sketch, "E1450", {"start": v(44.95, 48.2) * mm, "end": v(44.96, 48.2) * mm});
            skLineSegment(sketch, "E1451", {"start": v(40.87, 45.42) * mm, "end": v(41.24, 45.17) * mm});
            skLineSegment(sketch, "E1452", {"start": v(40.85, 45.43) * mm, "end": v(40.87, 45.42) * mm});
            skLineSegment(sketch, "E1453", {"start": v(47.2, 49.74) * mm, "end": v(47.22, 49.76) * mm});
            skLineSegment(sketch, "E1454", {"start": v(45.42, 48.37) * mm, "end": v(45.44, 48.38) * mm});
            skLineSegment(sketch, "E1455", {"start": v(42.17, 49.77) * mm, "end": v(42.18, 49.78) * mm});
            skLineSegment(sketch, "E1456", {"start": v(48.79, 50.43) * mm, "end": v(48.73, 50.37) * mm});
            skLineSegment(sketch, "E1457", {"start": v(41.07, 44.73) * mm, "end": v(41.01, 44.74) * mm});
            skLineSegment(sketch, "E1458", {"start": v(40.73, 49.34) * mm, "end": v(40.85, 49.33) * mm});
            skLineSegment(sketch, "E1459", {"start": v(46.57, 49.1) * mm, "end": v(47.2, 49.74) * mm});
            skLineSegment(sketch, "E1460", {"start": v(45.27, 46.28) * mm, "end": v(45.25, 46.26) * mm});
            skLineSegment(sketch, "E1461", {"start": v(48.75, 50.43) * mm, "end": v(48.79, 50.43) * mm});
            skLineSegment(sketch, "E1462", {"start": v(44.04, 45.27) * mm, "end": v(43.4, 44.92) * mm});
            skLineSegment(sketch, "E1463", {"start": v(45.76, 46.85) * mm, "end": v(45.27, 46.28) * mm});
            skLineSegment(sketch, "E1464", {"start": v(42.19, 44.62) * mm, "end": v(41.83, 44.6) * mm});
            skLineSegment(sketch, "E1465", {"start": v(44.08, 45.3) * mm, "end": v(44.04, 45.27) * mm});
            skLineSegment(sketch, "E1466", {"start": v(41.01, 44.74) * mm, "end": v(40.3, 44.99) * mm});
            skLineSegment(sketch, "E1467", {"start": v(42.24, 44.63) * mm, "end": v(42.19, 44.62) * mm});
            skLineSegment(sketch, "E1468", {"start": v(39.94, 45.23) * mm, "end": v(39.69, 45.47) * mm});
            skLineSegment(sketch, "E1469", {"start": v(42.65, 56.02) * mm, "end": v(42.63, 56.02) * mm});
            skLineSegment(sketch, "E1470", {"start": v(40.85, 49.33) * mm, "end": v(40.98, 49.33) * mm});
            skLineSegment(sketch, "E1471", {"start": v(41.49, 49.44) * mm, "end": v(41.5, 49.45) * mm});
            skLineSegment(sketch, "E1472", {"start": v(42.38, 50.07) * mm, "end": v(42.37, 50.08) * mm});
            skLineSegment(sketch, "E1473", {"start": v(42.08, 49.7) * mm, "end": v(42.17, 49.77) * mm});
            skLineSegment(sketch, "E1474", {"start": v(42.04, 49.96) * mm, "end": v(42.03, 49.95) * mm});
            skLineSegment(sketch, "E1475", {"start": v(42.38, 50.05) * mm, "end": v(42.38, 50.07) * mm});
            skLineSegment(sketch, "E1476", {"start": v(41.45, 49.7) * mm, "end": v(41.39, 49.7) * mm});
            skLineSegment(sketch, "E1477", {"start": v(42.3, 50.17) * mm, "end": v(42.04, 49.96) * mm});
            skLineSegment(sketch, "E1478", {"start": v(41.15, 49.84) * mm, "end": v(41.14, 49.88) * mm});
            skLineSegment(sketch, "E1479", {"start": v(41.51, 49.72) * mm, "end": v(41.45, 49.7) * mm});
            skLineSegment(sketch, "E1480", {"start": v(41.2, 50.08) * mm, "end": v(41.26, 50.18) * mm});
            skLineSegment(sketch, "E1481", {"start": v(41.17, 49.79) * mm, "end": v(41.15, 49.84) * mm});
            skLineSegment(sketch, "E1482", {"start": v(43.95, 54.16) * mm, "end": v(43.96, 54.19) * mm});
            skLineSegment(sketch, "E1483", {"start": v(41.17, 50.02) * mm, "end": v(41.2, 50.08) * mm});
            skLineSegment(sketch, "E1484", {"start": v(44.84, 55.2) * mm, "end": v(44.85, 55.2) * mm});
            skLineSegment(sketch, "E1485", {"start": v(41.72, 50.9) * mm, "end": v(43.95, 54.16) * mm});
            skLineSegment(sketch, "E1486", {"start": v(45.66, 55.6) * mm, "end": v(45.67, 55.6) * mm});
            skLineSegment(sketch, "E1487", {"start": v(44.82, 55.18) * mm, "end": v(44.84, 55.2) * mm});
            skLineSegment(sketch, "E1488", {"start": v(46.11, 55.54) * mm, "end": v(46.12, 55.53) * mm});
            skLineSegment(sketch, "E1489", {"start": v(45.52, 55.57) * mm, "end": v(45.66, 55.6) * mm});
            skLineSegment(sketch, "E1490", {"start": v(46.84, 55.1) * mm, "end": v(46.86, 55.1) * mm});
            skLineSegment(sketch, "E1491", {"start": v(45.97, 55.58) * mm, "end": v(46.11, 55.54) * mm});
            skLineSegment(sketch, "E1492", {"start": v(47.4, 55.66) * mm, "end": v(47.37, 55.67) * mm});
            skLineSegment(sketch, "E1493", {"start": v(40.28, 49.64) * mm, "end": v(40.3, 49.6) * mm});
            skLineSegment(sketch, "E1494", {"start": v(42.63, 56.02) * mm, "end": v(42.39, 55.97) * mm});
            skLineSegment(sketch, "E1495", {"start": v(46.65, 55.27) * mm, "end": v(46.84, 55.1) * mm});
            skLineSegment(sketch, "E1496", {"start": v(46.26, 55.95) * mm, "end": v(46.24, 55.95) * mm});
            skLineSegment(sketch, "E1497", {"start": v(41, 55.27) * mm, "end": v(41.03, 55.27) * mm});
            skLineSegment(sketch, "E1498", {"start": v(42.91, 56.02) * mm, "end": v(42.91, 56.06) * mm});
            skLineSegment(sketch, "E1499", {"start": v(42.39, 55.97) * mm, "end": v(42.37, 55.97) * mm});
            skLineSegment(sketch, "E1500", {"start": v(42.9, 56) * mm, "end": v(42.91, 56.02) * mm});
            skLineSegment(sketch, "E1501", {"start": v(40.3, 49.6) * mm, "end": v(40.33, 49.56) * mm});
            skLineSegment(sketch, "E1502", {"start": v(47.6, 55.54) * mm, "end": v(47.4, 55.66) * mm});
            skLineSegment(sketch, "E1503", {"start": v(45.1, 55.7) * mm, "end": v(45.06, 55.69) * mm});
            skLineSegment(sketch, "E1504", {"start": v(46.53, 55.92) * mm, "end": v(46.26, 55.95) * mm});
            skLineSegment(sketch, "E1505", {"start": v(43.87, 54.96) * mm, "end": v(43.41, 54.5) * mm});
            skLineSegment(sketch, "E1506", {"start": v(45.13, 55.72) * mm, "end": v(45.1, 55.7) * mm});
            skLineSegment(sketch, "E1507", {"start": v(41.02, 51.09) * mm, "end": v(41, 51.07) * mm});
            skLineSegment(sketch, "E1508", {"start": v(43.9, 55) * mm, "end": v(43.87, 54.96) * mm});
            skLineSegment(sketch, "E1509", {"start": v(40.3, 49.91) * mm, "end": v(40.27, 49.82) * mm});
            skLineSegment(sketch, "E1510", {"start": v(42.87, 53.8) * mm, "end": v(41.02, 51.09) * mm});
            skLineSegment(sketch, "E1511", {"start": v(41.03, 55.27) * mm, "end": v(41.52, 55.3) * mm});
            skLineSegment(sketch, "E1512", {"start": v(40.38, 50.1) * mm, "end": v(40.3, 49.91) * mm});
            skLineSegment(sketch, "E1513", {"start": v(42.04, 55.4) * mm, "end": v(42.26, 55.49) * mm});
            skLineSegment(sketch, "E1514", {"start": v(42.03, 55.4) * mm, "end": v(42.04, 55.4) * mm});
            skLineSegment(sketch, "E1515", {"start": v(42.86, 55.93) * mm, "end": v(42.89, 55.95) * mm});
            skLineSegment(sketch, "E1516", {"start": v(42.9, 56.1) * mm, "end": v(42.65, 56.02) * mm});
            skLineSegment(sketch, "E1517", {"start": v(42.9, 55.98) * mm, "end": v(42.9, 56) * mm});
            skLineSegment(sketch, "E1518", {"start": v(43.37, 54.45) * mm, "end": v(42.94, 53.91) * mm});
            skLineSegment(sketch, "E1519", {"start": v(41.83, 55.97) * mm, "end": v(41.8, 55.94) * mm});
            skLineSegment(sketch, "E1520", {"start": v(41.8, 55.94) * mm, "end": v(41, 55.27) * mm});
            skLineSegment(sketch, "E1521", {"start": v(46.54, 55.92) * mm, "end": v(46.53, 55.92) * mm});
            skLineSegment(sketch, "E1522", {"start": v(41.79, 55.34) * mm, "end": v(42.01, 55.4) * mm});
            skLineSegment(sketch, "E1523", {"start": v(42.01, 55.4) * mm, "end": v(42.03, 55.4) * mm});
            skLineSegment(sketch, "E1524", {"start": v(45.94, 55.92) * mm, "end": v(45.67, 55.87) * mm});
            skLineSegment(sketch, "E1525", {"start": v(45.67, 55.87) * mm, "end": v(45.13, 55.72) * mm});
            skLineSegment(sketch, "E1526", {"start": v(42.47, 55.62) * mm, "end": v(42.49, 55.63) * mm});
            skLineSegment(sketch, "E1527", {"start": v(42.49, 55.63) * mm, "end": v(42.86, 55.93) * mm});
            skLineSegment(sketch, "E1528", {"start": v(42.26, 55.49) * mm, "end": v(42.27, 55.5) * mm});
            skLineSegment(sketch, "E1529", {"start": v(41.52, 55.3) * mm, "end": v(41.55, 55.3) * mm});
            skLineSegment(sketch, "E1530", {"start": v(42.27, 55.5) * mm, "end": v(42.47, 55.62) * mm});
            skLineSegment(sketch, "E1531", {"start": v(42.37, 55.97) * mm, "end": v(41.86, 55.97) * mm});
            skLineSegment(sketch, "E1532", {"start": v(41.55, 55.3) * mm, "end": v(41.79, 55.34) * mm});
            skLineSegment(sketch, "E1533", {"start": v(42.91, 56.06) * mm, "end": v(42.91, 56.1) * mm});
            skLineSegment(sketch, "E1534", {"start": v(41.86, 55.97) * mm, "end": v(41.83, 55.97) * mm});
            skLineSegment(sketch, "E1535", {"start": v(40.33, 49.56) * mm, "end": v(40.46, 49.4) * mm});
            skLineSegment(sketch, "E1536", {"start": v(42.91, 56.1) * mm, "end": v(42.9, 56.1) * mm});
            skLineSegment(sketch, "E1537", {"start": v(40.27, 49.82) * mm, "end": v(40.26, 49.77) * mm});
            skLineSegment(sketch, "E1538", {"start": v(40.46, 49.4) * mm, "end": v(40.47, 49.4) * mm});
            skLineSegment(sketch, "E1539", {"start": v(41, 51.07) * mm, "end": v(40.77, 50.73) * mm});
            skLineSegment(sketch, "E1540", {"start": v(40.26, 49.77) * mm, "end": v(40.26, 49.72) * mm});
            skLineSegment(sketch, "E1541", {"start": v(43.41, 54.5) * mm, "end": v(43.39, 54.47) * mm});
            skLineSegment(sketch, "E1542", {"start": v(40.77, 50.73) * mm, "end": v(40.41, 50.15) * mm});
            skLineSegment(sketch, "E1543", {"start": v(45.06, 55.69) * mm, "end": v(44.48, 55.38) * mm});
            skLineSegment(sketch, "E1544", {"start": v(43.39, 54.47) * mm, "end": v(43.37, 54.45) * mm});
            skLineSegment(sketch, "E1545", {"start": v(46.24, 55.95) * mm, "end": v(45.98, 55.93) * mm});
            skLineSegment(sketch, "E1546", {"start": v(44.48, 55.38) * mm, "end": v(44.44, 55.36) * mm});
            skLineSegment(sketch, "E1547", {"start": v(47.37, 55.67) * mm, "end": v(46.85, 55.85) * mm});
            skLineSegment(sketch, "E1548", {"start": v(45.98, 55.93) * mm, "end": v(45.94, 55.92) * mm});
            skLineSegment(sketch, "E1549", {"start": v(46.86, 55.1) * mm, "end": v(46.9, 55.1) * mm});
            skLineSegment(sketch, "E1550", {"start": v(46.85, 55.85) * mm, "end": v(46.8, 55.86) * mm});
            skLineSegment(sketch, "E1551", {"start": v(46.12, 55.53) * mm, "end": v(46.4, 55.42) * mm});
            skLineSegment(sketch, "E1552", {"start": v(46.9, 55.1) * mm, "end": v(47.8, 55.4) * mm});
            skLineSegment(sketch, "E1553", {"start": v(45.67, 55.6) * mm, "end": v(45.81, 55.6) * mm});
            skLineSegment(sketch, "E1554", {"start": v(46.4, 55.42) * mm, "end": v(46.42, 55.41) * mm});
            skLineSegment(sketch, "E1555", {"start": v(44.85, 55.2) * mm, "end": v(45.2, 55.47) * mm});
            skLineSegment(sketch, "E1556", {"start": v(45.81, 55.6) * mm, "end": v(45.82, 55.6) * mm});
            skLineSegment(sketch, "E1557", {"start": v(43.96, 54.19) * mm, "end": v(44.47, 54.86) * mm});
            skLineSegment(sketch, "E1558", {"start": v(45.2, 55.47) * mm, "end": v(45.22, 55.48) * mm});
            skLineSegment(sketch, "E1559", {"start": v(41.26, 50.18) * mm, "end": v(41.27, 50.2) * mm});
            skLineSegment(sketch, "E1560", {"start": v(44.47, 54.86) * mm, "end": v(44.5, 54.88) * mm});
            skLineSegment(sketch, "E1561", {"start": v(41.14, 49.88) * mm, "end": v(41.14, 49.9) * mm});
            skLineSegment(sketch, "E1562", {"start": v(41.27, 50.2) * mm, "end": v(41.6, 50.72) * mm});
            skLineSegment(sketch, "E1563", {"start": v(41.39, 49.7) * mm, "end": v(41.33, 49.7) * mm});
            skLineSegment(sketch, "E1564", {"start": v(41.14, 49.9) * mm, "end": v(41.14, 49.93) * mm});
            skLineSegment(sketch, "E1565", {"start": v(42.03, 49.95) * mm, "end": v(41.72, 49.8) * mm});
            skLineSegment(sketch, "E1566", {"start": v(41.33, 49.7) * mm, "end": v(41.2, 49.73) * mm});
            skLineSegment(sketch, "E1567", {"start": v(42.37, 50.08) * mm, "end": v(42.37, 50.1) * mm});
            skLineSegment(sketch, "E1568", {"start": v(41.72, 49.8) * mm, "end": v(41.7, 49.78) * mm});
            skLineSegment(sketch, "E1569", {"start": v(42.18, 49.78) * mm, "end": v(42.35, 49.95) * mm});
            skLineSegment(sketch, "E1570", {"start": v(42.37, 50.1) * mm, "end": v(42.35, 50.13) * mm});
            skLineSegment(sketch, "E1571", {"start": v(41.74, 49.52) * mm, "end": v(41.75, 49.53) * mm});
            skLineSegment(sketch, "E1572", {"start": v(42.35, 49.95) * mm, "end": v(42.36, 49.97) * mm});
            skLineSegment(sketch, "E1573", {"start": v(40.98, 49.33) * mm, "end": v(41.22, 49.37) * mm});
            skLineSegment(sketch, "E1574", {"start": v(41.75, 49.53) * mm, "end": v(41.97, 49.62) * mm});
            skLineSegment(sketch, "E1575", {"start": v(41.24, 45.17) * mm, "end": v(41.26, 45.16) * mm});
            skLineSegment(sketch, "E1576", {"start": v(41.22, 49.37) * mm, "end": v(41.23, 49.37) * mm});
            skLineSegment(sketch, "E1577", {"start": v(39.68, 45.48) * mm, "end": v(40.48, 45.77) * mm});
            skLineSegment(sketch, "E1578", {"start": v(40.47, 49.4) * mm, "end": v(40.48, 49.4) * mm});
            skLineSegment(sketch, "E1579", {"start": v(40.3, 44.99) * mm, "end": v(40.27, 45) * mm});
            skLineSegment(sketch, "E1580", {"start": v(40.48, 45.77) * mm, "end": v(40.52, 45.78) * mm});
            skLineSegment(sketch, "E1581", {"start": v(41.83, 44.6) * mm, "end": v(41.8, 44.6) * mm});
            skLineSegment(sketch, "E1582", {"start": v(40.27, 45) * mm, "end": v(40.25, 45.01) * mm});
            skLineSegment(sketch, "E1583", {"start": v(43.4, 44.92) * mm, "end": v(43.38, 44.9) * mm});
            skLineSegment(sketch, "E1584", {"start": v(41.8, 44.6) * mm, "end": v(41.45, 44.64) * mm});
            skLineSegment(sketch, "E1585", {"start": v(45.25, 46.26) * mm, "end": v(45.22, 46.23) * mm});
            skLineSegment(sketch, "E1586", {"start": v(43.38, 44.9) * mm, "end": v(43.33, 44.89) * mm});
            skLineSegment(sketch, "E1587", {"start": v(48.73, 50.37) * mm, "end": v(47.89, 49.46) * mm});
            skLineSegment(sketch, "E1588", {"start": v(45.22, 46.23) * mm, "end": v(44.7, 45.73) * mm});
            skLineSegment(sketch, "E1589", {"start": v(47.22, 49.76) * mm, "end": v(47.24, 49.78) * mm});
            skLineSegment(sketch, "E1590", {"start": v(47.89, 49.46) * mm, "end": v(47.88, 49.44) * mm});
            skLineSegment(sketch, "E1591", {"start": v(45.72, 48.54) * mm, "end": v(45.74, 48.55) * mm});
            skLineSegment(sketch, "E1592", {"start": v(47.24, 49.78) * mm, "end": v(47.85, 50.54) * mm});
            skLineSegment(sketch, "E1593", {"start": v(45.11, 48.24) * mm, "end": v(45.12, 48.25) * mm});
            skLineSegment(sketch, "E1594", {"start": v(45.74, 48.55) * mm, "end": v(45.8, 48.59) * mm});
            skLineSegment(sketch, "E1595", {"start": v(44.45, 48.22) * mm, "end": v(44.47, 48.21) * mm});
            skLineSegment(sketch, "E1596", {"start": v(45.12, 48.25) * mm, "end": v(45.13, 48.25) * mm});
            skLineSegment(sketch, "E1597", {"start": v(44.4, 48.73) * mm, "end": v(44.39, 48.67) * mm});
            skLineSegment(sketch, "E1598", {"start": v(44.47, 48.21) * mm, "end": v(44.79, 48.2) * mm});
            skLineSegment(sketch, "E1599", {"start": v(44.66, 49.29) * mm, "end": v(44.63, 49.22) * mm});
            skLineSegment(sketch, "E1600", {"start": v(44.39, 48.67) * mm, "end": v(44.38, 48.6) * mm});
            skLineSegment(sketch, "E1601", {"start": v(45.68, 51.76) * mm, "end": v(45.68, 51.72) * mm});
            skLineSegment(sketch, "E1602", {"start": v(44.63, 49.22) * mm, "end": v(44.62, 49.2) * mm});
            skLineSegment(sketch, "E1603", {"start": v(45.59, 52.07) * mm, "end": v(45.61, 52.04) * mm});
            skLineSegment(sketch, "E1604", {"start": v(45.68, 51.72) * mm, "end": v(45.56, 51.26) * mm});
            skLineSegment(sketch, "E1605", {"start": v(45.1, 52.27) * mm, "end": v(45.2, 52.25) * mm});
            skLineSegment(sketch, "E1606", {"start": v(45.61, 52.04) * mm, "end": v(45.63, 52.02) * mm});
            skLineSegment(sketch, "E1607", {"start": v(44.35, 52.14) * mm, "end": v(44.54, 52.19) * mm});
            skLineSegment(sketch, "E1608", {"start": v(45.2, 52.25) * mm, "end": v(45.22, 52.25) * mm});
            skLineSegment(sketch, "E1609", {"start": v(43.97, 51.95) * mm, "end": v(43.98, 51.96) * mm});
            skLineSegment(sketch, "E1610", {"start": v(44.54, 52.19) * mm, "end": v(44.55, 52.2) * mm});
            skLineSegment(sketch, "E1611", {"start": v(43.8, 51.7) * mm, "end": v(43.8, 51.7) * mm});
            skLineSegment(sketch, "E1612", {"start": v(43.98, 51.96) * mm, "end": v(44.06, 52.02) * mm});
            skLineSegment(sketch, "E1613", {"start": v(44.08, 51.75) * mm, "end": v(44.06, 51.74) * mm});
            skLineSegment(sketch, "E1614", {"start": v(43.8, 51.7) * mm, "end": v(43.8, 51.72) * mm});
            skLineSegment(sketch, "E1615", {"start": v(44.81, 51.87) * mm, "end": v(44.56, 51.9) * mm});
            skLineSegment(sketch, "E1616", {"start": v(44.06, 51.74) * mm, "end": v(43.85, 51.6) * mm});
            skLineSegment(sketch, "E1617", {"start": v(44.9, 51.5) * mm, "end": v(44.91, 51.55) * mm});
            skLineSegment(sketch, "E1618", {"start": v(44.56, 51.9) * mm, "end": v(44.44, 51.9) * mm});
            skLineSegment(sketch, "E1619", {"start": v(44.71, 51.03) * mm, "end": v(44.72, 51.04) * mm});
            skLineSegment(sketch, "E1620", {"start": v(44.91, 51.55) * mm, "end": v(44.91, 51.6) * mm});
            skLineSegment(sketch, "E1621", {"start": v(43.66, 48.8) * mm, "end": v(43.67, 48.82) * mm});
            skLineSegment(sketch, "E1622", {"start": v(44.72, 51.04) * mm, "end": v(44.73, 51.06) * mm});
            skLineSegment(sketch, "E1623", {"start": v(43.46, 48.3) * mm, "end": v(43.47, 48.38) * mm});
            skLineSegment(sketch, "E1624", {"start": v(43.67, 48.82) * mm, "end": v(43.94, 49.41) * mm});
            skLineSegment(sketch, "E1625", {"start": v(43.45, 48.17) * mm, "end": v(43.45, 48.24) * mm});
            skLineSegment(sketch, "E1626", {"start": v(43.47, 48.38) * mm, "end": v(43.52, 48.52) * mm});
            skLineSegment(sketch, "E1627", {"start": v(43.47, 48.03) * mm, "end": v(43.46, 48.1) * mm});
            skLineSegment(sketch, "E1628", {"start": v(43.45, 48.24) * mm, "end": v(43.46, 48.3) * mm});
            skLineSegment(sketch, "E1629", {"start": v(43.65, 47.72) * mm, "end": v(43.5, 47.96) * mm});
            skLineSegment(sketch, "E1630", {"start": v(43.46, 48.1) * mm, "end": v(43.45, 48.17) * mm});
            skLineSegment(sketch, "E1631", {"start": v(43.67, 47.7) * mm, "end": v(43.66, 47.7) * mm});
            skLineSegment(sketch, "E1632", {"start": v(43.5, 47.96) * mm, "end": v(43.47, 48.03) * mm});
            skLineSegment(sketch, "E1633", {"start": v(43.94, 47.66) * mm, "end": v(43.92, 47.66) * mm});
            skLineSegment(sketch, "E1634", {"start": v(43.66, 47.7) * mm, "end": v(43.65, 47.72) * mm});
            skLineSegment(sketch, "E1635", {"start": v(44.2, 47.66) * mm, "end": v(44.07, 47.65) * mm});
            skLineSegment(sketch, "E1636", {"start": v(43.92, 47.66) * mm, "end": v(43.67, 47.7) * mm});
            skLineSegment(sketch, "E1637", {"start": v(44.45, 47.72) * mm, "end": v(44.44, 47.72) * mm});
            skLineSegment(sketch, "E1638", {"start": v(44.07, 47.65) * mm, "end": v(43.94, 47.66) * mm});
            skLineSegment(sketch, "E1639", {"start": v(44.71, 47.81) * mm, "end": v(44.46, 47.72) * mm});
            skLineSegment(sketch, "E1640", {"start": v(44.44, 47.72) * mm, "end": v(44.2, 47.66) * mm});
            skLineSegment(sketch, "E1641", {"start": v(45.5, 48.16) * mm, "end": v(44.73, 47.82) * mm});
            skLineSegment(sketch, "E1642", {"start": v(44.46, 47.72) * mm, "end": v(44.45, 47.72) * mm});
            skLineSegment(sketch, "E1643", {"start": v(46.27, 48.6) * mm, "end": v(45.55, 48.18) * mm});
            skLineSegment(sketch, "E1644", {"start": v(44.73, 47.82) * mm, "end": v(44.71, 47.81) * mm});
            skLineSegment(sketch, "E1645", {"start": v(46.26, 48.56) * mm, "end": v(46.32, 48.64) * mm});
            skLineSegment(sketch, "E1646", {"start": v(45.55, 48.18) * mm, "end": v(45.5, 48.16) * mm});
            skLineSegment(sketch, "E1647", {"start": v(44.78, 46.73) * mm, "end": v(44.8, 46.76) * mm});
            skLineSegment(sketch, "E1648", {"start": v(46.32, 48.64) * mm, "end": v(46.27, 48.6) * mm});
            skLineSegment(sketch, "E1649", {"start": v(43.94, 45.78) * mm, "end": v(44, 45.83) * mm});
            skLineSegment(sketch, "E1650", {"start": v(44.8, 46.76) * mm, "end": v(46.26, 48.56) * mm});
            skLineSegment(sketch, "E1651", {"start": v(43.44, 45.37) * mm, "end": v(43.48, 45.4) * mm});
            skLineSegment(sketch, "E1652", {"start": v(44, 45.83) * mm, "end": v(44.78, 46.73) * mm});
            skLineSegment(sketch, "E1653", {"start": v(42.9, 45.01) * mm, "end": v(42.92, 45.02) * mm});
            skLineSegment(sketch, "E1654", {"start": v(43.48, 45.4) * mm, "end": v(43.94, 45.78) * mm});
            skLineSegment(sketch, "E1655", {"start": v(42.48, 44.9) * mm, "end": v(42.51, 44.91) * mm});
            skLineSegment(sketch, "E1656", {"start": v(42.92, 45.02) * mm, "end": v(43.44, 45.37) * mm});
            skLineSegment(sketch, "E1657", {"start": v(42.3, 44.88) * mm, "end": v(42.48, 44.9) * mm});
            skLineSegment(sketch, "E1658", {"start": v(42.51, 44.91) * mm, "end": v(42.9, 45.01) * mm});
            skLineSegment(sketch, "E1659", {"start": v(41.88, 44.92) * mm, "end": v(42.07, 44.89) * mm});
            skLineSegment(sketch, "E1660", {"start": v(42.28, 44.88) * mm, "end": v(42.3, 44.88) * mm});
            skLineSegment(sketch, "E1661", {"start": v(41.3, 45.14) * mm, "end": v(41.67, 44.98) * mm});
            skLineSegment(sketch, "E1662", {"start": v(42.07, 44.89) * mm, "end": v(42.08, 44.88) * mm});
            skLineSegment(sketch, "E1663", {"start": v(39.76, 50.93) * mm, "end": v(39.74, 50.93) * mm});
            skLineSegment(sketch, "E1664", {"start": v(41.67, 44.98) * mm, "end": v(41.68, 44.98) * mm});
            skLineSegment(sketch, "E1665", {"start": v(40.08, 51.19) * mm, "end": v(39.94, 51.05) * mm});
            skLineSegment(sketch, "E1666", {"start": v(39.74, 50.93) * mm, "end": v(39.4, 50.78) * mm});
            skLineSegment(sketch, "E1667", {"start": v(40.08, 51.3) * mm, "end": v(40.09, 51.29) * mm});
            skLineSegment(sketch, "E1668", {"start": v(39.94, 51.05) * mm, "end": v(39.92, 51.04) * mm});
            skLineSegment(sketch, "E1669", {"start": v(39.78, 51.18) * mm, "end": v(40.02, 51.37) * mm});
            skLineSegment(sketch, "E1670", {"start": v(40.09, 51.29) * mm, "end": v(40.09, 51.26) * mm});
            skLineSegment(sketch, "E1671", {"start": v(39.48, 51.02) * mm, "end": v(39.5, 51.02) * mm});
            skLineSegment(sketch, "E1672", {"start": v(40.02, 51.37) * mm, "end": v(40.04, 51.38) * mm});
            skLineSegment(sketch, "E1673", {"start": v(38.86, 50.97) * mm, "end": v(38.88, 50.96) * mm});
            skLineSegment(sketch, "E1674", {"start": v(39.5, 51.02) * mm, "end": v(39.63, 51.09) * mm});
            skLineSegment(sketch, "E1675", {"start": v(38.8, 51.07) * mm, "end": v(38.8, 51.05) * mm});
            skLineSegment(sketch, "E1676", {"start": v(38.88, 50.96) * mm, "end": v(39.18, 50.95) * mm});
            skLineSegment(sketch, "E1677", {"start": v(38.82, 51.14) * mm, "end": v(38.8, 51.11) * mm});
            skLineSegment(sketch, "E1678", {"start": v(38.8, 51.05) * mm, "end": v(38.81, 51.03) * mm});
            skLineSegment(sketch, "E1679", {"start": v(39.2, 51.73) * mm, "end": v(39.18, 51.69) * mm});
            skLineSegment(sketch, "E1680", {"start": v(38.8, 51.11) * mm, "end": v(38.8, 51.1) * mm});
            skLineSegment(sketch, "E1681", {"start": v(40.22, 53.12) * mm, "end": v(39.42, 52.02) * mm});
            skLineSegment(sketch, "E1682", {"start": v(39.18, 51.69) * mm, "end": v(38.86, 51.21) * mm});
            skLineSegment(sketch, "E1683", {"start": v(40.65, 53.72) * mm, "end": v(40.46, 53.45) * mm});
            skLineSegment(sketch, "E1684", {"start": v(39.42, 52.02) * mm, "end": v(39.39, 51.98) * mm});
            skLineSegment(sketch, "E1685", {"start": v(40.94, 54.22) * mm, "end": v(40.87, 54.06) * mm});
            skLineSegment(sketch, "E1686", {"start": v(40.46, 53.45) * mm, "end": v(40.45, 53.44) * mm});
            skLineSegment(sketch, "E1687", {"start": v(40.96, 54.43) * mm, "end": v(40.97, 54.39) * mm});
            skLineSegment(sketch, "E1688", {"start": v(40.87, 54.06) * mm, "end": v(40.87, 54.05) * mm});
            skLineSegment(sketch, "E1689", {"start": v(40.79, 54.66) * mm, "end": v(40.9, 54.53) * mm});
            skLineSegment(sketch, "E1690", {"start": v(40.97, 54.39) * mm, "end": v(40.97, 54.35) * mm});
            skLineSegment(sketch, "E1691", {"start": v(40.52, 54.72) * mm, "end": v(40.54, 54.72) * mm});
            skLineSegment(sketch, "E1692", {"start": v(40.9, 54.53) * mm, "end": v(40.93, 54.5) * mm});
            skLineSegment(sketch, "E1693", {"start": v(40.02, 54.7) * mm, "end": v(40.04, 54.7) * mm});
            skLineSegment(sketch, "E1694", {"start": v(40.54, 54.72) * mm, "end": v(40.77, 54.67) * mm});
            skLineSegment(sketch, "E1695", {"start": v(39.53, 54.57) * mm, "end": v(39.75, 54.63) * mm});
            skLineSegment(sketch, "E1696", {"start": v(40.04, 54.7) * mm, "end": v(40.27, 54.73) * mm});
            skLineSegment(sketch, "E1697", {"start": v(39.2, 54.43) * mm, "end": v(39.29, 54.48) * mm});
            skLineSegment(sketch, "E1698", {"start": v(39.75, 54.63) * mm, "end": v(39.77, 54.63) * mm});
            skLineSegment(sketch, "E1699", {"start": v(38.91, 54.18) * mm, "end": v(38.92, 54.2) * mm});
            skLineSegment(sketch, "E1700", {"start": v(39.29, 54.48) * mm, "end": v(39.3, 54.49) * mm});
            skLineSegment(sketch, "E1701", {"start": v(38.9, 54.06) * mm, "end": v(38.9, 54.09) * mm});
            skLineSegment(sketch, "E1702", {"start": v(38.92, 54.2) * mm, "end": v(39.09, 54.35) * mm});
            skLineSegment(sketch, "E1703", {"start": v(39.17, 54.17) * mm, "end": v(38.93, 54) * mm});
            skLineSegment(sketch, "E1704", {"start": v(38.9, 54.09) * mm, "end": v(38.9, 54.1) * mm});
            skLineSegment(sketch, "E1705", {"start": v(39.45, 54.31) * mm, "end": v(39.43, 54.3) * mm});
            skLineSegment(sketch, "E1706", {"start": v(38.93, 54) * mm, "end": v(38.92, 54) * mm});
            skLineSegment(sketch, "E1707", {"start": v(40.04, 54.35) * mm, "end": v(40.01, 54.35) * mm});
            skLineSegment(sketch, "E1708", {"start": v(39.43, 54.3) * mm, "end": v(39.3, 54.25) * mm});
            skLineSegment(sketch, "E1709", {"start": v(40.1, 54.25) * mm, "end": v(40.09, 54.27) * mm});
            skLineSegment(sketch, "E1710", {"start": v(40.01, 54.35) * mm, "end": v(39.73, 54.36) * mm});
            skLineSegment(sketch, "E1711", {"start": v(40.09, 54.27) * mm, "end": v(40.08, 54.28) * mm});
            skLineSegment(sketch, "E1712", {"start": v(40.08, 54.28) * mm, "end": v(40.04, 54.35) * mm});
            skLineSegment(sketch, "E1713", {"start": v(39.73, 54.36) * mm, "end": v(39.59, 54.35) * mm});
            skLineSegment(sketch, "E1714", {"start": v(39.59, 54.35) * mm, "end": v(39.45, 54.31) * mm});
            skLineSegment(sketch, "E1715", {"start": v(39.3, 54.25) * mm, "end": v(39.19, 54.18) * mm});
            skLineSegment(sketch, "E1716", {"start": v(39.19, 54.18) * mm, "end": v(39.17, 54.17) * mm});
            skLineSegment(sketch, "E1717", {"start": v(38.92, 54) * mm, "end": v(38.9, 54.04) * mm});
            skLineSegment(sketch, "E1718", {"start": v(38.9, 54.04) * mm, "end": v(38.9, 54.06) * mm});
            skLineSegment(sketch, "E1719", {"start": v(38.9, 54.1) * mm, "end": v(38.9, 54.14) * mm});
            skLineSegment(sketch, "E1720", {"start": v(38.9, 54.14) * mm, "end": v(38.91, 54.18) * mm});
            skLineSegment(sketch, "E1721", {"start": v(39.09, 54.35) * mm, "end": v(39.1, 54.36) * mm});
            skLineSegment(sketch, "E1722", {"start": v(39.1, 54.36) * mm, "end": v(39.2, 54.43) * mm});
            skLineSegment(sketch, "E1723", {"start": v(39.3, 54.49) * mm, "end": v(39.51, 54.57) * mm});
            skLineSegment(sketch, "E1724", {"start": v(39.51, 54.57) * mm, "end": v(39.53, 54.57) * mm});
            skLineSegment(sketch, "E1725", {"start": v(39.77, 54.63) * mm, "end": v(40.01, 54.7) * mm});
            skLineSegment(sketch, "E1726", {"start": v(40.01, 54.7) * mm, "end": v(40.02, 54.7) * mm});
            skLineSegment(sketch, "E1727", {"start": v(40.27, 54.73) * mm, "end": v(40.4, 54.73) * mm});
            skLineSegment(sketch, "E1728", {"start": v(40.4, 54.73) * mm, "end": v(40.52, 54.72) * mm});
            skLineSegment(sketch, "E1729", {"start": v(40.77, 54.67) * mm, "end": v(40.78, 54.67) * mm});
            skLineSegment(sketch, "E1730", {"start": v(40.78, 54.67) * mm, "end": v(40.79, 54.66) * mm});
            skLineSegment(sketch, "E1731", {"start": v(40.93, 54.5) * mm, "end": v(40.95, 54.47) * mm});
            skLineSegment(sketch, "E1732", {"start": v(40.95, 54.47) * mm, "end": v(40.96, 54.43) * mm});
            skLineSegment(sketch, "E1733", {"start": v(40.97, 54.35) * mm, "end": v(40.97, 54.3) * mm});
            skLineSegment(sketch, "E1734", {"start": v(40.97, 54.3) * mm, "end": v(40.94, 54.22) * mm});
            skLineSegment(sketch, "E1735", {"start": v(40.87, 54.05) * mm, "end": v(40.85, 54.03) * mm});
            skLineSegment(sketch, "E1736", {"start": v(40.85, 54.03) * mm, "end": v(40.65, 53.72) * mm});
            skLineSegment(sketch, "E1737", {"start": v(40.45, 53.44) * mm, "end": v(40.44, 53.42) * mm});
            skLineSegment(sketch, "E1738", {"start": v(40.44, 53.42) * mm, "end": v(40.22, 53.12) * mm});
            skLineSegment(sketch, "E1739", {"start": v(39.39, 51.98) * mm, "end": v(39.2, 51.74) * mm});
            skLineSegment(sketch, "E1740", {"start": v(39.2, 51.74) * mm, "end": v(39.2, 51.73) * mm});
            skLineSegment(sketch, "E1741", {"start": v(38.86, 51.21) * mm, "end": v(38.85, 51.2) * mm});
            skLineSegment(sketch, "E1742", {"start": v(38.85, 51.2) * mm, "end": v(38.82, 51.14) * mm});
            skLineSegment(sketch, "E1743", {"start": v(38.8, 51.1) * mm, "end": v(38.8, 51.08) * mm});
            skLineSegment(sketch, "E1744", {"start": v(38.8, 51.08) * mm, "end": v(38.8, 51.07) * mm});
            skLineSegment(sketch, "E1745", {"start": v(38.81, 51.03) * mm, "end": v(38.82, 51.02) * mm});
            skLineSegment(sketch, "E1746", {"start": v(38.82, 51.02) * mm, "end": v(38.86, 50.97) * mm});
            skLineSegment(sketch, "E1747", {"start": v(39.18, 50.95) * mm, "end": v(39.34, 50.97) * mm});
            skLineSegment(sketch, "E1748", {"start": v(39.34, 50.97) * mm, "end": v(39.48, 51.02) * mm});
            skLineSegment(sketch, "E1749", {"start": v(39.63, 51.09) * mm, "end": v(39.76, 51.17) * mm});
            skLineSegment(sketch, "E1750", {"start": v(39.76, 51.17) * mm, "end": v(39.78, 51.18) * mm});
            skLineSegment(sketch, "E1751", {"start": v(40.04, 51.38) * mm, "end": v(40.06, 51.34) * mm});
            skLineSegment(sketch, "E1752", {"start": v(40.06, 51.34) * mm, "end": v(40.08, 51.3) * mm});
            skLineSegment(sketch, "E1753", {"start": v(40.09, 51.26) * mm, "end": v(40.1, 51.23) * mm});
            skLineSegment(sketch, "E1754", {"start": v(40.1, 51.23) * mm, "end": v(40.08, 51.19) * mm});
            skLineSegment(sketch, "E1755", {"start": v(39.92, 51.04) * mm, "end": v(39.77, 50.94) * mm});
            skLineSegment(sketch, "E1756", {"start": v(39.77, 50.94) * mm, "end": v(39.76, 50.93) * mm});
            skLineSegment(sketch, "E1757", {"start": v(41.26, 45.16) * mm, "end": v(41.27, 45.15) * mm});
            skLineSegment(sketch, "E1758", {"start": v(41.27, 45.15) * mm, "end": v(41.3, 45.14) * mm});
            skLineSegment(sketch, "E1759", {"start": v(41.68, 44.98) * mm, "end": v(41.87, 44.92) * mm});
            skLineSegment(sketch, "E1760", {"start": v(41.87, 44.92) * mm, "end": v(41.88, 44.92) * mm});
            skLineSegment(sketch, "E1761", {"start": v(42.08, 44.88) * mm, "end": v(42.28, 44.88) * mm});
            skLineSegment(sketch, "E1762", {"start": v(42.89, 55.95) * mm, "end": v(42.89, 55.95) * mm});
            skSolve(sketch);
        }
        {
            var Q0;
            Q0=makeQuery(id+"F7.imprint","IMPRINT",FACE,{"disambiguationData":[TD([[makeQuery(id+"F7.imprint","IMPRINT",EDGE,{"derivedFrom":sQuery(id+"F7.wireOp",EDGE,"E804")}),-1.0]])]});
            var Q1;
            Q1=makeQuery(id+"F7.imprint","IMPRINT",FACE,{"disambiguationData":[TD([[makeQuery(id+"F7.imprint","IMPRINT",EDGE,{"derivedFrom":sQuery(id+"F7.wireOp",EDGE,"E1365")}),1.0]])]});
            var Q2;
            Q2=makeQuery(id+"F7.imprint","IMPRINT",FACE,{"disambiguationData":[TD([[makeQuery(id+"F7.imprint","IMPRINT",EDGE,{"derivedFrom":sQuery(id+"F7.wireOp",EDGE,"E1336")}),1.0]])]});
            var Q3;
            Q3=makeQuery(id+"F7.imprint","IMPRINT",FACE,{"disambiguationData":[TD([[makeQuery(id+"F7.imprint","IMPRINT",EDGE,{"derivedFrom":sQuery(id+"F7.wireOp",EDGE,"E1360")}),-1.0]])]});
            var Q4;
            Q4=makeQuery(id+"F7.imprint","IMPRINT",FACE,{"disambiguationData":[TD([[makeQuery(id+"F7.imprint","IMPRINT",EDGE,{"derivedFrom":sQuery(id+"F7.wireOp",EDGE,"E809")}),1.0]])]});
            var Q5;
            Q5=makeQuery(id+"F7.imprint","IMPRINT",FACE,{"disambiguationData":[TD([[makeQuery(id+"F7.imprint","IMPRINT",EDGE,{"derivedFrom":sQuery(id+"F7.wireOp",EDGE,"E796")}),-1.0]])]});
            extrude(context, id + "F8", {"entities" : qUnion([Q0, Q1, Q2, Q3, Q4, Q5]), "operationType" : NewBodyOperationType.REMOVE, "depth" : 25.4 * mm, "offsetDistance" : 25.4 * mm});
        }
        {
            var Q0;
            Q0=makeQuery(id+"F1.opExtrude","SWEPT_BODY",BODY,{"disambiguationData":[OSD([sQuery(id+"F0.wireOp",EDGE,"E0"),sQuery(id+"F0.wireOp",EDGE,"E1"),sQuery(id+"F0.wireOp",EDGE,"E2"),sQuery(id+"F0.wireOp",EDGE,"E3"),sQuery(id+"F0.wireOp",EDGE,"E4"),sQuery(id+"F0.wireOp",EDGE,"E5"),sQuery(id+"F0.wireOp",EDGE,"E6"),sQuery(id+"F0.wireOp",EDGE,"E7"),sQuery(id+"F0.wireOp",EDGE,"E8"),sQuery(id+"F0.wireOp",EDGE,"E9"),sQuery(id+"F0.wireOp",EDGE,"E10"),sQuery(id+"F0.wireOp",EDGE,"E11"),sQuery(id+"F0.wireOp",EDGE,"E12"),sQuery(id+"F0.wireOp",EDGE,"E13"),sQuery(id+"F0.wireOp",EDGE,"E14"),sQuery(id+"F0.wireOp",EDGE,"E15"),sQuery(id+"F0.wireOp",EDGE,"E16"),sQuery(id+"F0.wireOp",EDGE,"E17"),sQuery(id+"F0.wireOp",EDGE,"E18"),sQuery(id+"F0.wireOp",EDGE,"E19"),sQuery(id+"F0.wireOp",EDGE,"E20"),sQuery(id+"F0.wireOp",EDGE,"E21"),sQuery(id+"F0.wireOp",EDGE,"E22"),sQuery(id+"F0.wireOp",EDGE,"E23"),sQuery(id+"F0.wireOp",EDGE,"E24"),sQuery(id+"F0.wireOp",EDGE,"E25"),sQuery(id+"F0.wireOp",EDGE,"E26"),sQuery(id+"F0.wireOp",EDGE,"E27"),sQuery(id+"F0.wireOp",EDGE,"E28"),sQuery(id+"F0.wireOp",EDGE,"E29"),sQuery(id+"F0.wireOp",EDGE,"E30"),sQuery(id+"F0.wireOp",EDGE,"E31"),sQuery(id+"F0.wireOp",EDGE,"E32"),sQuery(id+"F0.wireOp",EDGE,"E33"),sQuery(id+"F0.wireOp",EDGE,"E34"),sQuery(id+"F0.wireOp",EDGE,"E35"),sQuery(id+"F0.wireOp",EDGE,"E36"),sQuery(id+"F0.wireOp",EDGE,"E37"),sQuery(id+"F0.wireOp",EDGE,"E38"),sQuery(id+"F0.wireOp",EDGE,"E39"),sQuery(id+"F0.wireOp",EDGE,"E40"),sQuery(id+"F0.wireOp",EDGE,"E41"),sQuery(id+"F0.wireOp",EDGE,"E42"),sQuery(id+"F0.wireOp",EDGE,"E43"),sQuery(id+"F0.wireOp",EDGE,"E44"),sQuery(id+"F0.wireOp",EDGE,"E45"),sQuery(id+"F0.wireOp",EDGE,"E46"),sQuery(id+"F0.wireOp",EDGE,"E47"),sQuery(id+"F0.wireOp",EDGE,"E48"),sQuery(id+"F0.wireOp",EDGE,"E49"),sQuery(id+"F0.wireOp",EDGE,"E50"),sQuery(id+"F0.wireOp",EDGE,"E51"),sQuery(id+"F0.wireOp",EDGE,"E52"),sQuery(id+"F0.wireOp",EDGE,"E53"),sQuery(id+"F0.wireOp",EDGE,"E54"),sQuery(id+"F0.wireOp",EDGE,"E55"),sQuery(id+"F0.wireOp",EDGE,"E56"),sQuery(id+"F0.wireOp",EDGE,"E57"),sQuery(id+"F0.wireOp",EDGE,"E58"),sQuery(id+"F0.wireOp",EDGE,"E59"),sQuery(id+"F0.wireOp",EDGE,"E60"),sQuery(id+"F0.wireOp",EDGE,"E61"),sQuery(id+"F0.wireOp",EDGE,"E62"),sQuery(id+"F0.wireOp",EDGE,"E63"),sQuery(id+"F0.wireOp",EDGE,"E64"),sQuery(id+"F0.wireOp",EDGE,"E65"),sQuery(id+"F0.wireOp",EDGE,"E66"),sQuery(id+"F0.wireOp",EDGE,"E67"),sQuery(id+"F0.wireOp",EDGE,"E68"),sQuery(id+"F0.wireOp",EDGE,"E69"),sQuery(id+"F0.wireOp",EDGE,"E70"),sQuery(id+"F0.wireOp",EDGE,"E71"),sQuery(id+"F0.wireOp",EDGE,"E72"),sQuery(id+"F0.wireOp",EDGE,"E73"),sQuery(id+"F0.wireOp",EDGE,"E74"),sQuery(id+"F0.wireOp",EDGE,"E75"),sQuery(id+"F0.wireOp",EDGE,"E76"),sQuery(id+"F0.wireOp",EDGE,"E77"),sQuery(id+"F0.wireOp",EDGE,"E78"),sQuery(id+"F0.wireOp",EDGE,"E79"),sQuery(id+"F0.wireOp",EDGE,"E80"),sQuery(id+"F0.wireOp",EDGE,"E81"),sQuery(id+"F0.wireOp",EDGE,"E82"),sQuery(id+"F0.wireOp",EDGE,"E83"),sQuery(id+"F0.wireOp",EDGE,"E84"),sQuery(id+"F0.wireOp",EDGE,"E85"),sQuery(id+"F0.wireOp",EDGE,"E86"),sQuery(id+"F0.wireOp",EDGE,"E87"),sQuery(id+"F0.wireOp",EDGE,"E88"),sQuery(id+"F0.wireOp",EDGE,"E89"),sQuery(id+"F0.wireOp",EDGE,"E90"),sQuery(id+"F0.wireOp",EDGE,"E91"),sQuery(id+"F0.wireOp",EDGE,"E92"),sQuery(id+"F0.wireOp",EDGE,"E93"),sQuery(id+"F0.wireOp",EDGE,"E94"),sQuery(id+"F0.wireOp",EDGE,"E95"),sQuery(id+"F0.wireOp",EDGE,"E96"),sQuery(id+"F0.wireOp",EDGE,"E97"),sQuery(id+"F0.wireOp",EDGE,"E98"),sQuery(id+"F0.wireOp",EDGE,"E100"),sQuery(id+"F0.wireOp",EDGE,"E101"),sQuery(id+"F0.wireOp",EDGE,"E102"),sQuery(id+"F0.wireOp",EDGE,"E103"),sQuery(id+"F0.wireOp",EDGE,"E104"),sQuery(id+"F0.wireOp",EDGE,"E105"),sQuery(id+"F0.wireOp",EDGE,"E106"),sQuery(id+"F0.wireOp",EDGE,"E107"),sQuery(id+"F0.wireOp",EDGE,"E108"),sQuery(id+"F0.wireOp",EDGE,"E109"),sQuery(id+"F0.wireOp",EDGE,"E110"),sQuery(id+"F0.wireOp",EDGE,"E111"),sQuery(id+"F0.wireOp",EDGE,"E112"),sQuery(id+"F0.wireOp",EDGE,"E113"),sQuery(id+"F0.wireOp",EDGE,"E114"),sQuery(id+"F0.wireOp",EDGE,"E115"),sQuery(id+"F0.wireOp",EDGE,"E116"),sQuery(id+"F0.wireOp",EDGE,"E117"),sQuery(id+"F0.wireOp",EDGE,"E118"),sQuery(id+"F0.wireOp",EDGE,"E119"),sQuery(id+"F0.wireOp",EDGE,"E120"),sQuery(id+"F0.wireOp",EDGE,"E121"),sQuery(id+"F0.wireOp",EDGE,"E122"),sQuery(id+"F0.wireOp",EDGE,"E123"),sQuery(id+"F0.wireOp",EDGE,"E124"),sQuery(id+"F0.wireOp",EDGE,"E125"),sQuery(id+"F0.wireOp",EDGE,"E126"),sQuery(id+"F0.wireOp",EDGE,"E127"),sQuery(id+"F0.wireOp",EDGE,"E128"),sQuery(id+"F0.wireOp",EDGE,"E129"),sQuery(id+"F0.wireOp",EDGE,"E130"),sQuery(id+"F0.wireOp",EDGE,"E131"),sQuery(id+"F0.wireOp",EDGE,"E132"),sQuery(id+"F0.wireOp",EDGE,"E133"),sQuery(id+"F0.wireOp",EDGE,"E134"),sQuery(id+"F0.wireOp",EDGE,"E135"),sQuery(id+"F0.wireOp",EDGE,"E136"),sQuery(id+"F0.wireOp",EDGE,"E137"),sQuery(id+"F0.wireOp",EDGE,"E138"),sQuery(id+"F0.wireOp",EDGE,"E139"),sQuery(id+"F0.wireOp",EDGE,"E140"),sQuery(id+"F0.wireOp",EDGE,"E141"),sQuery(id+"F0.wireOp",EDGE,"E142"),sQuery(id+"F0.wireOp",EDGE,"E143"),sQuery(id+"F0.wireOp",EDGE,"E144"),sQuery(id+"F0.wireOp",EDGE,"E145"),sQuery(id+"F0.wireOp",EDGE,"E146"),sQuery(id+"F0.wireOp",EDGE,"E147"),sQuery(id+"F0.wireOp",EDGE,"E148"),sQuery(id+"F0.wireOp",EDGE,"E149"),sQuery(id+"F0.wireOp",EDGE,"E150"),sQuery(id+"F0.wireOp",EDGE,"E151"),sQuery(id+"F0.wireOp",EDGE,"E152"),sQuery(id+"F0.wireOp",EDGE,"E153"),sQuery(id+"F0.wireOp",EDGE,"E154"),sQuery(id+"F0.wireOp",EDGE,"E155"),sQuery(id+"F0.wireOp",EDGE,"E156"),sQuery(id+"F0.wireOp",EDGE,"E157"),sQuery(id+"F0.wireOp",EDGE,"E158"),sQuery(id+"F0.wireOp",EDGE,"E159"),sQuery(id+"F0.wireOp",EDGE,"E160"),sQuery(id+"F0.wireOp",EDGE,"E161"),sQuery(id+"F0.wireOp",EDGE,"E162"),sQuery(id+"F0.wireOp",EDGE,"E163"),sQuery(id+"F0.wireOp",EDGE,"E164"),sQuery(id+"F0.wireOp",EDGE,"E165"),sQuery(id+"F0.wireOp",EDGE,"E166"),sQuery(id+"F0.wireOp",EDGE,"E167"),sQuery(id+"F0.wireOp",EDGE,"E168"),sQuery(id+"F0.wireOp",EDGE,"E169"),sQuery(id+"F0.wireOp",EDGE,"E170"),sQuery(id+"F0.wireOp",EDGE,"E171"),sQuery(id+"F0.wireOp",EDGE,"E172"),sQuery(id+"F0.wireOp",EDGE,"E173"),sQuery(id+"F0.wireOp",EDGE,"E174"),sQuery(id+"F0.wireOp",EDGE,"E175"),sQuery(id+"F0.wireOp",EDGE,"E176"),sQuery(id+"F0.wireOp",EDGE,"E177"),sQuery(id+"F0.wireOp",EDGE,"E178"),sQuery(id+"F0.wireOp",EDGE,"E179"),sQuery(id+"F0.wireOp",EDGE,"E180"),sQuery(id+"F0.wireOp",EDGE,"E181"),sQuery(id+"F0.wireOp",EDGE,"E182"),sQuery(id+"F0.wireOp",EDGE,"E183"),sQuery(id+"F0.wireOp",EDGE,"E184"),sQuery(id+"F0.wireOp",EDGE,"E185"),sQuery(id+"F0.wireOp",EDGE,"E186"),sQuery(id+"F0.wireOp",EDGE,"E187"),sQuery(id+"F0.wireOp",EDGE,"E188"),sQuery(id+"F0.wireOp",EDGE,"E189"),sQuery(id+"F0.wireOp",EDGE,"E190"),sQuery(id+"F0.wireOp",EDGE,"E191"),sQuery(id+"F0.wireOp",EDGE,"E192"),sQuery(id+"F0.wireOp",EDGE,"E193"),sQuery(id+"F0.wireOp",EDGE,"E194"),sQuery(id+"F0.wireOp",EDGE,"E195"),sQuery(id+"F0.wireOp",EDGE,"E196"),sQuery(id+"F0.wireOp",EDGE,"E197"),sQuery(id+"F0.wireOp",EDGE,"E198"),sQuery(id+"F0.wireOp",EDGE,"E199"),sQuery(id+"F0.wireOp",EDGE,"E200"),sQuery(id+"F0.wireOp",EDGE,"E201"),sQuery(id+"F0.wireOp",EDGE,"E202"),sQuery(id+"F0.wireOp",EDGE,"E203"),sQuery(id+"F0.wireOp",EDGE,"E204"),sQuery(id+"F0.wireOp",EDGE,"E205"),sQuery(id+"F0.wireOp",EDGE,"E206"),sQuery(id+"F0.wireOp",EDGE,"E207"),sQuery(id+"F0.wireOp",EDGE,"E208"),sQuery(id+"F0.wireOp",EDGE,"E209"),sQuery(id+"F0.wireOp",EDGE,"E210"),sQuery(id+"F0.wireOp",EDGE,"E211"),sQuery(id+"F0.wireOp",EDGE,"E212"),sQuery(id+"F0.wireOp",EDGE,"E213"),sQuery(id+"F0.wireOp",EDGE,"E214"),sQuery(id+"F0.wireOp",EDGE,"E215"),sQuery(id+"F0.wireOp",EDGE,"E216"),sQuery(id+"F0.wireOp",EDGE,"E217"),sQuery(id+"F0.wireOp",EDGE,"E218"),sQuery(id+"F0.wireOp",EDGE,"E219"),sQuery(id+"F0.wireOp",EDGE,"E220"),sQuery(id+"F0.wireOp",EDGE,"E221"),sQuery(id+"F0.wireOp",EDGE,"E222"),sQuery(id+"F0.wireOp",EDGE,"E223"),sQuery(id+"F0.wireOp",EDGE,"E224"),sQuery(id+"F0.wireOp",EDGE,"E225"),sQuery(id+"F0.wireOp",EDGE,"E226"),sQuery(id+"F0.wireOp",EDGE,"E227"),sQuery(id+"F0.wireOp",EDGE,"E228"),sQuery(id+"F0.wireOp",EDGE,"E229"),sQuery(id+"F0.wireOp",EDGE,"E230"),sQuery(id+"F0.wireOp",EDGE,"E231"),sQuery(id+"F0.wireOp",EDGE,"E232"),sQuery(id+"F0.wireOp",EDGE,"E233"),sQuery(id+"F0.wireOp",EDGE,"E234"),sQuery(id+"F0.wireOp",EDGE,"E235"),sQuery(id+"F0.wireOp",EDGE,"E236"),sQuery(id+"F0.wireOp",EDGE,"E237"),sQuery(id+"F0.wireOp",EDGE,"E238"),sQuery(id+"F0.wireOp",EDGE,"E239"),sQuery(id+"F0.wireOp",EDGE,"E240"),sQuery(id+"F0.wireOp",EDGE,"E241"),sQuery(id+"F0.wireOp",EDGE,"E242"),sQuery(id+"F0.wireOp",EDGE,"E243"),sQuery(id+"F0.wireOp",EDGE,"E244"),sQuery(id+"F0.wireOp",EDGE,"E245"),sQuery(id+"F0.wireOp",EDGE,"E246"),sQuery(id+"F0.wireOp",EDGE,"E247"),sQuery(id+"F0.wireOp",EDGE,"E248"),sQuery(id+"F0.wireOp",EDGE,"E249"),sQuery(id+"F0.wireOp",EDGE,"E250"),sQuery(id+"F0.wireOp",EDGE,"E251"),sQuery(id+"F0.wireOp",EDGE,"E252"),sQuery(id+"F0.wireOp",EDGE,"E253"),sQuery(id+"F0.wireOp",EDGE,"E254"),sQuery(id+"F0.wireOp",EDGE,"E255"),sQuery(id+"F0.wireOp",EDGE,"E256"),sQuery(id+"F0.wireOp",EDGE,"E257"),sQuery(id+"F0.wireOp",EDGE,"E258"),sQuery(id+"F0.wireOp",EDGE,"E259"),sQuery(id+"F0.wireOp",EDGE,"E260"),sQuery(id+"F0.wireOp",EDGE,"E261"),sQuery(id+"F0.wireOp",EDGE,"E262"),sQuery(id+"F0.wireOp",EDGE,"E263"),sQuery(id+"F0.wireOp",EDGE,"E264"),sQuery(id+"F0.wireOp",EDGE,"E265"),sQuery(id+"F0.wireOp",EDGE,"E266"),sQuery(id+"F0.wireOp",EDGE,"E267"),sQuery(id+"F0.wireOp",EDGE,"E268"),sQuery(id+"F0.wireOp",EDGE,"E269"),sQuery(id+"F0.wireOp",EDGE,"E270"),sQuery(id+"F0.wireOp",EDGE,"E271"),sQuery(id+"F0.wireOp",EDGE,"E272"),sQuery(id+"F0.wireOp",EDGE,"E273"),sQuery(id+"F0.wireOp",EDGE,"E274"),sQuery(id+"F0.wireOp",EDGE,"E275"),sQuery(id+"F0.wireOp",EDGE,"E276"),sQuery(id+"F0.wireOp",EDGE,"E277"),sQuery(id+"F0.wireOp",EDGE,"E278"),sQuery(id+"F0.wireOp",EDGE,"E279"),sQuery(id+"F0.wireOp",EDGE,"E280"),sQuery(id+"F0.wireOp",EDGE,"E281"),sQuery(id+"F0.wireOp",EDGE,"E282"),sQuery(id+"F0.wireOp",EDGE,"E283"),sQuery(id+"F0.wireOp",EDGE,"E284"),sQuery(id+"F0.wireOp",EDGE,"E285"),sQuery(id+"F0.wireOp",EDGE,"E286"),sQuery(id+"F0.wireOp",EDGE,"E287"),sQuery(id+"F0.wireOp",EDGE,"E288"),sQuery(id+"F0.wireOp",EDGE,"E289"),sQuery(id+"F0.wireOp",EDGE,"E290"),sQuery(id+"F0.wireOp",EDGE,"E291"),sQuery(id+"F0.wireOp",EDGE,"E292"),sQuery(id+"F0.wireOp",EDGE,"E293"),sQuery(id+"F0.wireOp",EDGE,"E294"),sQuery(id+"F0.wireOp",EDGE,"E295"),sQuery(id+"F0.wireOp",EDGE,"E296"),sQuery(id+"F0.wireOp",EDGE,"E297"),sQuery(id+"F0.wireOp",EDGE,"E298"),sQuery(id+"F0.wireOp",EDGE,"E299"),sQuery(id+"F0.wireOp",EDGE,"E300"),sQuery(id+"F0.wireOp",EDGE,"E301"),sQuery(id+"F0.wireOp",EDGE,"E302"),sQuery(id+"F0.wireOp",EDGE,"E303"),sQuery(id+"F0.wireOp",EDGE,"E304"),sQuery(id+"F0.wireOp",EDGE,"E305"),sQuery(id+"F0.wireOp",EDGE,"E306"),sQuery(id+"F0.wireOp",EDGE,"E307"),sQuery(id+"F0.wireOp",EDGE,"E308"),sQuery(id+"F0.wireOp",EDGE,"E309"),sQuery(id+"F0.wireOp",EDGE,"E310"),sQuery(id+"F0.wireOp",EDGE,"E311"),sQuery(id+"F0.wireOp",EDGE,"E312"),sQuery(id+"F0.wireOp",EDGE,"E313"),sQuery(id+"F0.wireOp",EDGE,"E314"),sQuery(id+"F0.wireOp",EDGE,"E315"),sQuery(id+"F0.wireOp",EDGE,"E316"),sQuery(id+"F0.wireOp",EDGE,"E317"),sQuery(id+"F0.wireOp",EDGE,"E318"),sQuery(id+"F0.wireOp",EDGE,"E319"),sQuery(id+"F0.wireOp",EDGE,"E320"),sQuery(id+"F0.wireOp",EDGE,"E321"),sQuery(id+"F0.wireOp",EDGE,"E322"),sQuery(id+"F0.wireOp",EDGE,"E323"),sQuery(id+"F0.wireOp",EDGE,"E324"),sQuery(id+"F0.wireOp",EDGE,"E325"),sQuery(id+"F0.wireOp",EDGE,"E326"),sQuery(id+"F0.wireOp",EDGE,"E327"),sQuery(id+"F0.wireOp",EDGE,"E328"),sQuery(id+"F0.wireOp",EDGE,"E329"),sQuery(id+"F0.wireOp",EDGE,"E330"),sQuery(id+"F0.wireOp",EDGE,"E331"),sQuery(id+"F0.wireOp",EDGE,"E332"),sQuery(id+"F0.wireOp",EDGE,"E333"),sQuery(id+"F0.wireOp",EDGE,"E334"),sQuery(id+"F0.wireOp",EDGE,"E335"),sQuery(id+"F0.wireOp",EDGE,"E336"),sQuery(id+"F0.wireOp",EDGE,"E337"),sQuery(id+"F0.wireOp",EDGE,"E338"),sQuery(id+"F0.wireOp",EDGE,"E339"),sQuery(id+"F0.wireOp",EDGE,"E340"),sQuery(id+"F0.wireOp",EDGE,"E341"),sQuery(id+"F0.wireOp",EDGE,"E342"),sQuery(id+"F0.wireOp",EDGE,"E343"),sQuery(id+"F0.wireOp",EDGE,"E344"),sQuery(id+"F0.wireOp",EDGE,"E345"),sQuery(id+"F0.wireOp",EDGE,"E346"),sQuery(id+"F0.wireOp",EDGE,"E347"),sQuery(id+"F0.wireOp",EDGE,"E348"),sQuery(id+"F0.wireOp",EDGE,"E349"),sQuery(id+"F0.wireOp",EDGE,"E350"),sQuery(id+"F0.wireOp",EDGE,"E351"),sQuery(id+"F0.wireOp",EDGE,"E352"),sQuery(id+"F0.wireOp",EDGE,"E353"),sQuery(id+"F0.wireOp",EDGE,"E354"),sQuery(id+"F0.wireOp",EDGE,"E355"),sQuery(id+"F0.wireOp",EDGE,"E356"),sQuery(id+"F0.wireOp",EDGE,"E357"),sQuery(id+"F0.wireOp",EDGE,"E358"),sQuery(id+"F0.wireOp",EDGE,"E359"),sQuery(id+"F0.wireOp",EDGE,"E360"),sQuery(id+"F0.wireOp",EDGE,"E361"),sQuery(id+"F0.wireOp",EDGE,"E362"),sQuery(id+"F0.wireOp",EDGE,"E363"),sQuery(id+"F0.wireOp",EDGE,"E364"),sQuery(id+"F0.wireOp",EDGE,"E365"),sQuery(id+"F0.wireOp",EDGE,"E366"),sQuery(id+"F0.wireOp",EDGE,"E367"),sQuery(id+"F0.wireOp",EDGE,"E368"),sQuery(id+"F0.wireOp",EDGE,"E369"),sQuery(id+"F0.wireOp",EDGE,"E370"),sQuery(id+"F0.wireOp",EDGE,"E371"),sQuery(id+"F0.wireOp",EDGE,"E372"),sQuery(id+"F0.wireOp",EDGE,"E373"),sQuery(id+"F0.wireOp",EDGE,"E374"),sQuery(id+"F0.wireOp",EDGE,"E375"),sQuery(id+"F0.wireOp",EDGE,"E376"),sQuery(id+"F0.wireOp",EDGE,"E377"),sQuery(id+"F0.wireOp",EDGE,"E378"),sQuery(id+"F0.wireOp",EDGE,"E379"),sQuery(id+"F0.wireOp",EDGE,"E380"),sQuery(id+"F0.wireOp",EDGE,"E381"),sQuery(id+"F0.wireOp",EDGE,"E382"),sQuery(id+"F0.wireOp",EDGE,"E383"),sQuery(id+"F0.wireOp",EDGE,"E384"),sQuery(id+"F0.wireOp",EDGE,"E385"),sQuery(id+"F0.wireOp",EDGE,"E386"),sQuery(id+"F0.wireOp",EDGE,"E387"),sQuery(id+"F0.wireOp",EDGE,"E388"),sQuery(id+"F0.wireOp",EDGE,"E389"),sQuery(id+"F0.wireOp",EDGE,"E390"),sQuery(id+"F0.wireOp",EDGE,"E391"),sQuery(id+"F0.wireOp",EDGE,"E392"),sQuery(id+"F0.wireOp",EDGE,"E393"),sQuery(id+"F0.wireOp",EDGE,"E394"),sQuery(id+"F0.wireOp",EDGE,"E395"),sQuery(id+"F0.wireOp",EDGE,"E396"),sQuery(id+"F0.wireOp",EDGE,"E397"),sQuery(id+"F0.wireOp",EDGE,"E398"),sQuery(id+"F0.wireOp",EDGE,"E399"),sQuery(id+"F0.wireOp",EDGE,"E400"),sQuery(id+"F0.wireOp",EDGE,"E401"),sQuery(id+"F0.wireOp",EDGE,"E402"),sQuery(id+"F0.wireOp",EDGE,"E403"),sQuery(id+"F0.wireOp",EDGE,"E404"),sQuery(id+"F0.wireOp",EDGE,"E405"),sQuery(id+"F0.wireOp",EDGE,"E406"),sQuery(id+"F0.wireOp",EDGE,"E407"),sQuery(id+"F0.wireOp",EDGE,"E408"),sQuery(id+"F0.wireOp",EDGE,"E409"),sQuery(id+"F0.wireOp",EDGE,"E410"),sQuery(id+"F0.wireOp",EDGE,"E411"),sQuery(id+"F0.wireOp",EDGE,"E412"),sQuery(id+"F0.wireOp",EDGE,"E413"),sQuery(id+"F0.wireOp",EDGE,"E414"),sQuery(id+"F0.wireOp",EDGE,"E415"),sQuery(id+"F0.wireOp",EDGE,"E416"),sQuery(id+"F0.wireOp",EDGE,"E417"),sQuery(id+"F0.wireOp",EDGE,"E418"),sQuery(id+"F0.wireOp",EDGE,"E419"),sQuery(id+"F0.wireOp",EDGE,"E420"),sQuery(id+"F0.wireOp",EDGE,"E421"),sQuery(id+"F0.wireOp",EDGE,"E422"),sQuery(id+"F0.wireOp",EDGE,"E423"),sQuery(id+"F0.wireOp",EDGE,"E424"),sQuery(id+"F0.wireOp",EDGE,"E425"),sQuery(id+"F0.wireOp",EDGE,"E426"),sQuery(id+"F0.wireOp",EDGE,"E427"),sQuery(id+"F0.wireOp",EDGE,"E428"),sQuery(id+"F0.wireOp",EDGE,"E429"),sQuery(id+"F0.wireOp",EDGE,"E430"),sQuery(id+"F0.wireOp",EDGE,"E431"),sQuery(id+"F0.wireOp",EDGE,"E432"),sQuery(id+"F0.wireOp",EDGE,"E433"),sQuery(id+"F0.wireOp",EDGE,"E434"),sQuery(id+"F0.wireOp",EDGE,"E435"),sQuery(id+"F0.wireOp",EDGE,"E436"),sQuery(id+"F0.wireOp",EDGE,"E437"),sQuery(id+"F0.wireOp",EDGE,"E438"),sQuery(id+"F0.wireOp",EDGE,"E439"),sQuery(id+"F0.wireOp",EDGE,"E440"),sQuery(id+"F0.wireOp",EDGE,"E441"),sQuery(id+"F0.wireOp",EDGE,"E442"),sQuery(id+"F0.wireOp",EDGE,"E443"),sQuery(id+"F0.wireOp",EDGE,"E444"),sQuery(id+"F0.wireOp",EDGE,"E445"),sQuery(id+"F0.wireOp",EDGE,"E446"),sQuery(id+"F0.wireOp",EDGE,"E447"),sQuery(id+"F0.wireOp",EDGE,"E448"),sQuery(id+"F0.wireOp",EDGE,"E449"),sQuery(id+"F0.wireOp",EDGE,"E450"),sQuery(id+"F0.wireOp",EDGE,"E451"),sQuery(id+"F0.wireOp",EDGE,"E452"),sQuery(id+"F0.wireOp",EDGE,"E453"),sQuery(id+"F0.wireOp",EDGE,"E454"),sQuery(id+"F0.wireOp",EDGE,"E455"),sQuery(id+"F0.wireOp",EDGE,"E456"),sQuery(id+"F0.wireOp",EDGE,"E457"),sQuery(id+"F0.wireOp",EDGE,"E458"),sQuery(id+"F0.wireOp",EDGE,"E459"),sQuery(id+"F0.wireOp",EDGE,"E460"),sQuery(id+"F0.wireOp",EDGE,"E461"),sQuery(id+"F0.wireOp",EDGE,"E462"),sQuery(id+"F0.wireOp",EDGE,"E463"),sQuery(id+"F0.wireOp",EDGE,"E464"),sQuery(id+"F0.wireOp",EDGE,"E465"),sQuery(id+"F0.wireOp",EDGE,"E466"),sQuery(id+"F0.wireOp",EDGE,"E467"),sQuery(id+"F0.wireOp",EDGE,"E468"),sQuery(id+"F0.wireOp",EDGE,"E469"),sQuery(id+"F0.wireOp",EDGE,"E470"),sQuery(id+"F0.wireOp",EDGE,"E471"),sQuery(id+"F0.wireOp",EDGE,"E472"),sQuery(id+"F0.wireOp",EDGE,"E473"),sQuery(id+"F0.wireOp",EDGE,"E474"),sQuery(id+"F0.wireOp",EDGE,"E475"),sQuery(id+"F0.wireOp",EDGE,"E476"),sQuery(id+"F0.wireOp",EDGE,"E477"),sQuery(id+"F0.wireOp",EDGE,"E478"),sQuery(id+"F0.wireOp",EDGE,"E479"),sQuery(id+"F0.wireOp",EDGE,"E480"),sQuery(id+"F0.wireOp",EDGE,"E481"),sQuery(id+"F0.wireOp",EDGE,"E482"),sQuery(id+"F0.wireOp",EDGE,"E483"),sQuery(id+"F0.wireOp",EDGE,"E484"),sQuery(id+"F0.wireOp",EDGE,"E485"),sQuery(id+"F0.wireOp",EDGE,"E486"),sQuery(id+"F0.wireOp",EDGE,"E487"),sQuery(id+"F0.wireOp",EDGE,"E488"),sQuery(id+"F0.wireOp",EDGE,"E489"),sQuery(id+"F0.wireOp",EDGE,"E490"),sQuery(id+"F0.wireOp",EDGE,"E491"),sQuery(id+"F0.wireOp",EDGE,"E492"),sQuery(id+"F0.wireOp",EDGE,"E493"),sQuery(id+"F0.wireOp",EDGE,"E494"),sQuery(id+"F0.wireOp",EDGE,"E495"),sQuery(id+"F0.wireOp",EDGE,"E496"),sQuery(id+"F0.wireOp",EDGE,"E497"),sQuery(id+"F0.wireOp",EDGE,"E498"),sQuery(id+"F0.wireOp",EDGE,"E499"),sQuery(id+"F0.wireOp",EDGE,"E500"),sQuery(id+"F0.wireOp",EDGE,"E501"),sQuery(id+"F0.wireOp",EDGE,"E502"),sQuery(id+"F0.wireOp",EDGE,"E503"),sQuery(id+"F0.wireOp",EDGE,"E504"),sQuery(id+"F0.wireOp",EDGE,"E505"),sQuery(id+"F0.wireOp",EDGE,"E506"),sQuery(id+"F0.wireOp",EDGE,"E507"),sQuery(id+"F0.wireOp",EDGE,"E508"),sQuery(id+"F0.wireOp",EDGE,"E509"),sQuery(id+"F0.wireOp",EDGE,"E510"),sQuery(id+"F0.wireOp",EDGE,"E511"),sQuery(id+"F0.wireOp",EDGE,"E512"),sQuery(id+"F0.wireOp",EDGE,"E513"),sQuery(id+"F0.wireOp",EDGE,"E514"),sQuery(id+"F0.wireOp",EDGE,"E515"),sQuery(id+"F0.wireOp",EDGE,"E516"),sQuery(id+"F0.wireOp",EDGE,"E517"),sQuery(id+"F0.wireOp",EDGE,"E518"),sQuery(id+"F0.wireOp",EDGE,"E519"),sQuery(id+"F0.wireOp",EDGE,"E520"),sQuery(id+"F0.wireOp",EDGE,"E521"),sQuery(id+"F0.wireOp",EDGE,"E522"),sQuery(id+"F0.wireOp",EDGE,"E523"),sQuery(id+"F0.wireOp",EDGE,"E524"),sQuery(id+"F0.wireOp",EDGE,"E525"),sQuery(id+"F0.wireOp",EDGE,"E526"),sQuery(id+"F0.wireOp",EDGE,"E527"),sQuery(id+"F0.wireOp",EDGE,"E528"),sQuery(id+"F0.wireOp",EDGE,"E529"),sQuery(id+"F0.wireOp",EDGE,"E530"),sQuery(id+"F0.wireOp",EDGE,"E531"),sQuery(id+"F0.wireOp",EDGE,"E532"),sQuery(id+"F0.wireOp",EDGE,"E533"),sQuery(id+"F0.wireOp",EDGE,"E534"),sQuery(id+"F0.wireOp",EDGE,"E535"),sQuery(id+"F0.wireOp",EDGE,"E536"),sQuery(id+"F0.wireOp",EDGE,"E537"),sQuery(id+"F0.wireOp",EDGE,"E538"),sQuery(id+"F0.wireOp",EDGE,"E539"),sQuery(id+"F0.wireOp",EDGE,"E540"),sQuery(id+"F0.wireOp",EDGE,"E541"),sQuery(id+"F0.wireOp",EDGE,"E542"),sQuery(id+"F0.wireOp",EDGE,"E543"),sQuery(id+"F0.wireOp",EDGE,"E544"),sQuery(id+"F0.wireOp",EDGE,"E545"),sQuery(id+"F0.wireOp",EDGE,"E546"),sQuery(id+"F0.wireOp",EDGE,"E547"),sQuery(id+"F0.wireOp",EDGE,"E548"),sQuery(id+"F0.wireOp",EDGE,"E549"),sQuery(id+"F0.wireOp",EDGE,"E550"),sQuery(id+"F0.wireOp",EDGE,"E551"),sQuery(id+"F0.wireOp",EDGE,"E552"),sQuery(id+"F0.wireOp",EDGE,"E553"),sQuery(id+"F0.wireOp",EDGE,"E554"),sQuery(id+"F0.wireOp",EDGE,"E555"),sQuery(id+"F0.wireOp",EDGE,"E556"),sQuery(id+"F0.wireOp",EDGE,"E557"),sQuery(id+"F0.wireOp",EDGE,"E558"),sQuery(id+"F0.wireOp",EDGE,"E559"),sQuery(id+"F0.wireOp",EDGE,"E560"),sQuery(id+"F0.wireOp",EDGE,"E561"),sQuery(id+"F0.wireOp",EDGE,"E562"),sQuery(id+"F0.wireOp",EDGE,"E563"),sQuery(id+"F0.wireOp",EDGE,"E564"),sQuery(id+"F0.wireOp",EDGE,"E565"),sQuery(id+"F0.wireOp",EDGE,"E566"),sQuery(id+"F0.wireOp",EDGE,"E567"),sQuery(id+"F0.wireOp",EDGE,"E568"),sQuery(id+"F0.wireOp",EDGE,"E569"),sQuery(id+"F0.wireOp",EDGE,"E570"),sQuery(id+"F0.wireOp",EDGE,"E571"),sQuery(id+"F0.wireOp",EDGE,"E572"),sQuery(id+"F0.wireOp",EDGE,"E573"),sQuery(id+"F0.wireOp",EDGE,"E574"),sQuery(id+"F0.wireOp",EDGE,"E575"),sQuery(id+"F0.wireOp",EDGE,"E576"),sQuery(id+"F0.wireOp",EDGE,"E577"),sQuery(id+"F0.wireOp",EDGE,"E578"),sQuery(id+"F0.wireOp",EDGE,"E579"),sQuery(id+"F0.wireOp",EDGE,"E580"),sQuery(id+"F0.wireOp",EDGE,"E581"),sQuery(id+"F0.wireOp",EDGE,"E582"),sQuery(id+"F0.wireOp",EDGE,"E583"),sQuery(id+"F0.wireOp",EDGE,"E584"),sQuery(id+"F0.wireOp",EDGE,"E585"),sQuery(id+"F0.wireOp",EDGE,"E586"),sQuery(id+"F0.wireOp",EDGE,"E587"),sQuery(id+"F0.wireOp",EDGE,"E588"),sQuery(id+"F0.wireOp",EDGE,"E589"),sQuery(id+"F0.wireOp",EDGE,"E590"),sQuery(id+"F0.wireOp",EDGE,"E591"),sQuery(id+"F0.wireOp",EDGE,"E592"),sQuery(id+"F0.wireOp",EDGE,"E593"),sQuery(id+"F0.wireOp",EDGE,"E594"),sQuery(id+"F0.wireOp",EDGE,"E595"),sQuery(id+"F0.wireOp",EDGE,"E597"),sQuery(id+"F0.wireOp",EDGE,"E598"),sQuery(id+"F0.wireOp",EDGE,"E599"),sQuery(id+"F0.wireOp",EDGE,"E600"),sQuery(id+"F0.wireOp",EDGE,"E601"),sQuery(id+"F0.wireOp",EDGE,"E602"),sQuery(id+"F0.wireOp",EDGE,"E603"),sQuery(id+"F0.wireOp",EDGE,"E604"),sQuery(id+"F0.wireOp",EDGE,"E605"),sQuery(id+"F0.wireOp",EDGE,"E606"),sQuery(id+"F0.wireOp",EDGE,"E607"),sQuery(id+"F0.wireOp",EDGE,"E608"),sQuery(id+"F0.wireOp",EDGE,"E609"),sQuery(id+"F0.wireOp",EDGE,"E610"),sQuery(id+"F0.wireOp",EDGE,"E611"),sQuery(id+"F0.wireOp",EDGE,"E612"),sQuery(id+"F0.wireOp",EDGE,"E613"),sQuery(id+"F0.wireOp",EDGE,"E614"),sQuery(id+"F0.wireOp",EDGE,"E615"),sQuery(id+"F0.wireOp",EDGE,"E616"),sQuery(id+"F0.wireOp",EDGE,"E617"),sQuery(id+"F0.wireOp",EDGE,"E618"),sQuery(id+"F0.wireOp",EDGE,"E619"),sQuery(id+"F0.wireOp",EDGE,"E620"),sQuery(id+"F0.wireOp",EDGE,"E621"),sQuery(id+"F0.wireOp",EDGE,"E622"),sQuery(id+"F0.wireOp",EDGE,"E623"),sQuery(id+"F0.wireOp",EDGE,"E624"),sQuery(id+"F0.wireOp",EDGE,"E625"),sQuery(id+"F0.wireOp",EDGE,"E626"),sQuery(id+"F0.wireOp",EDGE,"E627"),sQuery(id+"F0.wireOp",EDGE,"E628"),sQuery(id+"F0.wireOp",EDGE,"E629"),sQuery(id+"F0.wireOp",EDGE,"E630"),sQuery(id+"F0.wireOp",EDGE,"E631"),sQuery(id+"F0.wireOp",EDGE,"E632"),sQuery(id+"F0.wireOp",EDGE,"E633"),sQuery(id+"F0.wireOp",EDGE,"E634"),sQuery(id+"F0.wireOp",EDGE,"E635"),sQuery(id+"F0.wireOp",EDGE,"E636"),sQuery(id+"F0.wireOp",EDGE,"E637"),sQuery(id+"F0.wireOp",EDGE,"E638"),sQuery(id+"F0.wireOp",EDGE,"E639"),sQuery(id+"F0.wireOp",EDGE,"E640"),sQuery(id+"F0.wireOp",EDGE,"E641"),sQuery(id+"F0.wireOp",EDGE,"E642"),sQuery(id+"F0.wireOp",EDGE,"E643"),sQuery(id+"F0.wireOp",EDGE,"E644"),sQuery(id+"F0.wireOp",EDGE,"E645"),sQuery(id+"F0.wireOp",EDGE,"E646"),sQuery(id+"F0.wireOp",EDGE,"E647"),sQuery(id+"F0.wireOp",EDGE,"E648"),sQuery(id+"F0.wireOp",EDGE,"E649"),sQuery(id+"F0.wireOp",EDGE,"E650"),sQuery(id+"F0.wireOp",EDGE,"E651"),sQuery(id+"F0.wireOp",EDGE,"E652"),sQuery(id+"F0.wireOp",EDGE,"E653"),sQuery(id+"F0.wireOp",EDGE,"E654"),sQuery(id+"F0.wireOp",EDGE,"E655"),sQuery(id+"F0.wireOp",EDGE,"E656"),sQuery(id+"F0.wireOp",EDGE,"E657"),sQuery(id+"F0.wireOp",EDGE,"E658"),sQuery(id+"F0.wireOp",EDGE,"E659"),sQuery(id+"F0.wireOp",EDGE,"E660"),sQuery(id+"F0.wireOp",EDGE,"E661"),sQuery(id+"F0.wireOp",EDGE,"E662"),sQuery(id+"F0.wireOp",EDGE,"E663"),sQuery(id+"F0.wireOp",EDGE,"E664"),sQuery(id+"F0.wireOp",EDGE,"E665"),sQuery(id+"F0.wireOp",EDGE,"E666"),sQuery(id+"F0.wireOp",EDGE,"E667"),sQuery(id+"F0.wireOp",EDGE,"E668"),sQuery(id+"F0.wireOp",EDGE,"E669"),sQuery(id+"F0.wireOp",EDGE,"E670"),sQuery(id+"F0.wireOp",EDGE,"E671"),sQuery(id+"F0.wireOp",EDGE,"E672"),sQuery(id+"F0.wireOp",EDGE,"E673"),sQuery(id+"F0.wireOp",EDGE,"E674"),sQuery(id+"F0.wireOp",EDGE,"E675"),sQuery(id+"F0.wireOp",EDGE,"E676"),sQuery(id+"F0.wireOp",EDGE,"E677"),sQuery(id+"F0.wireOp",EDGE,"E678"),sQuery(id+"F0.wireOp",EDGE,"E679"),sQuery(id+"F0.wireOp",EDGE,"E680"),sQuery(id+"F0.wireOp",EDGE,"E681"),sQuery(id+"F0.wireOp",EDGE,"E682"),sQuery(id+"F0.wireOp",EDGE,"E683"),sQuery(id+"F0.wireOp",EDGE,"E684"),sQuery(id+"F0.wireOp",EDGE,"E685"),sQuery(id+"F0.wireOp",EDGE,"E686"),sQuery(id+"F0.wireOp",EDGE,"E687"),sQuery(id+"F0.wireOp",EDGE,"E688"),sQuery(id+"F0.wireOp",EDGE,"E689"),sQuery(id+"F0.wireOp",EDGE,"E690"),sQuery(id+"F0.wireOp",EDGE,"E691"),sQuery(id+"F0.wireOp",EDGE,"E692"),sQuery(id+"F0.wireOp",EDGE,"E693"),sQuery(id+"F0.wireOp",EDGE,"E694"),sQuery(id+"F0.wireOp",EDGE,"E695"),sQuery(id+"F0.wireOp",EDGE,"E696"),sQuery(id+"F0.wireOp",EDGE,"E697"),sQuery(id+"F0.wireOp",EDGE,"E698"),sQuery(id+"F0.wireOp",EDGE,"E699"),sQuery(id+"F0.wireOp",EDGE,"E700"),sQuery(id+"F0.wireOp",EDGE,"E701"),sQuery(id+"F0.wireOp",EDGE,"E702"),sQuery(id+"F0.wireOp",EDGE,"E703"),sQuery(id+"F0.wireOp",EDGE,"E704"),sQuery(id+"F0.wireOp",EDGE,"E705"),sQuery(id+"F0.wireOp",EDGE,"E706"),sQuery(id+"F0.wireOp",EDGE,"E707"),sQuery(id+"F0.wireOp",EDGE,"E708"),sQuery(id+"F0.wireOp",EDGE,"E709"),sQuery(id+"F0.wireOp",EDGE,"E710"),sQuery(id+"F0.wireOp",EDGE,"E711"),sQuery(id+"F0.wireOp",EDGE,"E712"),sQuery(id+"F0.wireOp",EDGE,"E713"),sQuery(id+"F0.wireOp",EDGE,"E714"),sQuery(id+"F0.wireOp",EDGE,"E715"),sQuery(id+"F0.wireOp",EDGE,"E716"),sQuery(id+"F0.wireOp",EDGE,"E717"),sQuery(id+"F0.wireOp",EDGE,"E718"),sQuery(id+"F0.wireOp",EDGE,"E719"),sQuery(id+"F0.wireOp",EDGE,"E720"),sQuery(id+"F0.wireOp",EDGE,"E721"),sQuery(id+"F0.wireOp",EDGE,"E722"),sQuery(id+"F0.wireOp",EDGE,"E723"),sQuery(id+"F0.wireOp",EDGE,"E724"),sQuery(id+"F0.wireOp",EDGE,"E725"),sQuery(id+"F0.wireOp",EDGE,"E726"),sQuery(id+"F0.wireOp",EDGE,"E727"),sQuery(id+"F0.wireOp",EDGE,"E728"),sQuery(id+"F0.wireOp",EDGE,"E729"),sQuery(id+"F0.wireOp",EDGE,"E730"),sQuery(id+"F0.wireOp",EDGE,"E731"),sQuery(id+"F0.wireOp",EDGE,"E732"),sQuery(id+"F0.wireOp",EDGE,"E733"),sQuery(id+"F0.wireOp",EDGE,"E734"),sQuery(id+"F0.wireOp",EDGE,"E735"),sQuery(id+"F0.wireOp",EDGE,"E736"),sQuery(id+"F0.wireOp",EDGE,"E737"),sQuery(id+"F0.wireOp",EDGE,"E738"),sQuery(id+"F0.wireOp",EDGE,"E739"),sQuery(id+"F0.wireOp",EDGE,"E740"),sQuery(id+"F0.wireOp",EDGE,"E741"),sQuery(id+"F0.wireOp",EDGE,"E742"),sQuery(id+"F0.wireOp",EDGE,"E743"),sQuery(id+"F0.wireOp",EDGE,"E744"),sQuery(id+"F0.wireOp",EDGE,"E745"),sQuery(id+"F0.wireOp",EDGE,"E746"),sQuery(id+"F0.wireOp",EDGE,"E747"),sQuery(id+"F0.wireOp",EDGE,"E748"),sQuery(id+"F0.wireOp",EDGE,"E749"),sQuery(id+"F0.wireOp",EDGE,"E750"),sQuery(id+"F0.wireOp",EDGE,"E751"),sQuery(id+"F0.wireOp",EDGE,"E752"),sQuery(id+"F0.wireOp",EDGE,"E753"),sQuery(id+"F0.wireOp",EDGE,"E754"),sQuery(id+"F0.wireOp",EDGE,"E755"),sQuery(id+"F0.wireOp",EDGE,"E756"),sQuery(id+"F0.wireOp",EDGE,"E757"),sQuery(id+"F0.wireOp",EDGE,"E758"),sQuery(id+"F0.wireOp",EDGE,"E759"),sQuery(id+"F0.wireOp",EDGE,"E760"),sQuery(id+"F0.wireOp",EDGE,"E761"),sQuery(id+"F0.wireOp",EDGE,"E762"),sQuery(id+"F0.wireOp",EDGE,"E763"),sQuery(id+"F0.wireOp",EDGE,"E764"),sQuery(id+"F0.wireOp",EDGE,"E765"),sQuery(id+"F0.wireOp",EDGE,"E766"),sQuery(id+"F0.wireOp",EDGE,"E767"),sQuery(id+"F0.wireOp",EDGE,"E768"),sQuery(id+"F0.wireOp",EDGE,"E769"),sQuery(id+"F0.wireOp",EDGE,"E770"),sQuery(id+"F0.wireOp",EDGE,"E771"),sQuery(id+"F0.wireOp",EDGE,"E772"),sQuery(id+"F0.wireOp",EDGE,"E773"),sQuery(id+"F0.wireOp",EDGE,"E774"),sQuery(id+"F0.wireOp",EDGE,"E775"),sQuery(id+"F0.wireOp",EDGE,"E776"),sQuery(id+"F0.wireOp",EDGE,"E777"),sQuery(id+"F0.wireOp",EDGE,"E778"),sQuery(id+"F0.wireOp",EDGE,"E779"),sQuery(id+"F0.wireOp",EDGE,"E780"),sQuery(id+"F0.wireOp",EDGE,"E781"),sQuery(id+"F0.wireOp",EDGE,"E782"),sQuery(id+"F0.wireOp",EDGE,"E783"),sQuery(id+"F0.wireOp",EDGE,"E784"),sQuery(id+"F0.wireOp",EDGE,"E785"),sQuery(id+"F0.wireOp",EDGE,"E786"),sQuery(id+"F0.wireOp",EDGE,"E787"),sQuery(id+"F0.wireOp",EDGE,"E788"),sQuery(id+"F0.wireOp",EDGE,"E789"),sQuery(id+"F0.wireOp",EDGE,"E790.filletArc"),sQuery(id+"F0.wireOp",EDGE,"E791"),sQuery(id+"F0.wireOp",EDGE,"E792"),sQuery(id+"F0.wireOp",EDGE,"E793"),sQuery(id+"F0.wireOp",EDGE,"E794"),sQuery(id+"F0.wireOp",EDGE,"E795")])]});
            var Q1;
            Q1=qCreatedBy(makeId("Origin.pointOp"),VERTEX);
            transform(context, id + "F9", {"entities" : qUnion([Q0]), "transformType" : TransformType.SCALE_UNIFORMLY, "scale" : 1.5, "scalePoint" : qUnion([Q1]), "makeCopy" : false});
        }
        {
            var Q0;
            Q0=makeQuery(id+"F1.opExtrude","CAP_FACE",FACE,{"disambiguationData":[OSD([sQuery(id+"F0.wireOp",EDGE,"E0"),sQuery(id+"F0.wireOp",EDGE,"E1"),sQuery(id+"F0.wireOp",EDGE,"E2"),sQuery(id+"F0.wireOp",EDGE,"E3"),sQuery(id+"F0.wireOp",EDGE,"E4"),sQuery(id+"F0.wireOp",EDGE,"E5"),sQuery(id+"F0.wireOp",EDGE,"E6"),sQuery(id+"F0.wireOp",EDGE,"E7"),sQuery(id+"F0.wireOp",EDGE,"E8"),sQuery(id+"F0.wireOp",EDGE,"E9"),sQuery(id+"F0.wireOp",EDGE,"E10"),sQuery(id+"F0.wireOp",EDGE,"E11"),sQuery(id+"F0.wireOp",EDGE,"E12"),sQuery(id+"F0.wireOp",EDGE,"E13"),sQuery(id+"F0.wireOp",EDGE,"E14"),sQuery(id+"F0.wireOp",EDGE,"E15"),sQuery(id+"F0.wireOp",EDGE,"E16"),sQuery(id+"F0.wireOp",EDGE,"E17"),sQuery(id+"F0.wireOp",EDGE,"E18"),sQuery(id+"F0.wireOp",EDGE,"E19"),sQuery(id+"F0.wireOp",EDGE,"E20"),sQuery(id+"F0.wireOp",EDGE,"E21"),sQuery(id+"F0.wireOp",EDGE,"E22"),sQuery(id+"F0.wireOp",EDGE,"E23"),sQuery(id+"F0.wireOp",EDGE,"E24"),sQuery(id+"F0.wireOp",EDGE,"E25"),sQuery(id+"F0.wireOp",EDGE,"E26"),sQuery(id+"F0.wireOp",EDGE,"E27"),sQuery(id+"F0.wireOp",EDGE,"E28"),sQuery(id+"F0.wireOp",EDGE,"E29"),sQuery(id+"F0.wireOp",EDGE,"E30"),sQuery(id+"F0.wireOp",EDGE,"E31"),sQuery(id+"F0.wireOp",EDGE,"E32"),sQuery(id+"F0.wireOp",EDGE,"E33"),sQuery(id+"F0.wireOp",EDGE,"E34"),sQuery(id+"F0.wireOp",EDGE,"E35"),sQuery(id+"F0.wireOp",EDGE,"E36"),sQuery(id+"F0.wireOp",EDGE,"E37"),sQuery(id+"F0.wireOp",EDGE,"E38"),sQuery(id+"F0.wireOp",EDGE,"E39"),sQuery(id+"F0.wireOp",EDGE,"E40"),sQuery(id+"F0.wireOp",EDGE,"E41"),sQuery(id+"F0.wireOp",EDGE,"E42"),sQuery(id+"F0.wireOp",EDGE,"E43"),sQuery(id+"F0.wireOp",EDGE,"E44"),sQuery(id+"F0.wireOp",EDGE,"E45"),sQuery(id+"F0.wireOp",EDGE,"E46"),sQuery(id+"F0.wireOp",EDGE,"E47"),sQuery(id+"F0.wireOp",EDGE,"E48"),sQuery(id+"F0.wireOp",EDGE,"E49"),sQuery(id+"F0.wireOp",EDGE,"E50"),sQuery(id+"F0.wireOp",EDGE,"E51"),sQuery(id+"F0.wireOp",EDGE,"E52"),sQuery(id+"F0.wireOp",EDGE,"E53"),sQuery(id+"F0.wireOp",EDGE,"E54"),sQuery(id+"F0.wireOp",EDGE,"E55"),sQuery(id+"F0.wireOp",EDGE,"E56"),sQuery(id+"F0.wireOp",EDGE,"E57"),sQuery(id+"F0.wireOp",EDGE,"E58"),sQuery(id+"F0.wireOp",EDGE,"E59"),sQuery(id+"F0.wireOp",EDGE,"E60"),sQuery(id+"F0.wireOp",EDGE,"E61"),sQuery(id+"F0.wireOp",EDGE,"E62"),sQuery(id+"F0.wireOp",EDGE,"E63"),sQuery(id+"F0.wireOp",EDGE,"E64"),sQuery(id+"F0.wireOp",EDGE,"E65"),sQuery(id+"F0.wireOp",EDGE,"E66"),sQuery(id+"F0.wireOp",EDGE,"E67"),sQuery(id+"F0.wireOp",EDGE,"E68"),sQuery(id+"F0.wireOp",EDGE,"E69"),sQuery(id+"F0.wireOp",EDGE,"E70"),sQuery(id+"F0.wireOp",EDGE,"E71"),sQuery(id+"F0.wireOp",EDGE,"E72"),sQuery(id+"F0.wireOp",EDGE,"E73"),sQuery(id+"F0.wireOp",EDGE,"E74"),sQuery(id+"F0.wireOp",EDGE,"E75"),sQuery(id+"F0.wireOp",EDGE,"E76"),sQuery(id+"F0.wireOp",EDGE,"E77"),sQuery(id+"F0.wireOp",EDGE,"E78"),sQuery(id+"F0.wireOp",EDGE,"E79"),sQuery(id+"F0.wireOp",EDGE,"E80"),sQuery(id+"F0.wireOp",EDGE,"E81"),sQuery(id+"F0.wireOp",EDGE,"E82"),sQuery(id+"F0.wireOp",EDGE,"E83"),sQuery(id+"F0.wireOp",EDGE,"E84"),sQuery(id+"F0.wireOp",EDGE,"E85"),sQuery(id+"F0.wireOp",EDGE,"E86"),sQuery(id+"F0.wireOp",EDGE,"E87"),sQuery(id+"F0.wireOp",EDGE,"E88"),sQuery(id+"F0.wireOp",EDGE,"E89"),sQuery(id+"F0.wireOp",EDGE,"E90"),sQuery(id+"F0.wireOp",EDGE,"E91"),sQuery(id+"F0.wireOp",EDGE,"E92"),sQuery(id+"F0.wireOp",EDGE,"E93"),sQuery(id+"F0.wireOp",EDGE,"E94"),sQuery(id+"F0.wireOp",EDGE,"E95"),sQuery(id+"F0.wireOp",EDGE,"E96"),sQuery(id+"F0.wireOp",EDGE,"E97"),sQuery(id+"F0.wireOp",EDGE,"E98"),sQuery(id+"F0.wireOp",EDGE,"E100"),sQuery(id+"F0.wireOp",EDGE,"E101"),sQuery(id+"F0.wireOp",EDGE,"E102"),sQuery(id+"F0.wireOp",EDGE,"E103"),sQuery(id+"F0.wireOp",EDGE,"E104"),sQuery(id+"F0.wireOp",EDGE,"E105"),sQuery(id+"F0.wireOp",EDGE,"E106"),sQuery(id+"F0.wireOp",EDGE,"E107"),sQuery(id+"F0.wireOp",EDGE,"E108"),sQuery(id+"F0.wireOp",EDGE,"E109"),sQuery(id+"F0.wireOp",EDGE,"E110"),sQuery(id+"F0.wireOp",EDGE,"E111"),sQuery(id+"F0.wireOp",EDGE,"E112"),sQuery(id+"F0.wireOp",EDGE,"E113"),sQuery(id+"F0.wireOp",EDGE,"E114"),sQuery(id+"F0.wireOp",EDGE,"E115"),sQuery(id+"F0.wireOp",EDGE,"E116"),sQuery(id+"F0.wireOp",EDGE,"E117"),sQuery(id+"F0.wireOp",EDGE,"E118"),sQuery(id+"F0.wireOp",EDGE,"E119"),sQuery(id+"F0.wireOp",EDGE,"E120"),sQuery(id+"F0.wireOp",EDGE,"E121"),sQuery(id+"F0.wireOp",EDGE,"E122"),sQuery(id+"F0.wireOp",EDGE,"E123"),sQuery(id+"F0.wireOp",EDGE,"E124"),sQuery(id+"F0.wireOp",EDGE,"E125"),sQuery(id+"F0.wireOp",EDGE,"E126"),sQuery(id+"F0.wireOp",EDGE,"E127"),sQuery(id+"F0.wireOp",EDGE,"E128"),sQuery(id+"F0.wireOp",EDGE,"E129"),sQuery(id+"F0.wireOp",EDGE,"E130"),sQuery(id+"F0.wireOp",EDGE,"E131"),sQuery(id+"F0.wireOp",EDGE,"E132"),sQuery(id+"F0.wireOp",EDGE,"E133"),sQuery(id+"F0.wireOp",EDGE,"E134"),sQuery(id+"F0.wireOp",EDGE,"E135"),sQuery(id+"F0.wireOp",EDGE,"E136"),sQuery(id+"F0.wireOp",EDGE,"E137"),sQuery(id+"F0.wireOp",EDGE,"E138"),sQuery(id+"F0.wireOp",EDGE,"E139"),sQuery(id+"F0.wireOp",EDGE,"E140"),sQuery(id+"F0.wireOp",EDGE,"E141"),sQuery(id+"F0.wireOp",EDGE,"E142"),sQuery(id+"F0.wireOp",EDGE,"E143"),sQuery(id+"F0.wireOp",EDGE,"E144"),sQuery(id+"F0.wireOp",EDGE,"E145"),sQuery(id+"F0.wireOp",EDGE,"E146"),sQuery(id+"F0.wireOp",EDGE,"E147"),sQuery(id+"F0.wireOp",EDGE,"E148"),sQuery(id+"F0.wireOp",EDGE,"E149"),sQuery(id+"F0.wireOp",EDGE,"E150"),sQuery(id+"F0.wireOp",EDGE,"E151"),sQuery(id+"F0.wireOp",EDGE,"E152"),sQuery(id+"F0.wireOp",EDGE,"E153"),sQuery(id+"F0.wireOp",EDGE,"E154"),sQuery(id+"F0.wireOp",EDGE,"E155"),sQuery(id+"F0.wireOp",EDGE,"E156"),sQuery(id+"F0.wireOp",EDGE,"E157"),sQuery(id+"F0.wireOp",EDGE,"E158"),sQuery(id+"F0.wireOp",EDGE,"E159"),sQuery(id+"F0.wireOp",EDGE,"E160"),sQuery(id+"F0.wireOp",EDGE,"E161"),sQuery(id+"F0.wireOp",EDGE,"E162"),sQuery(id+"F0.wireOp",EDGE,"E163"),sQuery(id+"F0.wireOp",EDGE,"E164"),sQuery(id+"F0.wireOp",EDGE,"E165"),sQuery(id+"F0.wireOp",EDGE,"E166"),sQuery(id+"F0.wireOp",EDGE,"E167"),sQuery(id+"F0.wireOp",EDGE,"E168"),sQuery(id+"F0.wireOp",EDGE,"E169"),sQuery(id+"F0.wireOp",EDGE,"E170"),sQuery(id+"F0.wireOp",EDGE,"E171"),sQuery(id+"F0.wireOp",EDGE,"E172"),sQuery(id+"F0.wireOp",EDGE,"E173"),sQuery(id+"F0.wireOp",EDGE,"E174"),sQuery(id+"F0.wireOp",EDGE,"E175"),sQuery(id+"F0.wireOp",EDGE,"E176"),sQuery(id+"F0.wireOp",EDGE,"E177"),sQuery(id+"F0.wireOp",EDGE,"E178"),sQuery(id+"F0.wireOp",EDGE,"E179"),sQuery(id+"F0.wireOp",EDGE,"E180"),sQuery(id+"F0.wireOp",EDGE,"E181"),sQuery(id+"F0.wireOp",EDGE,"E182"),sQuery(id+"F0.wireOp",EDGE,"E183"),sQuery(id+"F0.wireOp",EDGE,"E184"),sQuery(id+"F0.wireOp",EDGE,"E185"),sQuery(id+"F0.wireOp",EDGE,"E186"),sQuery(id+"F0.wireOp",EDGE,"E187"),sQuery(id+"F0.wireOp",EDGE,"E188"),sQuery(id+"F0.wireOp",EDGE,"E189"),sQuery(id+"F0.wireOp",EDGE,"E190"),sQuery(id+"F0.wireOp",EDGE,"E191"),sQuery(id+"F0.wireOp",EDGE,"E192"),sQuery(id+"F0.wireOp",EDGE,"E193"),sQuery(id+"F0.wireOp",EDGE,"E194"),sQuery(id+"F0.wireOp",EDGE,"E195"),sQuery(id+"F0.wireOp",EDGE,"E196"),sQuery(id+"F0.wireOp",EDGE,"E197"),sQuery(id+"F0.wireOp",EDGE,"E198"),sQuery(id+"F0.wireOp",EDGE,"E199"),sQuery(id+"F0.wireOp",EDGE,"E200"),sQuery(id+"F0.wireOp",EDGE,"E201"),sQuery(id+"F0.wireOp",EDGE,"E202"),sQuery(id+"F0.wireOp",EDGE,"E203"),sQuery(id+"F0.wireOp",EDGE,"E204"),sQuery(id+"F0.wireOp",EDGE,"E205"),sQuery(id+"F0.wireOp",EDGE,"E206"),sQuery(id+"F0.wireOp",EDGE,"E207"),sQuery(id+"F0.wireOp",EDGE,"E208"),sQuery(id+"F0.wireOp",EDGE,"E209"),sQuery(id+"F0.wireOp",EDGE,"E210"),sQuery(id+"F0.wireOp",EDGE,"E211"),sQuery(id+"F0.wireOp",EDGE,"E212"),sQuery(id+"F0.wireOp",EDGE,"E213"),sQuery(id+"F0.wireOp",EDGE,"E214"),sQuery(id+"F0.wireOp",EDGE,"E215"),sQuery(id+"F0.wireOp",EDGE,"E216"),sQuery(id+"F0.wireOp",EDGE,"E217"),sQuery(id+"F0.wireOp",EDGE,"E218"),sQuery(id+"F0.wireOp",EDGE,"E219"),sQuery(id+"F0.wireOp",EDGE,"E220"),sQuery(id+"F0.wireOp",EDGE,"E221"),sQuery(id+"F0.wireOp",EDGE,"E222"),sQuery(id+"F0.wireOp",EDGE,"E223"),sQuery(id+"F0.wireOp",EDGE,"E224"),sQuery(id+"F0.wireOp",EDGE,"E225"),sQuery(id+"F0.wireOp",EDGE,"E226"),sQuery(id+"F0.wireOp",EDGE,"E227"),sQuery(id+"F0.wireOp",EDGE,"E228"),sQuery(id+"F0.wireOp",EDGE,"E229"),sQuery(id+"F0.wireOp",EDGE,"E230"),sQuery(id+"F0.wireOp",EDGE,"E231"),sQuery(id+"F0.wireOp",EDGE,"E232"),sQuery(id+"F0.wireOp",EDGE,"E233"),sQuery(id+"F0.wireOp",EDGE,"E234"),sQuery(id+"F0.wireOp",EDGE,"E235"),sQuery(id+"F0.wireOp",EDGE,"E236"),sQuery(id+"F0.wireOp",EDGE,"E237"),sQuery(id+"F0.wireOp",EDGE,"E238"),sQuery(id+"F0.wireOp",EDGE,"E239"),sQuery(id+"F0.wireOp",EDGE,"E240"),sQuery(id+"F0.wireOp",EDGE,"E241"),sQuery(id+"F0.wireOp",EDGE,"E242"),sQuery(id+"F0.wireOp",EDGE,"E243"),sQuery(id+"F0.wireOp",EDGE,"E244"),sQuery(id+"F0.wireOp",EDGE,"E245"),sQuery(id+"F0.wireOp",EDGE,"E246"),sQuery(id+"F0.wireOp",EDGE,"E247"),sQuery(id+"F0.wireOp",EDGE,"E248"),sQuery(id+"F0.wireOp",EDGE,"E249"),sQuery(id+"F0.wireOp",EDGE,"E250"),sQuery(id+"F0.wireOp",EDGE,"E251"),sQuery(id+"F0.wireOp",EDGE,"E252"),sQuery(id+"F0.wireOp",EDGE,"E253"),sQuery(id+"F0.wireOp",EDGE,"E254"),sQuery(id+"F0.wireOp",EDGE,"E255"),sQuery(id+"F0.wireOp",EDGE,"E256"),sQuery(id+"F0.wireOp",EDGE,"E257"),sQuery(id+"F0.wireOp",EDGE,"E258"),sQuery(id+"F0.wireOp",EDGE,"E259"),sQuery(id+"F0.wireOp",EDGE,"E260"),sQuery(id+"F0.wireOp",EDGE,"E261"),sQuery(id+"F0.wireOp",EDGE,"E262"),sQuery(id+"F0.wireOp",EDGE,"E263"),sQuery(id+"F0.wireOp",EDGE,"E264"),sQuery(id+"F0.wireOp",EDGE,"E265"),sQuery(id+"F0.wireOp",EDGE,"E266"),sQuery(id+"F0.wireOp",EDGE,"E267"),sQuery(id+"F0.wireOp",EDGE,"E268"),sQuery(id+"F0.wireOp",EDGE,"E269"),sQuery(id+"F0.wireOp",EDGE,"E270"),sQuery(id+"F0.wireOp",EDGE,"E271"),sQuery(id+"F0.wireOp",EDGE,"E272"),sQuery(id+"F0.wireOp",EDGE,"E273"),sQuery(id+"F0.wireOp",EDGE,"E274"),sQuery(id+"F0.wireOp",EDGE,"E275"),sQuery(id+"F0.wireOp",EDGE,"E276"),sQuery(id+"F0.wireOp",EDGE,"E277"),sQuery(id+"F0.wireOp",EDGE,"E278"),sQuery(id+"F0.wireOp",EDGE,"E279"),sQuery(id+"F0.wireOp",EDGE,"E280"),sQuery(id+"F0.wireOp",EDGE,"E281"),sQuery(id+"F0.wireOp",EDGE,"E282"),sQuery(id+"F0.wireOp",EDGE,"E283"),sQuery(id+"F0.wireOp",EDGE,"E284"),sQuery(id+"F0.wireOp",EDGE,"E285"),sQuery(id+"F0.wireOp",EDGE,"E286"),sQuery(id+"F0.wireOp",EDGE,"E287"),sQuery(id+"F0.wireOp",EDGE,"E288"),sQuery(id+"F0.wireOp",EDGE,"E289"),sQuery(id+"F0.wireOp",EDGE,"E290"),sQuery(id+"F0.wireOp",EDGE,"E291"),sQuery(id+"F0.wireOp",EDGE,"E292"),sQuery(id+"F0.wireOp",EDGE,"E293"),sQuery(id+"F0.wireOp",EDGE,"E294"),sQuery(id+"F0.wireOp",EDGE,"E295"),sQuery(id+"F0.wireOp",EDGE,"E296"),sQuery(id+"F0.wireOp",EDGE,"E297"),sQuery(id+"F0.wireOp",EDGE,"E298"),sQuery(id+"F0.wireOp",EDGE,"E299"),sQuery(id+"F0.wireOp",EDGE,"E300"),sQuery(id+"F0.wireOp",EDGE,"E301"),sQuery(id+"F0.wireOp",EDGE,"E302"),sQuery(id+"F0.wireOp",EDGE,"E303"),sQuery(id+"F0.wireOp",EDGE,"E304"),sQuery(id+"F0.wireOp",EDGE,"E305"),sQuery(id+"F0.wireOp",EDGE,"E306"),sQuery(id+"F0.wireOp",EDGE,"E307"),sQuery(id+"F0.wireOp",EDGE,"E308"),sQuery(id+"F0.wireOp",EDGE,"E309"),sQuery(id+"F0.wireOp",EDGE,"E310"),sQuery(id+"F0.wireOp",EDGE,"E311"),sQuery(id+"F0.wireOp",EDGE,"E312"),sQuery(id+"F0.wireOp",EDGE,"E313"),sQuery(id+"F0.wireOp",EDGE,"E314"),sQuery(id+"F0.wireOp",EDGE,"E315"),sQuery(id+"F0.wireOp",EDGE,"E316"),sQuery(id+"F0.wireOp",EDGE,"E317"),sQuery(id+"F0.wireOp",EDGE,"E318"),sQuery(id+"F0.wireOp",EDGE,"E319"),sQuery(id+"F0.wireOp",EDGE,"E320"),sQuery(id+"F0.wireOp",EDGE,"E321"),sQuery(id+"F0.wireOp",EDGE,"E322"),sQuery(id+"F0.wireOp",EDGE,"E323"),sQuery(id+"F0.wireOp",EDGE,"E324"),sQuery(id+"F0.wireOp",EDGE,"E325"),sQuery(id+"F0.wireOp",EDGE,"E326"),sQuery(id+"F0.wireOp",EDGE,"E327"),sQuery(id+"F0.wireOp",EDGE,"E328"),sQuery(id+"F0.wireOp",EDGE,"E329"),sQuery(id+"F0.wireOp",EDGE,"E330"),sQuery(id+"F0.wireOp",EDGE,"E331"),sQuery(id+"F0.wireOp",EDGE,"E332"),sQuery(id+"F0.wireOp",EDGE,"E333"),sQuery(id+"F0.wireOp",EDGE,"E334"),sQuery(id+"F0.wireOp",EDGE,"E335"),sQuery(id+"F0.wireOp",EDGE,"E336"),sQuery(id+"F0.wireOp",EDGE,"E337"),sQuery(id+"F0.wireOp",EDGE,"E338"),sQuery(id+"F0.wireOp",EDGE,"E339"),sQuery(id+"F0.wireOp",EDGE,"E340"),sQuery(id+"F0.wireOp",EDGE,"E341"),sQuery(id+"F0.wireOp",EDGE,"E342"),sQuery(id+"F0.wireOp",EDGE,"E343"),sQuery(id+"F0.wireOp",EDGE,"E344"),sQuery(id+"F0.wireOp",EDGE,"E345"),sQuery(id+"F0.wireOp",EDGE,"E346"),sQuery(id+"F0.wireOp",EDGE,"E347"),sQuery(id+"F0.wireOp",EDGE,"E348"),sQuery(id+"F0.wireOp",EDGE,"E349"),sQuery(id+"F0.wireOp",EDGE,"E350"),sQuery(id+"F0.wireOp",EDGE,"E351"),sQuery(id+"F0.wireOp",EDGE,"E352"),sQuery(id+"F0.wireOp",EDGE,"E353"),sQuery(id+"F0.wireOp",EDGE,"E354"),sQuery(id+"F0.wireOp",EDGE,"E355"),sQuery(id+"F0.wireOp",EDGE,"E356"),sQuery(id+"F0.wireOp",EDGE,"E357"),sQuery(id+"F0.wireOp",EDGE,"E358"),sQuery(id+"F0.wireOp",EDGE,"E359"),sQuery(id+"F0.wireOp",EDGE,"E360"),sQuery(id+"F0.wireOp",EDGE,"E361"),sQuery(id+"F0.wireOp",EDGE,"E362"),sQuery(id+"F0.wireOp",EDGE,"E363"),sQuery(id+"F0.wireOp",EDGE,"E364"),sQuery(id+"F0.wireOp",EDGE,"E365"),sQuery(id+"F0.wireOp",EDGE,"E366"),sQuery(id+"F0.wireOp",EDGE,"E367"),sQuery(id+"F0.wireOp",EDGE,"E368"),sQuery(id+"F0.wireOp",EDGE,"E369"),sQuery(id+"F0.wireOp",EDGE,"E370"),sQuery(id+"F0.wireOp",EDGE,"E371"),sQuery(id+"F0.wireOp",EDGE,"E372"),sQuery(id+"F0.wireOp",EDGE,"E373"),sQuery(id+"F0.wireOp",EDGE,"E374"),sQuery(id+"F0.wireOp",EDGE,"E375"),sQuery(id+"F0.wireOp",EDGE,"E376"),sQuery(id+"F0.wireOp",EDGE,"E377"),sQuery(id+"F0.wireOp",EDGE,"E378"),sQuery(id+"F0.wireOp",EDGE,"E379"),sQuery(id+"F0.wireOp",EDGE,"E380"),sQuery(id+"F0.wireOp",EDGE,"E381"),sQuery(id+"F0.wireOp",EDGE,"E382"),sQuery(id+"F0.wireOp",EDGE,"E383"),sQuery(id+"F0.wireOp",EDGE,"E384"),sQuery(id+"F0.wireOp",EDGE,"E385"),sQuery(id+"F0.wireOp",EDGE,"E386"),sQuery(id+"F0.wireOp",EDGE,"E387"),sQuery(id+"F0.wireOp",EDGE,"E388"),sQuery(id+"F0.wireOp",EDGE,"E389"),sQuery(id+"F0.wireOp",EDGE,"E390"),sQuery(id+"F0.wireOp",EDGE,"E391"),sQuery(id+"F0.wireOp",EDGE,"E392"),sQuery(id+"F0.wireOp",EDGE,"E393"),sQuery(id+"F0.wireOp",EDGE,"E394"),sQuery(id+"F0.wireOp",EDGE,"E395"),sQuery(id+"F0.wireOp",EDGE,"E396"),sQuery(id+"F0.wireOp",EDGE,"E397"),sQuery(id+"F0.wireOp",EDGE,"E398"),sQuery(id+"F0.wireOp",EDGE,"E399"),sQuery(id+"F0.wireOp",EDGE,"E400"),sQuery(id+"F0.wireOp",EDGE,"E401"),sQuery(id+"F0.wireOp",EDGE,"E402"),sQuery(id+"F0.wireOp",EDGE,"E403"),sQuery(id+"F0.wireOp",EDGE,"E404"),sQuery(id+"F0.wireOp",EDGE,"E405"),sQuery(id+"F0.wireOp",EDGE,"E406"),sQuery(id+"F0.wireOp",EDGE,"E407"),sQuery(id+"F0.wireOp",EDGE,"E408"),sQuery(id+"F0.wireOp",EDGE,"E409"),sQuery(id+"F0.wireOp",EDGE,"E410"),sQuery(id+"F0.wireOp",EDGE,"E411"),sQuery(id+"F0.wireOp",EDGE,"E412"),sQuery(id+"F0.wireOp",EDGE,"E413"),sQuery(id+"F0.wireOp",EDGE,"E414"),sQuery(id+"F0.wireOp",EDGE,"E415"),sQuery(id+"F0.wireOp",EDGE,"E416"),sQuery(id+"F0.wireOp",EDGE,"E417"),sQuery(id+"F0.wireOp",EDGE,"E418"),sQuery(id+"F0.wireOp",EDGE,"E419"),sQuery(id+"F0.wireOp",EDGE,"E420"),sQuery(id+"F0.wireOp",EDGE,"E421"),sQuery(id+"F0.wireOp",EDGE,"E422"),sQuery(id+"F0.wireOp",EDGE,"E423"),sQuery(id+"F0.wireOp",EDGE,"E424"),sQuery(id+"F0.wireOp",EDGE,"E425"),sQuery(id+"F0.wireOp",EDGE,"E426"),sQuery(id+"F0.wireOp",EDGE,"E427"),sQuery(id+"F0.wireOp",EDGE,"E428"),sQuery(id+"F0.wireOp",EDGE,"E429"),sQuery(id+"F0.wireOp",EDGE,"E430"),sQuery(id+"F0.wireOp",EDGE,"E431"),sQuery(id+"F0.wireOp",EDGE,"E432"),sQuery(id+"F0.wireOp",EDGE,"E433"),sQuery(id+"F0.wireOp",EDGE,"E434"),sQuery(id+"F0.wireOp",EDGE,"E435"),sQuery(id+"F0.wireOp",EDGE,"E436"),sQuery(id+"F0.wireOp",EDGE,"E437"),sQuery(id+"F0.wireOp",EDGE,"E438"),sQuery(id+"F0.wireOp",EDGE,"E439"),sQuery(id+"F0.wireOp",EDGE,"E440"),sQuery(id+"F0.wireOp",EDGE,"E441"),sQuery(id+"F0.wireOp",EDGE,"E442"),sQuery(id+"F0.wireOp",EDGE,"E443"),sQuery(id+"F0.wireOp",EDGE,"E444"),sQuery(id+"F0.wireOp",EDGE,"E445"),sQuery(id+"F0.wireOp",EDGE,"E446"),sQuery(id+"F0.wireOp",EDGE,"E447"),sQuery(id+"F0.wireOp",EDGE,"E448"),sQuery(id+"F0.wireOp",EDGE,"E449"),sQuery(id+"F0.wireOp",EDGE,"E450"),sQuery(id+"F0.wireOp",EDGE,"E451"),sQuery(id+"F0.wireOp",EDGE,"E452"),sQuery(id+"F0.wireOp",EDGE,"E453"),sQuery(id+"F0.wireOp",EDGE,"E454"),sQuery(id+"F0.wireOp",EDGE,"E455"),sQuery(id+"F0.wireOp",EDGE,"E456"),sQuery(id+"F0.wireOp",EDGE,"E457"),sQuery(id+"F0.wireOp",EDGE,"E458"),sQuery(id+"F0.wireOp",EDGE,"E459"),sQuery(id+"F0.wireOp",EDGE,"E460"),sQuery(id+"F0.wireOp",EDGE,"E461"),sQuery(id+"F0.wireOp",EDGE,"E462"),sQuery(id+"F0.wireOp",EDGE,"E463"),sQuery(id+"F0.wireOp",EDGE,"E464"),sQuery(id+"F0.wireOp",EDGE,"E465"),sQuery(id+"F0.wireOp",EDGE,"E466"),sQuery(id+"F0.wireOp",EDGE,"E467"),sQuery(id+"F0.wireOp",EDGE,"E468"),sQuery(id+"F0.wireOp",EDGE,"E469"),sQuery(id+"F0.wireOp",EDGE,"E470"),sQuery(id+"F0.wireOp",EDGE,"E471"),sQuery(id+"F0.wireOp",EDGE,"E472"),sQuery(id+"F0.wireOp",EDGE,"E473"),sQuery(id+"F0.wireOp",EDGE,"E474"),sQuery(id+"F0.wireOp",EDGE,"E475"),sQuery(id+"F0.wireOp",EDGE,"E476"),sQuery(id+"F0.wireOp",EDGE,"E477"),sQuery(id+"F0.wireOp",EDGE,"E478"),sQuery(id+"F0.wireOp",EDGE,"E479"),sQuery(id+"F0.wireOp",EDGE,"E480"),sQuery(id+"F0.wireOp",EDGE,"E481"),sQuery(id+"F0.wireOp",EDGE,"E482"),sQuery(id+"F0.wireOp",EDGE,"E483"),sQuery(id+"F0.wireOp",EDGE,"E484"),sQuery(id+"F0.wireOp",EDGE,"E485"),sQuery(id+"F0.wireOp",EDGE,"E486"),sQuery(id+"F0.wireOp",EDGE,"E487"),sQuery(id+"F0.wireOp",EDGE,"E488"),sQuery(id+"F0.wireOp",EDGE,"E489"),sQuery(id+"F0.wireOp",EDGE,"E490"),sQuery(id+"F0.wireOp",EDGE,"E491"),sQuery(id+"F0.wireOp",EDGE,"E492"),sQuery(id+"F0.wireOp",EDGE,"E493"),sQuery(id+"F0.wireOp",EDGE,"E494"),sQuery(id+"F0.wireOp",EDGE,"E495"),sQuery(id+"F0.wireOp",EDGE,"E496"),sQuery(id+"F0.wireOp",EDGE,"E497"),sQuery(id+"F0.wireOp",EDGE,"E498"),sQuery(id+"F0.wireOp",EDGE,"E499"),sQuery(id+"F0.wireOp",EDGE,"E500"),sQuery(id+"F0.wireOp",EDGE,"E501"),sQuery(id+"F0.wireOp",EDGE,"E502"),sQuery(id+"F0.wireOp",EDGE,"E503"),sQuery(id+"F0.wireOp",EDGE,"E504"),sQuery(id+"F0.wireOp",EDGE,"E505"),sQuery(id+"F0.wireOp",EDGE,"E506"),sQuery(id+"F0.wireOp",EDGE,"E507"),sQuery(id+"F0.wireOp",EDGE,"E508"),sQuery(id+"F0.wireOp",EDGE,"E509"),sQuery(id+"F0.wireOp",EDGE,"E510"),sQuery(id+"F0.wireOp",EDGE,"E511"),sQuery(id+"F0.wireOp",EDGE,"E512"),sQuery(id+"F0.wireOp",EDGE,"E513"),sQuery(id+"F0.wireOp",EDGE,"E514"),sQuery(id+"F0.wireOp",EDGE,"E515"),sQuery(id+"F0.wireOp",EDGE,"E516"),sQuery(id+"F0.wireOp",EDGE,"E517"),sQuery(id+"F0.wireOp",EDGE,"E518"),sQuery(id+"F0.wireOp",EDGE,"E519"),sQuery(id+"F0.wireOp",EDGE,"E520"),sQuery(id+"F0.wireOp",EDGE,"E521"),sQuery(id+"F0.wireOp",EDGE,"E522"),sQuery(id+"F0.wireOp",EDGE,"E523"),sQuery(id+"F0.wireOp",EDGE,"E524"),sQuery(id+"F0.wireOp",EDGE,"E525"),sQuery(id+"F0.wireOp",EDGE,"E526"),sQuery(id+"F0.wireOp",EDGE,"E527"),sQuery(id+"F0.wireOp",EDGE,"E528"),sQuery(id+"F0.wireOp",EDGE,"E529"),sQuery(id+"F0.wireOp",EDGE,"E530"),sQuery(id+"F0.wireOp",EDGE,"E531"),sQuery(id+"F0.wireOp",EDGE,"E532"),sQuery(id+"F0.wireOp",EDGE,"E533"),sQuery(id+"F0.wireOp",EDGE,"E534"),sQuery(id+"F0.wireOp",EDGE,"E535"),sQuery(id+"F0.wireOp",EDGE,"E536"),sQuery(id+"F0.wireOp",EDGE,"E537"),sQuery(id+"F0.wireOp",EDGE,"E538"),sQuery(id+"F0.wireOp",EDGE,"E539"),sQuery(id+"F0.wireOp",EDGE,"E540"),sQuery(id+"F0.wireOp",EDGE,"E541"),sQuery(id+"F0.wireOp",EDGE,"E542"),sQuery(id+"F0.wireOp",EDGE,"E543"),sQuery(id+"F0.wireOp",EDGE,"E544"),sQuery(id+"F0.wireOp",EDGE,"E545"),sQuery(id+"F0.wireOp",EDGE,"E546"),sQuery(id+"F0.wireOp",EDGE,"E547"),sQuery(id+"F0.wireOp",EDGE,"E548"),sQuery(id+"F0.wireOp",EDGE,"E549"),sQuery(id+"F0.wireOp",EDGE,"E550"),sQuery(id+"F0.wireOp",EDGE,"E551"),sQuery(id+"F0.wireOp",EDGE,"E552"),sQuery(id+"F0.wireOp",EDGE,"E553"),sQuery(id+"F0.wireOp",EDGE,"E554"),sQuery(id+"F0.wireOp",EDGE,"E555"),sQuery(id+"F0.wireOp",EDGE,"E556"),sQuery(id+"F0.wireOp",EDGE,"E557"),sQuery(id+"F0.wireOp",EDGE,"E558"),sQuery(id+"F0.wireOp",EDGE,"E559"),sQuery(id+"F0.wireOp",EDGE,"E560"),sQuery(id+"F0.wireOp",EDGE,"E561"),sQuery(id+"F0.wireOp",EDGE,"E562"),sQuery(id+"F0.wireOp",EDGE,"E563"),sQuery(id+"F0.wireOp",EDGE,"E564"),sQuery(id+"F0.wireOp",EDGE,"E565"),sQuery(id+"F0.wireOp",EDGE,"E566"),sQuery(id+"F0.wireOp",EDGE,"E567"),sQuery(id+"F0.wireOp",EDGE,"E568"),sQuery(id+"F0.wireOp",EDGE,"E569"),sQuery(id+"F0.wireOp",EDGE,"E570"),sQuery(id+"F0.wireOp",EDGE,"E571"),sQuery(id+"F0.wireOp",EDGE,"E572"),sQuery(id+"F0.wireOp",EDGE,"E573"),sQuery(id+"F0.wireOp",EDGE,"E574"),sQuery(id+"F0.wireOp",EDGE,"E575"),sQuery(id+"F0.wireOp",EDGE,"E576"),sQuery(id+"F0.wireOp",EDGE,"E577"),sQuery(id+"F0.wireOp",EDGE,"E578"),sQuery(id+"F0.wireOp",EDGE,"E579"),sQuery(id+"F0.wireOp",EDGE,"E580"),sQuery(id+"F0.wireOp",EDGE,"E581"),sQuery(id+"F0.wireOp",EDGE,"E582"),sQuery(id+"F0.wireOp",EDGE,"E583"),sQuery(id+"F0.wireOp",EDGE,"E584"),sQuery(id+"F0.wireOp",EDGE,"E585"),sQuery(id+"F0.wireOp",EDGE,"E586"),sQuery(id+"F0.wireOp",EDGE,"E587"),sQuery(id+"F0.wireOp",EDGE,"E588"),sQuery(id+"F0.wireOp",EDGE,"E589"),sQuery(id+"F0.wireOp",EDGE,"E590"),sQuery(id+"F0.wireOp",EDGE,"E591"),sQuery(id+"F0.wireOp",EDGE,"E592"),sQuery(id+"F0.wireOp",EDGE,"E593"),sQuery(id+"F0.wireOp",EDGE,"E594"),sQuery(id+"F0.wireOp",EDGE,"E595"),sQuery(id+"F0.wireOp",EDGE,"E597"),sQuery(id+"F0.wireOp",EDGE,"E598"),sQuery(id+"F0.wireOp",EDGE,"E599"),sQuery(id+"F0.wireOp",EDGE,"E600"),sQuery(id+"F0.wireOp",EDGE,"E601"),sQuery(id+"F0.wireOp",EDGE,"E602"),sQuery(id+"F0.wireOp",EDGE,"E603"),sQuery(id+"F0.wireOp",EDGE,"E604"),sQuery(id+"F0.wireOp",EDGE,"E605"),sQuery(id+"F0.wireOp",EDGE,"E606"),sQuery(id+"F0.wireOp",EDGE,"E607"),sQuery(id+"F0.wireOp",EDGE,"E608"),sQuery(id+"F0.wireOp",EDGE,"E609"),sQuery(id+"F0.wireOp",EDGE,"E610"),sQuery(id+"F0.wireOp",EDGE,"E611"),sQuery(id+"F0.wireOp",EDGE,"E612"),sQuery(id+"F0.wireOp",EDGE,"E613"),sQuery(id+"F0.wireOp",EDGE,"E614"),sQuery(id+"F0.wireOp",EDGE,"E615"),sQuery(id+"F0.wireOp",EDGE,"E616"),sQuery(id+"F0.wireOp",EDGE,"E617"),sQuery(id+"F0.wireOp",EDGE,"E618"),sQuery(id+"F0.wireOp",EDGE,"E619"),sQuery(id+"F0.wireOp",EDGE,"E620"),sQuery(id+"F0.wireOp",EDGE,"E621"),sQuery(id+"F0.wireOp",EDGE,"E622"),sQuery(id+"F0.wireOp",EDGE,"E623"),sQuery(id+"F0.wireOp",EDGE,"E624"),sQuery(id+"F0.wireOp",EDGE,"E625"),sQuery(id+"F0.wireOp",EDGE,"E626"),sQuery(id+"F0.wireOp",EDGE,"E627"),sQuery(id+"F0.wireOp",EDGE,"E628"),sQuery(id+"F0.wireOp",EDGE,"E629"),sQuery(id+"F0.wireOp",EDGE,"E630"),sQuery(id+"F0.wireOp",EDGE,"E631"),sQuery(id+"F0.wireOp",EDGE,"E632"),sQuery(id+"F0.wireOp",EDGE,"E633"),sQuery(id+"F0.wireOp",EDGE,"E634"),sQuery(id+"F0.wireOp",EDGE,"E635"),sQuery(id+"F0.wireOp",EDGE,"E636"),sQuery(id+"F0.wireOp",EDGE,"E637"),sQuery(id+"F0.wireOp",EDGE,"E638"),sQuery(id+"F0.wireOp",EDGE,"E639"),sQuery(id+"F0.wireOp",EDGE,"E640"),sQuery(id+"F0.wireOp",EDGE,"E641"),sQuery(id+"F0.wireOp",EDGE,"E642"),sQuery(id+"F0.wireOp",EDGE,"E643"),sQuery(id+"F0.wireOp",EDGE,"E644"),sQuery(id+"F0.wireOp",EDGE,"E645"),sQuery(id+"F0.wireOp",EDGE,"E646"),sQuery(id+"F0.wireOp",EDGE,"E647"),sQuery(id+"F0.wireOp",EDGE,"E648"),sQuery(id+"F0.wireOp",EDGE,"E649"),sQuery(id+"F0.wireOp",EDGE,"E650"),sQuery(id+"F0.wireOp",EDGE,"E651"),sQuery(id+"F0.wireOp",EDGE,"E652"),sQuery(id+"F0.wireOp",EDGE,"E653"),sQuery(id+"F0.wireOp",EDGE,"E654"),sQuery(id+"F0.wireOp",EDGE,"E655"),sQuery(id+"F0.wireOp",EDGE,"E656"),sQuery(id+"F0.wireOp",EDGE,"E657"),sQuery(id+"F0.wireOp",EDGE,"E658"),sQuery(id+"F0.wireOp",EDGE,"E659"),sQuery(id+"F0.wireOp",EDGE,"E660"),sQuery(id+"F0.wireOp",EDGE,"E661"),sQuery(id+"F0.wireOp",EDGE,"E662"),sQuery(id+"F0.wireOp",EDGE,"E663"),sQuery(id+"F0.wireOp",EDGE,"E664"),sQuery(id+"F0.wireOp",EDGE,"E665"),sQuery(id+"F0.wireOp",EDGE,"E666"),sQuery(id+"F0.wireOp",EDGE,"E667"),sQuery(id+"F0.wireOp",EDGE,"E668"),sQuery(id+"F0.wireOp",EDGE,"E669"),sQuery(id+"F0.wireOp",EDGE,"E670"),sQuery(id+"F0.wireOp",EDGE,"E671"),sQuery(id+"F0.wireOp",EDGE,"E672"),sQuery(id+"F0.wireOp",EDGE,"E673"),sQuery(id+"F0.wireOp",EDGE,"E674"),sQuery(id+"F0.wireOp",EDGE,"E675"),sQuery(id+"F0.wireOp",EDGE,"E676"),sQuery(id+"F0.wireOp",EDGE,"E677"),sQuery(id+"F0.wireOp",EDGE,"E678"),sQuery(id+"F0.wireOp",EDGE,"E679"),sQuery(id+"F0.wireOp",EDGE,"E680"),sQuery(id+"F0.wireOp",EDGE,"E681"),sQuery(id+"F0.wireOp",EDGE,"E682"),sQuery(id+"F0.wireOp",EDGE,"E683"),sQuery(id+"F0.wireOp",EDGE,"E684"),sQuery(id+"F0.wireOp",EDGE,"E685"),sQuery(id+"F0.wireOp",EDGE,"E686"),sQuery(id+"F0.wireOp",EDGE,"E687"),sQuery(id+"F0.wireOp",EDGE,"E688"),sQuery(id+"F0.wireOp",EDGE,"E689"),sQuery(id+"F0.wireOp",EDGE,"E690"),sQuery(id+"F0.wireOp",EDGE,"E691"),sQuery(id+"F0.wireOp",EDGE,"E692"),sQuery(id+"F0.wireOp",EDGE,"E693"),sQuery(id+"F0.wireOp",EDGE,"E694"),sQuery(id+"F0.wireOp",EDGE,"E695"),sQuery(id+"F0.wireOp",EDGE,"E696"),sQuery(id+"F0.wireOp",EDGE,"E697"),sQuery(id+"F0.wireOp",EDGE,"E698"),sQuery(id+"F0.wireOp",EDGE,"E699"),sQuery(id+"F0.wireOp",EDGE,"E700"),sQuery(id+"F0.wireOp",EDGE,"E701"),sQuery(id+"F0.wireOp",EDGE,"E702"),sQuery(id+"F0.wireOp",EDGE,"E703"),sQuery(id+"F0.wireOp",EDGE,"E704"),sQuery(id+"F0.wireOp",EDGE,"E705"),sQuery(id+"F0.wireOp",EDGE,"E706"),sQuery(id+"F0.wireOp",EDGE,"E707"),sQuery(id+"F0.wireOp",EDGE,"E708"),sQuery(id+"F0.wireOp",EDGE,"E709"),sQuery(id+"F0.wireOp",EDGE,"E710"),sQuery(id+"F0.wireOp",EDGE,"E711"),sQuery(id+"F0.wireOp",EDGE,"E712"),sQuery(id+"F0.wireOp",EDGE,"E713"),sQuery(id+"F0.wireOp",EDGE,"E714"),sQuery(id+"F0.wireOp",EDGE,"E715"),sQuery(id+"F0.wireOp",EDGE,"E716"),sQuery(id+"F0.wireOp",EDGE,"E717"),sQuery(id+"F0.wireOp",EDGE,"E718"),sQuery(id+"F0.wireOp",EDGE,"E719"),sQuery(id+"F0.wireOp",EDGE,"E720"),sQuery(id+"F0.wireOp",EDGE,"E721"),sQuery(id+"F0.wireOp",EDGE,"E722"),sQuery(id+"F0.wireOp",EDGE,"E723"),sQuery(id+"F0.wireOp",EDGE,"E724"),sQuery(id+"F0.wireOp",EDGE,"E725"),sQuery(id+"F0.wireOp",EDGE,"E726"),sQuery(id+"F0.wireOp",EDGE,"E727"),sQuery(id+"F0.wireOp",EDGE,"E728"),sQuery(id+"F0.wireOp",EDGE,"E729"),sQuery(id+"F0.wireOp",EDGE,"E730"),sQuery(id+"F0.wireOp",EDGE,"E731"),sQuery(id+"F0.wireOp",EDGE,"E732"),sQuery(id+"F0.wireOp",EDGE,"E733"),sQuery(id+"F0.wireOp",EDGE,"E734"),sQuery(id+"F0.wireOp",EDGE,"E735"),sQuery(id+"F0.wireOp",EDGE,"E736"),sQuery(id+"F0.wireOp",EDGE,"E737"),sQuery(id+"F0.wireOp",EDGE,"E738"),sQuery(id+"F0.wireOp",EDGE,"E739"),sQuery(id+"F0.wireOp",EDGE,"E740"),sQuery(id+"F0.wireOp",EDGE,"E741"),sQuery(id+"F0.wireOp",EDGE,"E742"),sQuery(id+"F0.wireOp",EDGE,"E743"),sQuery(id+"F0.wireOp",EDGE,"E744"),sQuery(id+"F0.wireOp",EDGE,"E745"),sQuery(id+"F0.wireOp",EDGE,"E746"),sQuery(id+"F0.wireOp",EDGE,"E747"),sQuery(id+"F0.wireOp",EDGE,"E748"),sQuery(id+"F0.wireOp",EDGE,"E749"),sQuery(id+"F0.wireOp",EDGE,"E750"),sQuery(id+"F0.wireOp",EDGE,"E751"),sQuery(id+"F0.wireOp",EDGE,"E752"),sQuery(id+"F0.wireOp",EDGE,"E753"),sQuery(id+"F0.wireOp",EDGE,"E754"),sQuery(id+"F0.wireOp",EDGE,"E755"),sQuery(id+"F0.wireOp",EDGE,"E756"),sQuery(id+"F0.wireOp",EDGE,"E757"),sQuery(id+"F0.wireOp",EDGE,"E758"),sQuery(id+"F0.wireOp",EDGE,"E759"),sQuery(id+"F0.wireOp",EDGE,"E760"),sQuery(id+"F0.wireOp",EDGE,"E761"),sQuery(id+"F0.wireOp",EDGE,"E762"),sQuery(id+"F0.wireOp",EDGE,"E763"),sQuery(id+"F0.wireOp",EDGE,"E764"),sQuery(id+"F0.wireOp",EDGE,"E765"),sQuery(id+"F0.wireOp",EDGE,"E766"),sQuery(id+"F0.wireOp",EDGE,"E767"),sQuery(id+"F0.wireOp",EDGE,"E768"),sQuery(id+"F0.wireOp",EDGE,"E769"),sQuery(id+"F0.wireOp",EDGE,"E770"),sQuery(id+"F0.wireOp",EDGE,"E771"),sQuery(id+"F0.wireOp",EDGE,"E772"),sQuery(id+"F0.wireOp",EDGE,"E773"),sQuery(id+"F0.wireOp",EDGE,"E774"),sQuery(id+"F0.wireOp",EDGE,"E775"),sQuery(id+"F0.wireOp",EDGE,"E776"),sQuery(id+"F0.wireOp",EDGE,"E777"),sQuery(id+"F0.wireOp",EDGE,"E778"),sQuery(id+"F0.wireOp",EDGE,"E779"),sQuery(id+"F0.wireOp",EDGE,"E780"),sQuery(id+"F0.wireOp",EDGE,"E781"),sQuery(id+"F0.wireOp",EDGE,"E782"),sQuery(id+"F0.wireOp",EDGE,"E783"),sQuery(id+"F0.wireOp",EDGE,"E784"),sQuery(id+"F0.wireOp",EDGE,"E785"),sQuery(id+"F0.wireOp",EDGE,"E786"),sQuery(id+"F0.wireOp",EDGE,"E787"),sQuery(id+"F0.wireOp",EDGE,"E788"),sQuery(id+"F0.wireOp",EDGE,"E789"),sQuery(id+"F0.wireOp",EDGE,"E790.filletArc"),sQuery(id+"F0.wireOp",EDGE,"E791"),sQuery(id+"F0.wireOp",EDGE,"E792"),sQuery(id+"F0.wireOp",EDGE,"E793"),sQuery(id+"F0.wireOp",EDGE,"E794"),sQuery(id+"F0.wireOp",EDGE,"E795")])],"isStart":false});
            var sketch = newSketch(context, id + "F10", { "sketchPlane" : qUnion([Q0])});
            skCircle(sketch, "E1763", {"center": v(35.07, 96.72) * mm, "radius": 2.41 * mm});
            skSolve(sketch);
        }
        {
            var Q0;
            Q0 = qSketchRegion(id + "F10", true);
            extrude(context, id + "F11", {"entities" : qUnion([Q0]), "operationType" : NewBodyOperationType.REMOVE, "endBound" : BoundingType.THROUGH_ALL, "oppositeDirection" : true, "depth" : 25.4 * mm, "offsetDistance" : 25.4 * mm});
        }
    });
